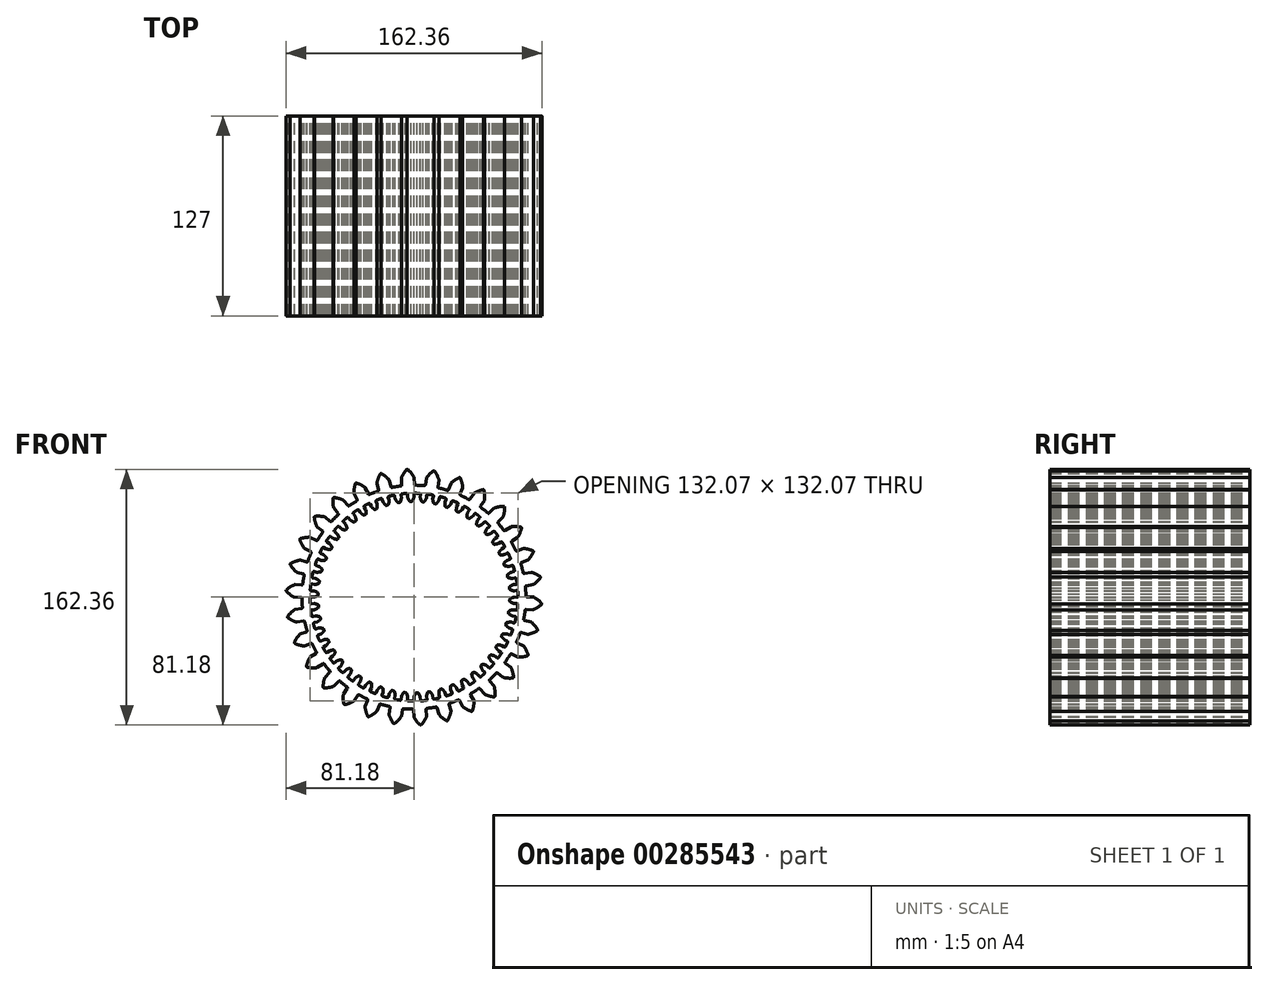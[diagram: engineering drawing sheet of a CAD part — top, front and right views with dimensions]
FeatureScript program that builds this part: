
annotation { "Feature Type Name" : "Feature", "Feature Type Description" : "" }
export const myFeature = defineFeature(function(context is Context, id is Id, definition is map)
    precondition{}
    {
        {
            var Q0;
            Q0=qCreatedBy(makeId("Front.planeOp"),FACE);
            var sketch = newSketch(context, id + "F0", { "sketchPlane" : qUnion([Q0])});
            skArc(sketch, "E0.MirrorCS", {"start": v(-3.95, 63.27) * mm, "mid": v(-3.48, 62.2) * mm, "end": v(-2.94, 61.17) * mm});
            skLineSegment(sketch, "E1.MirrorCS", {"start": v(-2.38, 60.85) * mm, "end": v(-1.91, 60.85) * mm});
            skLineSegment(sketch, "E2.MirrorCS", {"start": v(-1.44, 60.88) * mm, "end": v(-1.91, 60.85) * mm});
            skArc(sketch, "E3.MirrorCS", {"start": v(-0.03, 63.4) * mm, "mid": v(-0.43, 62.3) * mm, "end": v(-0.91, 61.23) * mm});
            skLineSegment(sketch, "E4.MirrorCS", {"start": v(-4, 63.48) * mm, "end": v(-4.05, 65.26) * mm});
            skLineSegment(sketch, "E5.MirrorCS", {"start": v(0, 63.6) * mm, "end": v(-0.06, 65.38) * mm});
            skArc(sketch, "E6", {"start": v(-4.73, 65.87) * mm, "mid": v(2.07, -66) * mm, "end": v(0.58, 66.04) * mm});
            skPoint(sketch, "E7.visualSharp", {"position": v(0, 63.5) * mm});
            skArc(sketch, "E7.filletArc", {"start": v(-0.03, 63.4) * mm, "mid": v(0, 63.5) * mm, "end": v(0, 63.6) * mm});
            skPoint(sketch, "E8.visualSharp", {"position": v(-3.99, 63.37) * mm});
            skArc(sketch, "E8.filletArc", {"start": v(-4, 63.48) * mm, "mid": v(-3.98, 63.38) * mm, "end": v(-3.95, 63.27) * mm});
            skPoint(sketch, "E9.visualSharp", {"position": v(-2.75, 60.85) * mm});
            skArc(sketch, "E9.filletArc", {"start": v(-2.94, 61.17) * mm, "mid": v(-2.7, 60.93) * mm, "end": v(-2.38, 60.85) * mm});
            skPoint(sketch, "E10.visualSharp", {"position": v(-1.08, 60.9) * mm});
            skArc(sketch, "E10.filletArc", {"start": v(-1.44, 60.88) * mm, "mid": v(-1.13, 60.98) * mm, "end": v(-0.91, 61.23) * mm});
            skPoint(sketch, "E11.visualSharp", {"position": v(-4.07, 65.91) * mm});
            skArc(sketch, "E11.filletArc", {"start": v(-4.05, 65.26) * mm, "mid": v(-4.26, 65.7) * mm, "end": v(-4.73, 65.87) * mm});
            skPoint(sketch, "E12.visualSharp", {"position": v(-0.08, 66.04) * mm});
            skArc(sketch, "E12.filletArc", {"start": v(0.58, 66.04) * mm, "mid": v(0.12, 65.85) * mm, "end": v(-0.06, 65.38) * mm});
            skPoint(sketch, "E13.1.1", {"position": v(-57.15, -33.09) * mm});
            skPoint(sketch, "E13.2.1", {"position": v(57.23, -32.95) * mm});
            skArc(sketch, "E14.1.0", {"start": v(-12.2, 64.24) * mm, "mid": v(-12.46, 64.66) * mm, "end": v(-12.95, 64.76) * mm});
            skArc(sketch, "E14.1.1", {"start": v(-7.7, 65.59) * mm, "mid": v(-8.13, 65.34) * mm, "end": v(-8.25, 64.86) * mm});
            skLineSegment(sketch, "E14.1.2", {"start": v(-7.98, 63.1) * mm, "end": v(-8.25, 64.86) * mm});
            skLineSegment(sketch, "E14.1.3", {"start": v(-11.92, 62.48) * mm, "end": v(-12.2, 64.24) * mm});
            skArc(sketch, "E14.1.4", {"start": v(-11.85, 62.28) * mm, "mid": v(-11.25, 61.27) * mm, "end": v(-10.58, 60.31) * mm});
            skPoint(sketch, "E14.1.5", {"position": v(-10.35, 60.02) * mm});
            skArc(sketch, "E14.1.6", {"start": v(-7.98, 62.9) * mm, "mid": v(-8.24, 61.75) * mm, "end": v(-8.58, 60.63) * mm});
            skPoint(sketch, "E14.1.7", {"position": v(-7.96, 63) * mm});
            skPoint(sketch, "E14.1.8", {"position": v(-11.9, 62.38) * mm});
            skPoint(sketch, "E14.1.9", {"position": v(-8.7, 60.28) * mm});
            skArc(sketch, "E14.1.10", {"start": v(-10.58, 60.31) * mm, "mid": v(-10.32, 60.11) * mm, "end": v(-10, 60.07) * mm});
            skArc(sketch, "E14.1.11", {"start": v(-9.06, 60.22) * mm, "mid": v(-8.76, 60.36) * mm, "end": v(-8.58, 60.63) * mm});
            skLineSegment(sketch, "E14.1.12", {"start": v(-9.06, 60.22) * mm, "end": v(-9.52, 60.13) * mm});
            skLineSegment(sketch, "E14.1.13", {"start": v(-10, 60.07) * mm, "end": v(-9.52, 60.13) * mm});
            skArc(sketch, "E14.1.14", {"start": v(-11.92, 62.48) * mm, "mid": v(-11.89, 62.38) * mm, "end": v(-11.85, 62.28) * mm});
            skArc(sketch, "E14.1.15", {"start": v(-7.98, 62.9) * mm, "mid": v(-7.97, 63) * mm, "end": v(-7.98, 63.1) * mm});
            skArc(sketch, "E14.2.0", {"start": v(-20.15, 62.2) * mm, "mid": v(-20.46, 62.59) * mm, "end": v(-20.96, 62.63) * mm});
            skArc(sketch, "E14.2.1", {"start": v(-15.86, 64.1) * mm, "mid": v(-16.26, 63.8) * mm, "end": v(-16.32, 63.31) * mm});
            skLineSegment(sketch, "E14.2.2", {"start": v(-15.82, 61.6) * mm, "end": v(-16.32, 63.31) * mm});
            skLineSegment(sketch, "E14.2.3", {"start": v(-19.65, 60.5) * mm, "end": v(-20.15, 62.2) * mm});
            skArc(sketch, "E14.2.4", {"start": v(-19.56, 60.3) * mm, "mid": v(-18.84, 59.38) * mm, "end": v(-18.05, 58.51) * mm});
            skPoint(sketch, "E14.2.5", {"position": v(-17.8, 58.25) * mm});
            skArc(sketch, "E14.2.6", {"start": v(-15.8, 61.4) * mm, "mid": v(-15.91, 60.23) * mm, "end": v(-16.1, 59.08) * mm});
            skPoint(sketch, "E14.2.7", {"position": v(-15.8, 61.5) * mm});
            skPoint(sketch, "E14.2.8", {"position": v(-19.62, 60.4) * mm});
            skPoint(sketch, "E14.2.9", {"position": v(-16.19, 58.72) * mm});
            skArc(sketch, "E14.2.10", {"start": v(-18.05, 58.51) * mm, "mid": v(-17.77, 58.35) * mm, "end": v(-17.44, 58.34) * mm});
            skArc(sketch, "E14.2.11", {"start": v(-16.53, 58.6) * mm, "mid": v(-16.26, 58.78) * mm, "end": v(-16.1, 59.08) * mm});
            skLineSegment(sketch, "E14.2.12", {"start": v(-16.53, 58.6) * mm, "end": v(-16.98, 58.46) * mm});
            skLineSegment(sketch, "E14.2.13", {"start": v(-17.44, 58.34) * mm, "end": v(-16.98, 58.46) * mm});
            skArc(sketch, "E14.2.14", {"start": v(-19.65, 60.5) * mm, "mid": v(-19.61, 60.4) * mm, "end": v(-19.56, 60.3) * mm});
            skArc(sketch, "E14.2.15", {"start": v(-15.8, 61.4) * mm, "mid": v(-15.8, 61.5) * mm, "end": v(-15.82, 61.6) * mm});
            skArc(sketch, "E14.3.0", {"start": v(-27.78, 59.19) * mm, "mid": v(-28.15, 59.53) * mm, "end": v(-28.64, 59.5) * mm});
            skArc(sketch, "E14.3.1", {"start": v(-23.77, 61.61) * mm, "mid": v(-24.13, 61.27) * mm, "end": v(-24.12, 60.77) * mm});
            skLineSegment(sketch, "E14.3.2", {"start": v(-23.42, 59.14) * mm, "end": v(-24.12, 60.77) * mm});
            skLineSegment(sketch, "E14.3.3", {"start": v(-27.08, 57.56) * mm, "end": v(-27.78, 59.19) * mm});
            skArc(sketch, "E14.3.4", {"start": v(-26.96, 57.38) * mm, "mid": v(-26.13, 56.55) * mm, "end": v(-25.25, 55.79) * mm});
            skPoint(sketch, "E14.3.5", {"position": v(-24.95, 55.56) * mm});
            skArc(sketch, "E14.3.6", {"start": v(-23.37, 58.93) * mm, "mid": v(-23.33, 57.76) * mm, "end": v(-23.39, 56.6) * mm});
            skPoint(sketch, "E14.3.7", {"position": v(-23.38, 59.04) * mm});
            skPoint(sketch, "E14.3.8", {"position": v(-27.04, 57.46) * mm});
            skPoint(sketch, "E14.3.9", {"position": v(-23.42, 56.23) * mm});
            skArc(sketch, "E14.3.10", {"start": v(-25.25, 55.79) * mm, "mid": v(-24.94, 55.66) * mm, "end": v(-24.62, 55.7) * mm});
            skArc(sketch, "E14.3.11", {"start": v(-23.75, 56.07) * mm, "mid": v(-23.5, 56.28) * mm, "end": v(-23.39, 56.6) * mm});
            skLineSegment(sketch, "E14.3.12", {"start": v(-23.75, 56.07) * mm, "end": v(-24.18, 55.87) * mm});
            skLineSegment(sketch, "E14.3.13", {"start": v(-24.62, 55.7) * mm, "end": v(-24.18, 55.87) * mm});
            skArc(sketch, "E14.3.14", {"start": v(-27.08, 57.56) * mm, "mid": v(-27.03, 57.46) * mm, "end": v(-26.96, 57.38) * mm});
            skArc(sketch, "E14.3.15", {"start": v(-23.37, 58.93) * mm, "mid": v(-23.38, 59.04) * mm, "end": v(-23.42, 59.14) * mm});
            skArc(sketch, "E14.4.0", {"start": v(-34.98, 55.24) * mm, "mid": v(-35.38, 55.53) * mm, "end": v(-35.88, 55.45) * mm});
            skArc(sketch, "E14.4.1", {"start": v(-31.3, 58.15) * mm, "mid": v(-31.62, 57.76) * mm, "end": v(-31.55, 57.27) * mm});
            skLineSegment(sketch, "E14.4.2", {"start": v(-30.65, 55.74) * mm, "end": v(-31.55, 57.27) * mm});
            skLineSegment(sketch, "E14.4.3", {"start": v(-34.08, 53.7) * mm, "end": v(-34.98, 55.24) * mm});
            skArc(sketch, "E14.4.4", {"start": v(-33.94, 53.54) * mm, "mid": v(-33.01, 52.83) * mm, "end": v(-32.04, 52.19) * mm});
            skPoint(sketch, "E14.4.5", {"position": v(-31.72, 52) * mm});
            skArc(sketch, "E14.4.6", {"start": v(-30.57, 55.54) * mm, "mid": v(-30.39, 54.38) * mm, "end": v(-30.3, 53.22) * mm});
            skPoint(sketch, "E14.4.7", {"position": v(-30.6, 55.65) * mm});
            skPoint(sketch, "E14.4.8", {"position": v(-34.03, 53.61) * mm});
            skPoint(sketch, "E14.4.9", {"position": v(-30.28, 52.85) * mm});
            skArc(sketch, "E14.4.10", {"start": v(-32.04, 52.19) * mm, "mid": v(-31.72, 52.1) * mm, "end": v(-31.4, 52.17) * mm});
            skArc(sketch, "E14.4.11", {"start": v(-30.59, 52.65) * mm, "mid": v(-30.37, 52.9) * mm, "end": v(-30.3, 53.22) * mm});
            skLineSegment(sketch, "E14.4.12", {"start": v(-30.59, 52.65) * mm, "end": v(-30.99, 52.4) * mm});
            skLineSegment(sketch, "E14.4.13", {"start": v(-31.4, 52.17) * mm, "end": v(-30.99, 52.4) * mm});
            skArc(sketch, "E14.4.14", {"start": v(-34.08, 53.7) * mm, "mid": v(-34.02, 53.62) * mm, "end": v(-33.94, 53.54) * mm});
            skArc(sketch, "E14.4.15", {"start": v(-30.57, 55.54) * mm, "mid": v(-30.6, 55.64) * mm, "end": v(-30.65, 55.74) * mm});
            skArc(sketch, "E14.5.0", {"start": v(-41.63, 50.42) * mm, "mid": v(-42.07, 50.66) * mm, "end": v(-42.54, 50.51) * mm});
            skArc(sketch, "E14.5.1", {"start": v(-38.35, 53.77) * mm, "mid": v(-38.6, 53.34) * mm, "end": v(-38.48, 52.86) * mm});
            skLineSegment(sketch, "E14.5.2", {"start": v(-37.4, 51.46) * mm, "end": v(-38.48, 52.86) * mm});
            skLineSegment(sketch, "E14.5.3", {"start": v(-40.54, 49.01) * mm, "end": v(-41.63, 50.42) * mm});
            skArc(sketch, "E14.5.4", {"start": v(-40.38, 48.87) * mm, "mid": v(-39.38, 48.27) * mm, "end": v(-38.33, 47.76) * mm});
            skPoint(sketch, "E14.5.5", {"position": v(-37.99, 47.61) * mm});
            skArc(sketch, "E14.5.6", {"start": v(-37.29, 51.27) * mm, "mid": v(-36.97, 50.14) * mm, "end": v(-36.73, 49) * mm});
            skPoint(sketch, "E14.5.7", {"position": v(-37.32, 51.37) * mm});
            skPoint(sketch, "E14.5.8", {"position": v(-40.48, 48.93) * mm});
            skPoint(sketch, "E14.5.9", {"position": v(-36.67, 48.63) * mm});
            skArc(sketch, "E14.5.10", {"start": v(-38.33, 47.76) * mm, "mid": v(-38, 47.7) * mm, "end": v(-37.7, 47.82) * mm});
            skArc(sketch, "E14.5.11", {"start": v(-36.95, 48.4) * mm, "mid": v(-36.76, 48.67) * mm, "end": v(-36.73, 49) * mm});
            skLineSegment(sketch, "E14.5.12", {"start": v(-36.95, 48.4) * mm, "end": v(-37.31, 48.1) * mm});
            skLineSegment(sketch, "E14.5.13", {"start": v(-37.7, 47.82) * mm, "end": v(-37.31, 48.1) * mm});
            skArc(sketch, "E14.5.14", {"start": v(-40.54, 49.01) * mm, "mid": v(-40.47, 48.93) * mm, "end": v(-40.38, 48.87) * mm});
            skArc(sketch, "E14.5.15", {"start": v(-37.29, 51.27) * mm, "mid": v(-37.33, 51.37) * mm, "end": v(-37.4, 51.46) * mm});
            skArc(sketch, "E14.6.0", {"start": v(-47.62, 44.8) * mm, "mid": v(-48.08, 44.99) * mm, "end": v(-48.54, 44.78) * mm});
            skArc(sketch, "E14.6.1", {"start": v(-44.78, 48.54) * mm, "mid": v(-44.99, 48.08) * mm, "end": v(-44.8, 47.62) * mm});
            skLineSegment(sketch, "E14.6.2", {"start": v(-43.55, 46.37) * mm, "end": v(-44.8, 47.62) * mm});
            skLineSegment(sketch, "E14.6.3", {"start": v(-46.37, 43.55) * mm, "end": v(-47.62, 44.8) * mm});
            skArc(sketch, "E14.6.4", {"start": v(-46.19, 43.42) * mm, "mid": v(-45.12, 42.96) * mm, "end": v(-44.01, 42.58) * mm});
            skPoint(sketch, "E14.6.5", {"position": v(-43.65, 42.47) * mm});
            skArc(sketch, "E14.6.6", {"start": v(-43.42, 46.19) * mm, "mid": v(-42.96, 45.12) * mm, "end": v(-42.58, 44.01) * mm});
            skPoint(sketch, "E14.6.7", {"position": v(-43.47, 46.29) * mm});
            skPoint(sketch, "E14.6.8", {"position": v(-46.29, 43.47) * mm});
            skPoint(sketch, "E14.6.9", {"position": v(-42.47, 43.65) * mm});
            skArc(sketch, "E14.6.10", {"start": v(-44.01, 42.58) * mm, "mid": v(-43.68, 42.57) * mm, "end": v(-43.4, 42.72) * mm});
            skArc(sketch, "E14.6.11", {"start": v(-42.72, 43.4) * mm, "mid": v(-42.57, 43.68) * mm, "end": v(-42.58, 44.01) * mm});
            skLineSegment(sketch, "E14.6.12", {"start": v(-42.72, 43.4) * mm, "end": v(-43.05, 43.05) * mm});
            skLineSegment(sketch, "E14.6.13", {"start": v(-43.4, 42.72) * mm, "end": v(-43.05, 43.05) * mm});
            skArc(sketch, "E14.6.14", {"start": v(-46.37, 43.55) * mm, "mid": v(-46.28, 43.48) * mm, "end": v(-46.19, 43.42) * mm});
            skArc(sketch, "E14.6.15", {"start": v(-43.42, 46.19) * mm, "mid": v(-43.48, 46.28) * mm, "end": v(-43.55, 46.37) * mm});
            skArc(sketch, "E14.7.0", {"start": v(-52.86, 38.48) * mm, "mid": v(-53.34, 38.6) * mm, "end": v(-53.77, 38.35) * mm});
            skArc(sketch, "E14.7.1", {"start": v(-50.51, 42.54) * mm, "mid": v(-50.66, 42.07) * mm, "end": v(-50.42, 41.63) * mm});
            skLineSegment(sketch, "E14.7.2", {"start": v(-49.01, 40.54) * mm, "end": v(-50.42, 41.63) * mm});
            skLineSegment(sketch, "E14.7.3", {"start": v(-51.46, 37.4) * mm, "end": v(-52.86, 38.48) * mm});
            skArc(sketch, "E14.7.4", {"start": v(-51.27, 37.29) * mm, "mid": v(-50.14, 36.97) * mm, "end": v(-49, 36.73) * mm});
            skPoint(sketch, "E14.7.5", {"position": v(-48.63, 36.67) * mm});
            skArc(sketch, "E14.7.6", {"start": v(-48.87, 40.38) * mm, "mid": v(-48.27, 39.38) * mm, "end": v(-47.76, 38.33) * mm});
            skPoint(sketch, "E14.7.7", {"position": v(-48.93, 40.48) * mm});
            skPoint(sketch, "E14.7.8", {"position": v(-51.37, 37.32) * mm});
            skPoint(sketch, "E14.7.9", {"position": v(-47.61, 37.99) * mm});
            skArc(sketch, "E14.7.10", {"start": v(-49, 36.73) * mm, "mid": v(-48.67, 36.76) * mm, "end": v(-48.4, 36.95) * mm});
            skArc(sketch, "E14.7.11", {"start": v(-47.82, 37.7) * mm, "mid": v(-47.7, 38) * mm, "end": v(-47.76, 38.33) * mm});
            skLineSegment(sketch, "E14.7.12", {"start": v(-47.82, 37.7) * mm, "end": v(-48.1, 37.31) * mm});
            skLineSegment(sketch, "E14.7.13", {"start": v(-48.4, 36.95) * mm, "end": v(-48.1, 37.31) * mm});
            skArc(sketch, "E14.7.14", {"start": v(-51.46, 37.4) * mm, "mid": v(-51.37, 37.33) * mm, "end": v(-51.27, 37.29) * mm});
            skArc(sketch, "E14.7.15", {"start": v(-48.87, 40.38) * mm, "mid": v(-48.93, 40.47) * mm, "end": v(-49.01, 40.54) * mm});
            skArc(sketch, "E14.8.0", {"start": v(-57.27, 31.55) * mm, "mid": v(-57.76, 31.62) * mm, "end": v(-58.15, 31.3) * mm});
            skArc(sketch, "E14.8.1", {"start": v(-55.45, 35.88) * mm, "mid": v(-55.53, 35.38) * mm, "end": v(-55.24, 34.98) * mm});
            skLineSegment(sketch, "E14.8.2", {"start": v(-53.7, 34.08) * mm, "end": v(-55.24, 34.98) * mm});
            skLineSegment(sketch, "E14.8.3", {"start": v(-55.74, 30.65) * mm, "end": v(-57.27, 31.55) * mm});
            skArc(sketch, "E14.8.4", {"start": v(-55.54, 30.57) * mm, "mid": v(-54.38, 30.39) * mm, "end": v(-53.22, 30.3) * mm});
            skPoint(sketch, "E14.8.5", {"position": v(-52.85, 30.28) * mm});
            skArc(sketch, "E14.8.6", {"start": v(-53.54, 33.94) * mm, "mid": v(-52.83, 33.01) * mm, "end": v(-52.19, 32.04) * mm});
            skPoint(sketch, "E14.8.7", {"position": v(-53.61, 34.03) * mm});
            skPoint(sketch, "E14.8.8", {"position": v(-55.65, 30.6) * mm});
            skPoint(sketch, "E14.8.9", {"position": v(-52, 31.72) * mm});
            skArc(sketch, "E14.8.10", {"start": v(-53.22, 30.3) * mm, "mid": v(-52.9, 30.37) * mm, "end": v(-52.65, 30.59) * mm});
            skArc(sketch, "E14.8.11", {"start": v(-52.17, 31.4) * mm, "mid": v(-52.1, 31.72) * mm, "end": v(-52.19, 32.04) * mm});
            skLineSegment(sketch, "E14.8.12", {"start": v(-52.17, 31.4) * mm, "end": v(-52.4, 30.99) * mm});
            skLineSegment(sketch, "E14.8.13", {"start": v(-52.65, 30.59) * mm, "end": v(-52.4, 30.99) * mm});
            skArc(sketch, "E14.8.14", {"start": v(-55.74, 30.65) * mm, "mid": v(-55.64, 30.6) * mm, "end": v(-55.54, 30.57) * mm});
            skArc(sketch, "E14.8.15", {"start": v(-53.54, 33.94) * mm, "mid": v(-53.62, 34.02) * mm, "end": v(-53.7, 34.08) * mm});
            skArc(sketch, "E14.9.0", {"start": v(-60.77, 24.12) * mm, "mid": v(-61.27, 24.13) * mm, "end": v(-61.61, 23.77) * mm});
            skArc(sketch, "E14.9.1", {"start": v(-59.5, 28.64) * mm, "mid": v(-59.53, 28.15) * mm, "end": v(-59.19, 27.78) * mm});
            skLineSegment(sketch, "E14.9.2", {"start": v(-57.56, 27.08) * mm, "end": v(-59.19, 27.78) * mm});
            skLineSegment(sketch, "E14.9.3", {"start": v(-59.14, 23.42) * mm, "end": v(-60.77, 24.12) * mm});
            skArc(sketch, "E14.9.4", {"start": v(-58.93, 23.37) * mm, "mid": v(-57.76, 23.33) * mm, "end": v(-56.6, 23.39) * mm});
            skPoint(sketch, "E14.9.5", {"position": v(-56.23, 23.42) * mm});
            skArc(sketch, "E14.9.6", {"start": v(-57.38, 26.96) * mm, "mid": v(-56.55, 26.13) * mm, "end": v(-55.79, 25.25) * mm});
            skPoint(sketch, "E14.9.7", {"position": v(-57.46, 27.04) * mm});
            skPoint(sketch, "E14.9.8", {"position": v(-59.04, 23.38) * mm});
            skPoint(sketch, "E14.9.9", {"position": v(-55.56, 24.95) * mm});
            skArc(sketch, "E14.9.10", {"start": v(-56.6, 23.39) * mm, "mid": v(-56.28, 23.5) * mm, "end": v(-56.07, 23.75) * mm});
            skArc(sketch, "E14.9.11", {"start": v(-55.7, 24.62) * mm, "mid": v(-55.66, 24.94) * mm, "end": v(-55.79, 25.25) * mm});
            skLineSegment(sketch, "E14.9.12", {"start": v(-55.7, 24.62) * mm, "end": v(-55.87, 24.18) * mm});
            skLineSegment(sketch, "E14.9.13", {"start": v(-56.07, 23.75) * mm, "end": v(-55.87, 24.18) * mm});
            skArc(sketch, "E14.9.14", {"start": v(-59.14, 23.42) * mm, "mid": v(-59.04, 23.38) * mm, "end": v(-58.93, 23.37) * mm});
            skArc(sketch, "E14.9.15", {"start": v(-57.38, 26.96) * mm, "mid": v(-57.46, 27.03) * mm, "end": v(-57.56, 27.08) * mm});
            skArc(sketch, "E14.10.0", {"start": v(-63.31, 16.32) * mm, "mid": v(-63.8, 16.26) * mm, "end": v(-64.1, 15.86) * mm});
            skArc(sketch, "E14.10.1", {"start": v(-62.63, 20.96) * mm, "mid": v(-62.59, 20.46) * mm, "end": v(-62.2, 20.15) * mm});
            skLineSegment(sketch, "E14.10.2", {"start": v(-60.5, 19.65) * mm, "end": v(-62.2, 20.15) * mm});
            skLineSegment(sketch, "E14.10.3", {"start": v(-61.6, 15.82) * mm, "end": v(-63.31, 16.32) * mm});
            skArc(sketch, "E14.10.4", {"start": v(-61.4, 15.8) * mm, "mid": v(-60.23, 15.91) * mm, "end": v(-59.08, 16.1) * mm});
            skPoint(sketch, "E14.10.5", {"position": v(-58.72, 16.19) * mm});
            skArc(sketch, "E14.10.6", {"start": v(-60.3, 19.56) * mm, "mid": v(-59.38, 18.84) * mm, "end": v(-58.51, 18.05) * mm});
            skPoint(sketch, "E14.10.7", {"position": v(-60.4, 19.62) * mm});
            skPoint(sketch, "E14.10.8", {"position": v(-61.5, 15.8) * mm});
            skPoint(sketch, "E14.10.9", {"position": v(-58.25, 17.8) * mm});
            skArc(sketch, "E14.10.10", {"start": v(-59.08, 16.1) * mm, "mid": v(-58.78, 16.26) * mm, "end": v(-58.6, 16.53) * mm});
            skArc(sketch, "E14.10.11", {"start": v(-58.34, 17.44) * mm, "mid": v(-58.35, 17.77) * mm, "end": v(-58.51, 18.05) * mm});
            skLineSegment(sketch, "E14.10.12", {"start": v(-58.34, 17.44) * mm, "end": v(-58.46, 16.98) * mm});
            skLineSegment(sketch, "E14.10.13", {"start": v(-58.6, 16.53) * mm, "end": v(-58.46, 16.98) * mm});
            skArc(sketch, "E14.10.14", {"start": v(-61.6, 15.82) * mm, "mid": v(-61.5, 15.8) * mm, "end": v(-61.4, 15.8) * mm});
            skArc(sketch, "E14.10.15", {"start": v(-60.3, 19.56) * mm, "mid": v(-60.4, 19.61) * mm, "end": v(-60.5, 19.65) * mm});
            skArc(sketch, "E14.11.0", {"start": v(-64.86, 8.25) * mm, "mid": v(-65.34, 8.13) * mm, "end": v(-65.59, 7.7) * mm});
            skArc(sketch, "E14.11.1", {"start": v(-64.76, 12.95) * mm, "mid": v(-64.66, 12.46) * mm, "end": v(-64.24, 12.2) * mm});
            skLineSegment(sketch, "E14.11.2", {"start": v(-62.48, 11.92) * mm, "end": v(-64.24, 12.2) * mm});
            skLineSegment(sketch, "E14.11.3", {"start": v(-63.1, 7.98) * mm, "end": v(-64.86, 8.25) * mm});
            skArc(sketch, "E14.11.4", {"start": v(-62.9, 7.98) * mm, "mid": v(-61.75, 8.24) * mm, "end": v(-60.63, 8.58) * mm});
            skPoint(sketch, "E14.11.5", {"position": v(-60.28, 8.7) * mm});
            skArc(sketch, "E14.11.6", {"start": v(-62.28, 11.85) * mm, "mid": v(-61.27, 11.25) * mm, "end": v(-60.31, 10.58) * mm});
            skPoint(sketch, "E14.11.7", {"position": v(-62.38, 11.9) * mm});
            skPoint(sketch, "E14.11.8", {"position": v(-63, 7.96) * mm});
            skPoint(sketch, "E14.11.9", {"position": v(-60.02, 10.35) * mm});
            skArc(sketch, "E14.11.10", {"start": v(-60.63, 8.58) * mm, "mid": v(-60.36, 8.76) * mm, "end": v(-60.22, 9.06) * mm});
            skArc(sketch, "E14.11.11", {"start": v(-60.07, 10) * mm, "mid": v(-60.11, 10.32) * mm, "end": v(-60.31, 10.58) * mm});
            skLineSegment(sketch, "E14.11.12", {"start": v(-60.07, 10) * mm, "end": v(-60.13, 9.52) * mm});
            skLineSegment(sketch, "E14.11.13", {"start": v(-60.22, 9.06) * mm, "end": v(-60.13, 9.52) * mm});
            skArc(sketch, "E14.11.14", {"start": v(-63.1, 7.98) * mm, "mid": v(-63, 7.97) * mm, "end": v(-62.9, 7.98) * mm});
            skArc(sketch, "E14.11.15", {"start": v(-62.28, 11.85) * mm, "mid": v(-62.38, 11.89) * mm, "end": v(-62.48, 11.92) * mm});
            skArc(sketch, "E14.12.0", {"start": v(-65.38, 0.06) * mm, "mid": v(-65.85, -0.12) * mm, "end": v(-66.04, -0.58) * mm});
            skArc(sketch, "E14.12.1", {"start": v(-65.87, 4.73) * mm, "mid": v(-65.7, 4.26) * mm, "end": v(-65.26, 4.05) * mm});
            skLineSegment(sketch, "E14.12.2", {"start": v(-63.48, 4) * mm, "end": v(-65.26, 4.05) * mm});
            skLineSegment(sketch, "E14.12.3", {"start": v(-63.6, 0) * mm, "end": v(-65.38, 0.06) * mm});
            skArc(sketch, "E14.12.4", {"start": v(-63.4, 0.03) * mm, "mid": v(-62.3, 0.43) * mm, "end": v(-61.23, 0.91) * mm});
            skPoint(sketch, "E14.12.5", {"position": v(-60.9, 1.08) * mm});
            skArc(sketch, "E14.12.6", {"start": v(-63.27, 3.95) * mm, "mid": v(-62.2, 3.48) * mm, "end": v(-61.17, 2.94) * mm});
            skPoint(sketch, "E14.12.7", {"position": v(-63.37, 3.99) * mm});
            skPoint(sketch, "E14.12.8", {"position": v(-63.5, 0) * mm});
            skPoint(sketch, "E14.12.9", {"position": v(-60.85, 2.75) * mm});
            skArc(sketch, "E14.12.10", {"start": v(-61.23, 0.91) * mm, "mid": v(-60.98, 1.13) * mm, "end": v(-60.88, 1.44) * mm});
            skArc(sketch, "E14.12.11", {"start": v(-60.85, 2.38) * mm, "mid": v(-60.93, 2.7) * mm, "end": v(-61.17, 2.94) * mm});
            skLineSegment(sketch, "E14.12.12", {"start": v(-60.85, 2.38) * mm, "end": v(-60.85, 1.91) * mm});
            skLineSegment(sketch, "E14.12.13", {"start": v(-60.88, 1.44) * mm, "end": v(-60.85, 1.91) * mm});
            skArc(sketch, "E14.12.14", {"start": v(-63.6, 0) * mm, "mid": v(-63.5, 0) * mm, "end": v(-63.4, 0.03) * mm});
            skArc(sketch, "E14.12.15", {"start": v(-63.27, 3.95) * mm, "mid": v(-63.38, 3.98) * mm, "end": v(-63.48, 4) * mm});
            skArc(sketch, "E14.13.0", {"start": v(-64.87, -8.14) * mm, "mid": v(-65.31, -8.37) * mm, "end": v(-65.44, -8.85) * mm});
            skArc(sketch, "E14.13.1", {"start": v(-65.94, -3.57) * mm, "mid": v(-65.72, -4.01) * mm, "end": v(-65.25, -4.16) * mm});
            skLineSegment(sketch, "E14.13.2", {"start": v(-63.48, -4) * mm, "end": v(-65.25, -4.16) * mm});
            skLineSegment(sketch, "E14.13.3", {"start": v(-63.1, -7.97) * mm, "end": v(-64.87, -8.14) * mm});
            skArc(sketch, "E14.13.4", {"start": v(-62.9, -7.91) * mm, "mid": v(-61.86, -7.38) * mm, "end": v(-60.86, -6.77) * mm});
            skPoint(sketch, "E14.13.5", {"position": v(-60.55, -6.56) * mm});
            skArc(sketch, "E14.13.6", {"start": v(-63.27, -4.01) * mm, "mid": v(-62.15, -4.34) * mm, "end": v(-61.05, -4.75) * mm});
            skPoint(sketch, "E14.13.7", {"position": v(-63.37, -3.99) * mm});
            skPoint(sketch, "E14.13.8", {"position": v(-63, -7.96) * mm});
            skPoint(sketch, "E14.13.9", {"position": v(-60.71, -4.9) * mm});
            skArc(sketch, "E14.13.10", {"start": v(-60.86, -6.77) * mm, "mid": v(-60.64, -6.52) * mm, "end": v(-60.58, -6.2) * mm});
            skArc(sketch, "E14.13.11", {"start": v(-60.67, -5.26) * mm, "mid": v(-60.8, -4.96) * mm, "end": v(-61.05, -4.75) * mm});
            skLineSegment(sketch, "E14.13.12", {"start": v(-60.67, -5.26) * mm, "end": v(-60.6, -5.73) * mm});
            skLineSegment(sketch, "E14.13.13", {"start": v(-60.58, -6.2) * mm, "end": v(-60.6, -5.73) * mm});
            skArc(sketch, "E14.13.14", {"start": v(-63.1, -7.97) * mm, "mid": v(-63, -7.95) * mm, "end": v(-62.9, -7.91) * mm});
            skArc(sketch, "E14.13.15", {"start": v(-63.27, -4.01) * mm, "mid": v(-63.37, -4) * mm, "end": v(-63.48, -4) * mm});
            skArc(sketch, "E14.14.0", {"start": v(-63.34, -16.2) * mm, "mid": v(-63.75, -16.5) * mm, "end": v(-63.82, -16.99) * mm});
            skArc(sketch, "E14.14.1", {"start": v(-64.98, -11.8) * mm, "mid": v(-64.7, -12.22) * mm, "end": v(-64.21, -12.3) * mm});
            skLineSegment(sketch, "E14.14.2", {"start": v(-62.48, -11.92) * mm, "end": v(-64.21, -12.3) * mm});
            skLineSegment(sketch, "E14.14.3", {"start": v(-61.61, -15.82) * mm, "end": v(-63.34, -16.2) * mm});
            skArc(sketch, "E14.14.4", {"start": v(-61.41, -15.73) * mm, "mid": v(-60.45, -15.07) * mm, "end": v(-59.53, -14.34) * mm});
            skPoint(sketch, "E14.14.5", {"position": v(-59.25, -14.1) * mm});
            skArc(sketch, "E14.14.6", {"start": v(-62.27, -11.91) * mm, "mid": v(-61.11, -12.1) * mm, "end": v(-59.97, -12.37) * mm});
            skPoint(sketch, "E14.14.7", {"position": v(-62.38, -11.9) * mm});
            skPoint(sketch, "E14.14.8", {"position": v(-61.5, -15.8) * mm});
            skPoint(sketch, "E14.14.9", {"position": v(-59.62, -12.47) * mm});
            skArc(sketch, "E14.14.10", {"start": v(-59.53, -14.34) * mm, "mid": v(-59.35, -14.07) * mm, "end": v(-59.32, -13.74) * mm});
            skArc(sketch, "E14.14.11", {"start": v(-59.53, -12.82) * mm, "mid": v(-59.69, -12.54) * mm, "end": v(-59.97, -12.37) * mm});
            skLineSegment(sketch, "E14.14.12", {"start": v(-59.53, -12.82) * mm, "end": v(-59.41, -13.28) * mm});
            skLineSegment(sketch, "E14.14.13", {"start": v(-59.32, -13.74) * mm, "end": v(-59.41, -13.28) * mm});
            skArc(sketch, "E14.14.14", {"start": v(-61.61, -15.82) * mm, "mid": v(-61.5, -15.78) * mm, "end": v(-61.41, -15.73) * mm});
            skArc(sketch, "E14.14.15", {"start": v(-62.27, -11.91) * mm, "mid": v(-62.37, -11.9) * mm, "end": v(-62.48, -11.92) * mm});
            skArc(sketch, "E14.15.0", {"start": v(-60.81, -24.01) * mm, "mid": v(-61.18, -24.35) * mm, "end": v(-61.19, -24.85) * mm});
            skArc(sketch, "E14.15.1", {"start": v(-62.98, -19.85) * mm, "mid": v(-62.66, -20.23) * mm, "end": v(-62.16, -20.26) * mm});
            skLineSegment(sketch, "E14.15.2", {"start": v(-60.5, -19.66) * mm, "end": v(-62.16, -20.26) * mm});
            skLineSegment(sketch, "E14.15.3", {"start": v(-59.14, -23.41) * mm, "end": v(-60.81, -24.01) * mm});
            skArc(sketch, "E14.15.4", {"start": v(-58.95, -23.3) * mm, "mid": v(-58.08, -22.53) * mm, "end": v(-57.26, -21.7) * mm});
            skPoint(sketch, "E14.15.5", {"position": v(-57.02, -21.42) * mm});
            skArc(sketch, "E14.15.6", {"start": v(-60.28, -19.62) * mm, "mid": v(-59.11, -19.66) * mm, "end": v(-57.95, -19.79) * mm});
            skPoint(sketch, "E14.15.7", {"position": v(-60.4, -19.62) * mm});
            skPoint(sketch, "E14.15.8", {"position": v(-59.04, -23.38) * mm});
            skPoint(sketch, "E14.15.9", {"position": v(-57.58, -19.84) * mm});
            skArc(sketch, "E14.15.10", {"start": v(-57.26, -21.7) * mm, "mid": v(-57.11, -21.4) * mm, "end": v(-57.13, -21.07) * mm});
            skArc(sketch, "E14.15.11", {"start": v(-57.45, -20.18) * mm, "mid": v(-57.65, -19.92) * mm, "end": v(-57.95, -19.79) * mm});
            skLineSegment(sketch, "E14.15.12", {"start": v(-57.45, -20.18) * mm, "end": v(-57.28, -20.62) * mm});
            skLineSegment(sketch, "E14.15.13", {"start": v(-57.13, -21.07) * mm, "end": v(-57.28, -20.62) * mm});
            skArc(sketch, "E14.15.14", {"start": v(-59.14, -23.41) * mm, "mid": v(-59.04, -23.37) * mm, "end": v(-58.95, -23.3) * mm});
            skArc(sketch, "E14.15.15", {"start": v(-60.28, -19.62) * mm, "mid": v(-60.39, -19.63) * mm, "end": v(-60.5, -19.66) * mm});
            skArc(sketch, "E14.16.0", {"start": v(-57.32, -31.45) * mm, "mid": v(-57.64, -31.83) * mm, "end": v(-57.59, -32.32) * mm});
            skArc(sketch, "E14.16.1", {"start": v(-60, -27.6) * mm, "mid": v(-59.63, -27.93) * mm, "end": v(-59.13, -27.9) * mm});
            skLineSegment(sketch, "E14.16.2", {"start": v(-57.55, -27.09) * mm, "end": v(-59.13, -27.9) * mm});
            skLineSegment(sketch, "E14.16.3", {"start": v(-55.74, -30.64) * mm, "end": v(-57.32, -31.45) * mm});
            skArc(sketch, "E14.16.4", {"start": v(-55.57, -30.51) * mm, "mid": v(-54.8, -29.63) * mm, "end": v(-54.1, -28.7) * mm});
            skPoint(sketch, "E14.16.5", {"position": v(-53.89, -28.4) * mm});
            skArc(sketch, "E14.16.6", {"start": v(-57.35, -27.02) * mm, "mid": v(-56.18, -26.92) * mm, "end": v(-55.01, -26.9) * mm});
            skPoint(sketch, "E14.16.7", {"position": v(-57.46, -27.04) * mm});
            skPoint(sketch, "E14.16.8", {"position": v(-55.65, -30.6) * mm});
            skPoint(sketch, "E14.16.9", {"position": v(-54.64, -26.9) * mm});
            skArc(sketch, "E14.16.10", {"start": v(-54.1, -28.7) * mm, "mid": v(-53.98, -28.39) * mm, "end": v(-54.04, -28.06) * mm});
            skArc(sketch, "E14.16.11", {"start": v(-54.47, -27.22) * mm, "mid": v(-54.7, -26.99) * mm, "end": v(-55.01, -26.9) * mm});
            skLineSegment(sketch, "E14.16.12", {"start": v(-54.47, -27.22) * mm, "end": v(-54.24, -27.64) * mm});
            skLineSegment(sketch, "E14.16.13", {"start": v(-54.04, -28.06) * mm, "end": v(-54.24, -27.64) * mm});
            skArc(sketch, "E14.16.14", {"start": v(-55.74, -30.64) * mm, "mid": v(-55.65, -30.58) * mm, "end": v(-55.57, -30.51) * mm});
            skArc(sketch, "E14.16.15", {"start": v(-57.35, -27.02) * mm, "mid": v(-57.45, -27.05) * mm, "end": v(-57.55, -27.09) * mm});
            skArc(sketch, "E14.17.0", {"start": v(-52.93, -38.38) * mm, "mid": v(-53.2, -38.8) * mm, "end": v(-53.08, -39.29) * mm});
            skArc(sketch, "E14.17.1", {"start": v(-56.07, -34.9) * mm, "mid": v(-55.66, -35.18) * mm, "end": v(-55.17, -35.08) * mm});
            skLineSegment(sketch, "E14.17.2", {"start": v(-53.7, -34.09) * mm, "end": v(-55.17, -35.08) * mm});
            skLineSegment(sketch, "E14.17.3", {"start": v(-51.46, -37.39) * mm, "end": v(-52.93, -38.38) * mm});
            skArc(sketch, "E14.17.4", {"start": v(-51.3, -37.23) * mm, "mid": v(-50.65, -36.27) * mm, "end": v(-50.07, -35.25) * mm});
            skPoint(sketch, "E14.17.5", {"position": v(-49.9, -34.92) * mm});
            skArc(sketch, "E14.17.6", {"start": v(-53.5, -34) * mm, "mid": v(-52.37, -33.74) * mm, "end": v(-51.2, -33.58) * mm});
            skPoint(sketch, "E14.17.7", {"position": v(-53.61, -34.03) * mm});
            skPoint(sketch, "E14.17.8", {"position": v(-51.37, -37.32) * mm});
            skPoint(sketch, "E14.17.9", {"position": v(-50.84, -33.54) * mm});
            skArc(sketch, "E14.17.10", {"start": v(-50.07, -35.25) * mm, "mid": v(-50, -34.93) * mm, "end": v(-50.1, -34.62) * mm});
            skArc(sketch, "E14.17.11", {"start": v(-50.63, -33.84) * mm, "mid": v(-50.88, -33.63) * mm, "end": v(-51.2, -33.58) * mm});
            skLineSegment(sketch, "E14.17.12", {"start": v(-50.63, -33.84) * mm, "end": v(-50.35, -34.22) * mm});
            skLineSegment(sketch, "E14.17.13", {"start": v(-50.1, -34.62) * mm, "end": v(-50.35, -34.22) * mm});
            skArc(sketch, "E14.17.14", {"start": v(-51.46, -37.39) * mm, "mid": v(-51.38, -37.32) * mm, "end": v(-51.3, -37.23) * mm});
            skArc(sketch, "E14.17.15", {"start": v(-53.5, -34) * mm, "mid": v(-53.6, -34.03) * mm, "end": v(-53.7, -34.09) * mm});
            skArc(sketch, "E14.18.0", {"start": v(-47.7, -44.71) * mm, "mid": v(-47.92, -45.16) * mm, "end": v(-47.74, -45.63) * mm});
            skArc(sketch, "E14.18.1", {"start": v(-51.25, -41.65) * mm, "mid": v(-50.81, -41.88) * mm, "end": v(-50.34, -41.72) * mm});
            skLineSegment(sketch, "E14.18.2", {"start": v(-49, -40.55) * mm, "end": v(-50.34, -41.72) * mm});
            skLineSegment(sketch, "E14.18.3", {"start": v(-46.37, -43.54) * mm, "end": v(-47.7, -44.71) * mm});
            skArc(sketch, "E14.18.4", {"start": v(-46.24, -43.37) * mm, "mid": v(-45.7, -42.33) * mm, "end": v(-45.26, -41.25) * mm});
            skPoint(sketch, "E14.18.5", {"position": v(-45.13, -40.9) * mm});
            skArc(sketch, "E14.18.6", {"start": v(-48.82, -40.43) * mm, "mid": v(-47.72, -40.04) * mm, "end": v(-46.6, -39.73) * mm});
            skPoint(sketch, "E14.18.7", {"position": v(-48.93, -40.48) * mm});
            skPoint(sketch, "E14.18.8", {"position": v(-46.29, -43.47) * mm});
            skPoint(sketch, "E14.18.9", {"position": v(-46.24, -39.65) * mm});
            skArc(sketch, "E14.18.10", {"start": v(-45.26, -41.25) * mm, "mid": v(-45.23, -40.92) * mm, "end": v(-45.36, -40.62) * mm});
            skArc(sketch, "E14.18.11", {"start": v(-45.99, -39.91) * mm, "mid": v(-46.27, -39.74) * mm, "end": v(-46.6, -39.73) * mm});
            skLineSegment(sketch, "E14.18.12", {"start": v(-45.99, -39.91) * mm, "end": v(-45.66, -40.26) * mm});
            skLineSegment(sketch, "E14.18.13", {"start": v(-45.36, -40.62) * mm, "end": v(-45.66, -40.26) * mm});
            skArc(sketch, "E14.18.14", {"start": v(-46.37, -43.54) * mm, "mid": v(-46.3, -43.46) * mm, "end": v(-46.24, -43.37) * mm});
            skArc(sketch, "E14.18.15", {"start": v(-48.82, -40.43) * mm, "mid": v(-48.92, -40.48) * mm, "end": v(-49, -40.55) * mm});
            skArc(sketch, "E14.19.0", {"start": v(-41.72, -50.34) * mm, "mid": v(-41.88, -50.81) * mm, "end": v(-41.65, -51.25) * mm});
            skArc(sketch, "E14.19.1", {"start": v(-45.63, -47.74) * mm, "mid": v(-45.16, -47.92) * mm, "end": v(-44.71, -47.7) * mm});
            skLineSegment(sketch, "E14.19.2", {"start": v(-43.54, -46.37) * mm, "end": v(-44.71, -47.7) * mm});
            skLineSegment(sketch, "E14.19.3", {"start": v(-40.55, -49) * mm, "end": v(-41.72, -50.34) * mm});
            skArc(sketch, "E14.19.4", {"start": v(-40.43, -48.82) * mm, "mid": v(-40.04, -47.72) * mm, "end": v(-39.73, -46.6) * mm});
            skPoint(sketch, "E14.19.5", {"position": v(-39.65, -46.24) * mm});
            skArc(sketch, "E14.19.6", {"start": v(-43.37, -46.24) * mm, "mid": v(-42.33, -45.7) * mm, "end": v(-41.25, -45.26) * mm});
            skPoint(sketch, "E14.19.7", {"position": v(-43.47, -46.29) * mm});
            skPoint(sketch, "E14.19.8", {"position": v(-40.48, -48.93) * mm});
            skPoint(sketch, "E14.19.9", {"position": v(-40.9, -45.13) * mm});
            skArc(sketch, "E14.19.10", {"start": v(-39.73, -46.6) * mm, "mid": v(-39.74, -46.27) * mm, "end": v(-39.91, -45.99) * mm});
            skArc(sketch, "E14.19.11", {"start": v(-40.62, -45.36) * mm, "mid": v(-40.92, -45.23) * mm, "end": v(-41.25, -45.26) * mm});
            skLineSegment(sketch, "E14.19.12", {"start": v(-40.62, -45.36) * mm, "end": v(-40.26, -45.66) * mm});
            skLineSegment(sketch, "E14.19.13", {"start": v(-39.91, -45.99) * mm, "end": v(-40.26, -45.66) * mm});
            skArc(sketch, "E14.19.14", {"start": v(-40.55, -49) * mm, "mid": v(-40.48, -48.92) * mm, "end": v(-40.43, -48.82) * mm});
            skArc(sketch, "E14.19.15", {"start": v(-43.37, -46.24) * mm, "mid": v(-43.46, -46.3) * mm, "end": v(-43.54, -46.37) * mm});
            skArc(sketch, "E14.20.0", {"start": v(-35.08, -55.17) * mm, "mid": v(-35.18, -55.66) * mm, "end": v(-34.9, -56.07) * mm});
            skArc(sketch, "E14.20.1", {"start": v(-39.29, -53.08) * mm, "mid": v(-38.8, -53.2) * mm, "end": v(-38.38, -52.93) * mm});
            skLineSegment(sketch, "E14.20.2", {"start": v(-37.39, -51.46) * mm, "end": v(-38.38, -52.93) * mm});
            skLineSegment(sketch, "E14.20.3", {"start": v(-34.09, -53.7) * mm, "end": v(-35.08, -55.17) * mm});
            skArc(sketch, "E14.20.4", {"start": v(-34, -53.5) * mm, "mid": v(-33.74, -52.37) * mm, "end": v(-33.58, -51.2) * mm});
            skPoint(sketch, "E14.20.5", {"position": v(-33.54, -50.84) * mm});
            skArc(sketch, "E14.20.6", {"start": v(-37.23, -51.3) * mm, "mid": v(-36.27, -50.65) * mm, "end": v(-35.25, -50.07) * mm});
            skPoint(sketch, "E14.20.7", {"position": v(-37.32, -51.37) * mm});
            skPoint(sketch, "E14.20.8", {"position": v(-34.03, -53.61) * mm});
            skPoint(sketch, "E14.20.9", {"position": v(-34.92, -49.9) * mm});
            skArc(sketch, "E14.20.10", {"start": v(-33.58, -51.2) * mm, "mid": v(-33.63, -50.88) * mm, "end": v(-33.84, -50.63) * mm});
            skArc(sketch, "E14.20.11", {"start": v(-34.62, -50.1) * mm, "mid": v(-34.93, -50) * mm, "end": v(-35.25, -50.07) * mm});
            skLineSegment(sketch, "E14.20.12", {"start": v(-34.62, -50.1) * mm, "end": v(-34.22, -50.35) * mm});
            skLineSegment(sketch, "E14.20.13", {"start": v(-33.84, -50.63) * mm, "end": v(-34.22, -50.35) * mm});
            skArc(sketch, "E14.20.14", {"start": v(-34.09, -53.7) * mm, "mid": v(-34.03, -53.6) * mm, "end": v(-34, -53.5) * mm});
            skArc(sketch, "E14.20.15", {"start": v(-37.23, -51.3) * mm, "mid": v(-37.32, -51.38) * mm, "end": v(-37.39, -51.46) * mm});
            skArc(sketch, "E14.21.0", {"start": v(-27.9, -59.13) * mm, "mid": v(-27.93, -59.63) * mm, "end": v(-27.6, -60) * mm});
            skArc(sketch, "E14.21.1", {"start": v(-32.32, -57.59) * mm, "mid": v(-31.83, -57.64) * mm, "end": v(-31.45, -57.32) * mm});
            skLineSegment(sketch, "E14.21.2", {"start": v(-30.64, -55.74) * mm, "end": v(-31.45, -57.32) * mm});
            skLineSegment(sketch, "E14.21.3", {"start": v(-27.09, -57.55) * mm, "end": v(-27.9, -59.13) * mm});
            skArc(sketch, "E14.21.4", {"start": v(-27.02, -57.35) * mm, "mid": v(-26.92, -56.18) * mm, "end": v(-26.9, -55.01) * mm});
            skPoint(sketch, "E14.21.5", {"position": v(-26.9, -54.64) * mm});
            skArc(sketch, "E14.21.6", {"start": v(-30.51, -55.57) * mm, "mid": v(-29.63, -54.8) * mm, "end": v(-28.7, -54.1) * mm});
            skPoint(sketch, "E14.21.7", {"position": v(-30.6, -55.65) * mm});
            skPoint(sketch, "E14.21.8", {"position": v(-27.04, -57.46) * mm});
            skPoint(sketch, "E14.21.9", {"position": v(-28.4, -53.89) * mm});
            skArc(sketch, "E14.21.10", {"start": v(-26.9, -55.01) * mm, "mid": v(-26.99, -54.7) * mm, "end": v(-27.22, -54.47) * mm});
            skArc(sketch, "E14.21.11", {"start": v(-28.06, -54.04) * mm, "mid": v(-28.39, -53.98) * mm, "end": v(-28.7, -54.1) * mm});
            skLineSegment(sketch, "E14.21.12", {"start": v(-28.06, -54.04) * mm, "end": v(-27.64, -54.24) * mm});
            skLineSegment(sketch, "E14.21.13", {"start": v(-27.22, -54.47) * mm, "end": v(-27.64, -54.24) * mm});
            skArc(sketch, "E14.21.14", {"start": v(-27.09, -57.55) * mm, "mid": v(-27.05, -57.45) * mm, "end": v(-27.02, -57.35) * mm});
            skArc(sketch, "E14.21.15", {"start": v(-30.51, -55.57) * mm, "mid": v(-30.58, -55.65) * mm, "end": v(-30.64, -55.74) * mm});
            skArc(sketch, "E14.22.0", {"start": v(-20.26, -62.16) * mm, "mid": v(-20.23, -62.66) * mm, "end": v(-19.85, -62.98) * mm});
            skArc(sketch, "E14.22.1", {"start": v(-24.85, -61.19) * mm, "mid": v(-24.35, -61.18) * mm, "end": v(-24.01, -60.81) * mm});
            skLineSegment(sketch, "E14.22.2", {"start": v(-23.41, -59.14) * mm, "end": v(-24.01, -60.81) * mm});
            skLineSegment(sketch, "E14.22.3", {"start": v(-19.66, -60.5) * mm, "end": v(-20.26, -62.16) * mm});
            skArc(sketch, "E14.22.4", {"start": v(-19.62, -60.28) * mm, "mid": v(-19.66, -59.11) * mm, "end": v(-19.79, -57.95) * mm});
            skPoint(sketch, "E14.22.5", {"position": v(-19.84, -57.58) * mm});
            skArc(sketch, "E14.22.6", {"start": v(-23.3, -58.95) * mm, "mid": v(-22.53, -58.08) * mm, "end": v(-21.7, -57.26) * mm});
            skPoint(sketch, "E14.22.7", {"position": v(-23.38, -59.04) * mm});
            skPoint(sketch, "E14.22.8", {"position": v(-19.62, -60.4) * mm});
            skPoint(sketch, "E14.22.9", {"position": v(-21.42, -57.02) * mm});
            skArc(sketch, "E14.22.10", {"start": v(-19.79, -57.95) * mm, "mid": v(-19.92, -57.65) * mm, "end": v(-20.18, -57.45) * mm});
            skArc(sketch, "E14.22.11", {"start": v(-21.07, -57.13) * mm, "mid": v(-21.4, -57.11) * mm, "end": v(-21.7, -57.26) * mm});
            skLineSegment(sketch, "E14.22.12", {"start": v(-21.07, -57.13) * mm, "end": v(-20.62, -57.28) * mm});
            skLineSegment(sketch, "E14.22.13", {"start": v(-20.18, -57.45) * mm, "end": v(-20.62, -57.28) * mm});
            skArc(sketch, "E14.22.14", {"start": v(-19.66, -60.5) * mm, "mid": v(-19.63, -60.39) * mm, "end": v(-19.62, -60.28) * mm});
            skArc(sketch, "E14.22.15", {"start": v(-23.3, -58.95) * mm, "mid": v(-23.37, -59.04) * mm, "end": v(-23.41, -59.14) * mm});
            skArc(sketch, "E14.23.0", {"start": v(-12.3, -64.21) * mm, "mid": v(-12.22, -64.7) * mm, "end": v(-11.8, -64.98) * mm});
            skArc(sketch, "E14.23.1", {"start": v(-16.99, -63.82) * mm, "mid": v(-16.5, -63.75) * mm, "end": v(-16.2, -63.34) * mm});
            skLineSegment(sketch, "E14.23.2", {"start": v(-15.82, -61.61) * mm, "end": v(-16.2, -63.34) * mm});
            skLineSegment(sketch, "E14.23.3", {"start": v(-11.92, -62.48) * mm, "end": v(-12.3, -64.21) * mm});
            skArc(sketch, "E14.23.4", {"start": v(-11.91, -62.27) * mm, "mid": v(-12.1, -61.11) * mm, "end": v(-12.37, -59.97) * mm});
            skPoint(sketch, "E14.23.5", {"position": v(-12.47, -59.62) * mm});
            skArc(sketch, "E14.23.6", {"start": v(-15.73, -61.41) * mm, "mid": v(-15.07, -60.45) * mm, "end": v(-14.34, -59.53) * mm});
            skPoint(sketch, "E14.23.7", {"position": v(-15.8, -61.5) * mm});
            skPoint(sketch, "E14.23.8", {"position": v(-11.9, -62.38) * mm});
            skPoint(sketch, "E14.23.9", {"position": v(-14.1, -59.25) * mm});
            skArc(sketch, "E14.23.10", {"start": v(-12.37, -59.97) * mm, "mid": v(-12.54, -59.69) * mm, "end": v(-12.82, -59.53) * mm});
            skArc(sketch, "E14.23.11", {"start": v(-13.74, -59.32) * mm, "mid": v(-14.07, -59.35) * mm, "end": v(-14.34, -59.53) * mm});
            skLineSegment(sketch, "E14.23.12", {"start": v(-13.74, -59.32) * mm, "end": v(-13.28, -59.41) * mm});
            skLineSegment(sketch, "E14.23.13", {"start": v(-12.82, -59.53) * mm, "end": v(-13.28, -59.41) * mm});
            skArc(sketch, "E14.23.14", {"start": v(-11.92, -62.48) * mm, "mid": v(-11.9, -62.37) * mm, "end": v(-11.91, -62.27) * mm});
            skArc(sketch, "E14.23.15", {"start": v(-15.73, -61.41) * mm, "mid": v(-15.78, -61.5) * mm, "end": v(-15.82, -61.61) * mm});
            skArc(sketch, "E14.24.0", {"start": v(-4.16, -65.25) * mm, "mid": v(-4.01, -65.72) * mm, "end": v(-3.57, -65.94) * mm});
            skArc(sketch, "E14.24.1", {"start": v(-8.85, -65.44) * mm, "mid": v(-8.37, -65.31) * mm, "end": v(-8.14, -64.87) * mm});
            skLineSegment(sketch, "E14.24.2", {"start": v(-7.97, -63.1) * mm, "end": v(-8.14, -64.87) * mm});
            skLineSegment(sketch, "E14.24.3", {"start": v(-4, -63.48) * mm, "end": v(-4.16, -65.25) * mm});
            skArc(sketch, "E14.24.4", {"start": v(-4.01, -63.27) * mm, "mid": v(-4.34, -62.15) * mm, "end": v(-4.75, -61.05) * mm});
            skPoint(sketch, "E14.24.5", {"position": v(-4.9, -60.71) * mm});
            skArc(sketch, "E14.24.6", {"start": v(-7.91, -62.9) * mm, "mid": v(-7.38, -61.86) * mm, "end": v(-6.77, -60.86) * mm});
            skPoint(sketch, "E14.24.7", {"position": v(-7.96, -63) * mm});
            skPoint(sketch, "E14.24.8", {"position": v(-3.99, -63.37) * mm});
            skPoint(sketch, "E14.24.9", {"position": v(-6.56, -60.55) * mm});
            skArc(sketch, "E14.24.10", {"start": v(-4.75, -61.05) * mm, "mid": v(-4.96, -60.8) * mm, "end": v(-5.26, -60.67) * mm});
            skArc(sketch, "E14.24.11", {"start": v(-6.2, -60.58) * mm, "mid": v(-6.52, -60.64) * mm, "end": v(-6.77, -60.86) * mm});
            skLineSegment(sketch, "E14.24.12", {"start": v(-6.2, -60.58) * mm, "end": v(-5.73, -60.6) * mm});
            skLineSegment(sketch, "E14.24.13", {"start": v(-5.26, -60.67) * mm, "end": v(-5.73, -60.6) * mm});
            skArc(sketch, "E14.24.14", {"start": v(-4, -63.48) * mm, "mid": v(-4, -63.37) * mm, "end": v(-4.01, -63.27) * mm});
            skArc(sketch, "E14.24.15", {"start": v(-7.91, -62.9) * mm, "mid": v(-7.95, -63) * mm, "end": v(-7.97, -63.1) * mm});
            skArc(sketch, "E14.25.0", {"start": v(4.05, -65.26) * mm, "mid": v(4.26, -65.7) * mm, "end": v(4.73, -65.87) * mm});
            skArc(sketch, "E14.25.1", {"start": v(-0.58, -66.04) * mm, "mid": v(-0.12, -65.85) * mm, "end": v(0.06, -65.38) * mm});
            skLineSegment(sketch, "E14.25.2", {"start": v(0, -63.6) * mm, "end": v(0.06, -65.38) * mm});
            skLineSegment(sketch, "E14.25.3", {"start": v(4, -63.48) * mm, "end": v(4.05, -65.26) * mm});
            skArc(sketch, "E14.25.4", {"start": v(3.95, -63.27) * mm, "mid": v(3.48, -62.2) * mm, "end": v(2.94, -61.17) * mm});
            skPoint(sketch, "E14.25.5", {"position": v(2.75, -60.85) * mm});
            skArc(sketch, "E14.25.6", {"start": v(0.03, -63.4) * mm, "mid": v(0.43, -62.3) * mm, "end": v(0.91, -61.23) * mm});
            skPoint(sketch, "E14.25.7", {"position": v(0, -63.5) * mm});
            skPoint(sketch, "E14.25.8", {"position": v(3.99, -63.37) * mm});
            skPoint(sketch, "E14.25.9", {"position": v(1.08, -60.9) * mm});
            skArc(sketch, "E14.25.10", {"start": v(2.94, -61.17) * mm, "mid": v(2.7, -60.93) * mm, "end": v(2.38, -60.85) * mm});
            skArc(sketch, "E14.25.11", {"start": v(1.44, -60.88) * mm, "mid": v(1.13, -60.98) * mm, "end": v(0.91, -61.23) * mm});
            skLineSegment(sketch, "E14.25.12", {"start": v(1.44, -60.88) * mm, "end": v(1.91, -60.85) * mm});
            skLineSegment(sketch, "E14.25.13", {"start": v(2.38, -60.85) * mm, "end": v(1.91, -60.85) * mm});
            skArc(sketch, "E14.25.14", {"start": v(4, -63.48) * mm, "mid": v(3.98, -63.38) * mm, "end": v(3.95, -63.27) * mm});
            skArc(sketch, "E14.25.15", {"start": v(0.03, -63.4) * mm, "mid": v(0, -63.5) * mm, "end": v(0, -63.6) * mm});
            skArc(sketch, "E14.26.0", {"start": v(12.2, -64.24) * mm, "mid": v(12.46, -64.66) * mm, "end": v(12.95, -64.76) * mm});
            skArc(sketch, "E14.26.1", {"start": v(7.7, -65.59) * mm, "mid": v(8.13, -65.34) * mm, "end": v(8.25, -64.86) * mm});
            skLineSegment(sketch, "E14.26.2", {"start": v(7.98, -63.1) * mm, "end": v(8.25, -64.86) * mm});
            skLineSegment(sketch, "E14.26.3", {"start": v(11.92, -62.48) * mm, "end": v(12.2, -64.24) * mm});
            skArc(sketch, "E14.26.4", {"start": v(11.85, -62.28) * mm, "mid": v(11.25, -61.27) * mm, "end": v(10.58, -60.31) * mm});
            skPoint(sketch, "E14.26.5", {"position": v(10.35, -60.02) * mm});
            skArc(sketch, "E14.26.6", {"start": v(7.98, -62.9) * mm, "mid": v(8.24, -61.75) * mm, "end": v(8.58, -60.63) * mm});
            skPoint(sketch, "E14.26.7", {"position": v(7.96, -63) * mm});
            skPoint(sketch, "E14.26.8", {"position": v(11.9, -62.38) * mm});
            skPoint(sketch, "E14.26.9", {"position": v(8.7, -60.28) * mm});
            skArc(sketch, "E14.26.10", {"start": v(10.58, -60.31) * mm, "mid": v(10.32, -60.11) * mm, "end": v(10, -60.07) * mm});
            skArc(sketch, "E14.26.11", {"start": v(9.06, -60.22) * mm, "mid": v(8.76, -60.36) * mm, "end": v(8.58, -60.63) * mm});
            skLineSegment(sketch, "E14.26.12", {"start": v(9.06, -60.22) * mm, "end": v(9.52, -60.13) * mm});
            skLineSegment(sketch, "E14.26.13", {"start": v(10, -60.07) * mm, "end": v(9.52, -60.13) * mm});
            skArc(sketch, "E14.26.14", {"start": v(11.92, -62.48) * mm, "mid": v(11.89, -62.38) * mm, "end": v(11.85, -62.28) * mm});
            skArc(sketch, "E14.26.15", {"start": v(7.98, -62.9) * mm, "mid": v(7.97, -63) * mm, "end": v(7.98, -63.1) * mm});
            skArc(sketch, "E14.27.0", {"start": v(20.15, -62.2) * mm, "mid": v(20.46, -62.59) * mm, "end": v(20.96, -62.63) * mm});
            skArc(sketch, "E14.27.1", {"start": v(15.86, -64.1) * mm, "mid": v(16.26, -63.8) * mm, "end": v(16.32, -63.31) * mm});
            skLineSegment(sketch, "E14.27.2", {"start": v(15.82, -61.6) * mm, "end": v(16.32, -63.31) * mm});
            skLineSegment(sketch, "E14.27.3", {"start": v(19.65, -60.5) * mm, "end": v(20.15, -62.2) * mm});
            skArc(sketch, "E14.27.4", {"start": v(19.56, -60.3) * mm, "mid": v(18.84, -59.38) * mm, "end": v(18.05, -58.51) * mm});
            skPoint(sketch, "E14.27.5", {"position": v(17.8, -58.25) * mm});
            skArc(sketch, "E14.27.6", {"start": v(15.8, -61.4) * mm, "mid": v(15.91, -60.23) * mm, "end": v(16.1, -59.08) * mm});
            skPoint(sketch, "E14.27.7", {"position": v(15.8, -61.5) * mm});
            skPoint(sketch, "E14.27.8", {"position": v(19.62, -60.4) * mm});
            skPoint(sketch, "E14.27.9", {"position": v(16.19, -58.72) * mm});
            skArc(sketch, "E14.27.10", {"start": v(18.05, -58.51) * mm, "mid": v(17.77, -58.35) * mm, "end": v(17.44, -58.34) * mm});
            skArc(sketch, "E14.27.11", {"start": v(16.53, -58.6) * mm, "mid": v(16.26, -58.78) * mm, "end": v(16.1, -59.08) * mm});
            skLineSegment(sketch, "E14.27.12", {"start": v(16.53, -58.6) * mm, "end": v(16.98, -58.46) * mm});
            skLineSegment(sketch, "E14.27.13", {"start": v(17.44, -58.34) * mm, "end": v(16.98, -58.46) * mm});
            skArc(sketch, "E14.27.14", {"start": v(19.65, -60.5) * mm, "mid": v(19.61, -60.4) * mm, "end": v(19.56, -60.3) * mm});
            skArc(sketch, "E14.27.15", {"start": v(15.8, -61.4) * mm, "mid": v(15.8, -61.5) * mm, "end": v(15.82, -61.6) * mm});
            skArc(sketch, "E14.28.0", {"start": v(27.78, -59.19) * mm, "mid": v(28.15, -59.53) * mm, "end": v(28.64, -59.5) * mm});
            skArc(sketch, "E14.28.1", {"start": v(23.77, -61.61) * mm, "mid": v(24.13, -61.27) * mm, "end": v(24.12, -60.77) * mm});
            skLineSegment(sketch, "E14.28.2", {"start": v(23.42, -59.14) * mm, "end": v(24.12, -60.77) * mm});
            skLineSegment(sketch, "E14.28.3", {"start": v(27.08, -57.56) * mm, "end": v(27.78, -59.19) * mm});
            skArc(sketch, "E14.28.4", {"start": v(26.96, -57.38) * mm, "mid": v(26.13, -56.55) * mm, "end": v(25.25, -55.79) * mm});
            skPoint(sketch, "E14.28.5", {"position": v(24.95, -55.56) * mm});
            skArc(sketch, "E14.28.6", {"start": v(23.37, -58.93) * mm, "mid": v(23.33, -57.76) * mm, "end": v(23.39, -56.6) * mm});
            skPoint(sketch, "E14.28.7", {"position": v(23.38, -59.04) * mm});
            skPoint(sketch, "E14.28.8", {"position": v(27.04, -57.46) * mm});
            skPoint(sketch, "E14.28.9", {"position": v(23.42, -56.23) * mm});
            skArc(sketch, "E14.28.10", {"start": v(25.25, -55.79) * mm, "mid": v(24.94, -55.66) * mm, "end": v(24.62, -55.7) * mm});
            skArc(sketch, "E14.28.11", {"start": v(23.75, -56.07) * mm, "mid": v(23.5, -56.28) * mm, "end": v(23.39, -56.6) * mm});
            skLineSegment(sketch, "E14.28.12", {"start": v(23.75, -56.07) * mm, "end": v(24.18, -55.87) * mm});
            skLineSegment(sketch, "E14.28.13", {"start": v(24.62, -55.7) * mm, "end": v(24.18, -55.87) * mm});
            skArc(sketch, "E14.28.14", {"start": v(27.08, -57.56) * mm, "mid": v(27.03, -57.46) * mm, "end": v(26.96, -57.38) * mm});
            skArc(sketch, "E14.28.15", {"start": v(23.37, -58.93) * mm, "mid": v(23.38, -59.04) * mm, "end": v(23.42, -59.14) * mm});
            skArc(sketch, "E14.29.0", {"start": v(34.98, -55.24) * mm, "mid": v(35.38, -55.53) * mm, "end": v(35.88, -55.45) * mm});
            skArc(sketch, "E14.29.1", {"start": v(31.3, -58.15) * mm, "mid": v(31.62, -57.76) * mm, "end": v(31.55, -57.27) * mm});
            skLineSegment(sketch, "E14.29.2", {"start": v(30.65, -55.74) * mm, "end": v(31.55, -57.27) * mm});
            skLineSegment(sketch, "E14.29.3", {"start": v(34.08, -53.7) * mm, "end": v(34.98, -55.24) * mm});
            skArc(sketch, "E14.29.4", {"start": v(33.94, -53.54) * mm, "mid": v(33.01, -52.83) * mm, "end": v(32.04, -52.19) * mm});
            skPoint(sketch, "E14.29.5", {"position": v(31.72, -52) * mm});
            skArc(sketch, "E14.29.6", {"start": v(30.57, -55.54) * mm, "mid": v(30.39, -54.38) * mm, "end": v(30.3, -53.22) * mm});
            skPoint(sketch, "E14.29.7", {"position": v(30.6, -55.65) * mm});
            skPoint(sketch, "E14.29.8", {"position": v(34.03, -53.61) * mm});
            skPoint(sketch, "E14.29.9", {"position": v(30.28, -52.85) * mm});
            skArc(sketch, "E14.29.10", {"start": v(32.04, -52.19) * mm, "mid": v(31.72, -52.1) * mm, "end": v(31.4, -52.17) * mm});
            skArc(sketch, "E14.29.11", {"start": v(30.59, -52.65) * mm, "mid": v(30.37, -52.9) * mm, "end": v(30.3, -53.22) * mm});
            skLineSegment(sketch, "E14.29.12", {"start": v(30.59, -52.65) * mm, "end": v(30.99, -52.4) * mm});
            skLineSegment(sketch, "E14.29.13", {"start": v(31.4, -52.17) * mm, "end": v(30.99, -52.4) * mm});
            skArc(sketch, "E14.29.14", {"start": v(34.08, -53.7) * mm, "mid": v(34.02, -53.62) * mm, "end": v(33.94, -53.54) * mm});
            skArc(sketch, "E14.29.15", {"start": v(30.57, -55.54) * mm, "mid": v(30.6, -55.64) * mm, "end": v(30.65, -55.74) * mm});
            skCircle(sketch, "E15", {"center": v(0, 0) * mm, "radius": 66.04 * mm});
            skArc(sketch, "E16", {"start": v(-8.3, 70.64) * mm, "mid": v(3.72, -71.02) * mm, "end": v(0.86, 71.11) * mm});
            skArc(sketch, "E17", {"start": v(-0.07, 76.33) * mm, "mid": v(-1.76, 78.82) * mm, "end": v(-3.82, 81.02) * mm});
            skLineSegment(sketch, "E18", {"start": v(-4.24, 81.18) * mm, "end": v(-4.25, 81.18) * mm});
            skLineSegment(sketch, "E19", {"start": v(0, 76.05) * mm, "end": v(0.23, 71.72) * mm});
            skLineSegment(sketch, "E20.MirrorCS", {"start": v(-4.26, 81.18) * mm, "end": v(-4.25, 81.18) * mm});
            skArc(sketch, "E21.MirrorCS", {"start": v(-7.9, 75.92) * mm, "mid": v(-6.49, 78.57) * mm, "end": v(-4.67, 80.97) * mm});
            skLineSegment(sketch, "E22.MirrorCS", {"start": v(-7.96, 75.63) * mm, "end": v(-7.73, 71.3) * mm});
            skPoint(sketch, "E23.visualSharp", {"position": v(0, 76.2) * mm});
            skArc(sketch, "E23.filletArc", {"start": v(0, 76.05) * mm, "mid": v(-0.02, 76.2) * mm, "end": v(-0.07, 76.33) * mm});
            skPoint(sketch, "E24.visualSharp", {"position": v(-7.97, 75.78) * mm});
            skArc(sketch, "E24.filletArc", {"start": v(-7.9, 75.92) * mm, "mid": v(-7.95, 75.78) * mm, "end": v(-7.96, 75.63) * mm});
            skPoint(sketch, "E25.visualSharp", {"position": v(-4, 81.18) * mm});
            skArc(sketch, "E25.filletArc", {"start": v(-3.82, 81.02) * mm, "mid": v(-4.02, 81.14) * mm, "end": v(-4.24, 81.18) * mm});
            skPoint(sketch, "E26.visualSharp", {"position": v(-4.5, 81.15) * mm});
            skArc(sketch, "E26.filletArc", {"start": v(-4.26, 81.18) * mm, "mid": v(-4.49, 81.11) * mm, "end": v(-4.67, 80.97) * mm});
            skPoint(sketch, "E27.visualSharp", {"position": v(-7.7, 70.7) * mm});
            skArc(sketch, "E27.filletArc", {"start": v(-8.3, 70.64) * mm, "mid": v(-7.88, 70.86) * mm, "end": v(-7.73, 71.3) * mm});
            skPoint(sketch, "E28.visualSharp", {"position": v(0.27, 71.12) * mm});
            skArc(sketch, "E28.filletArc", {"start": v(0.23, 71.72) * mm, "mid": v(0.43, 71.3) * mm, "end": v(0.86, 71.11) * mm});
            skArc(sketch, "E29.1.0", {"start": v(-22.8, 67.37) * mm, "mid": v(-22.44, 67.67) * mm, "end": v(-22.39, 68.13) * mm});
            skLineSegment(sketch, "E29.1.1", {"start": v(-23.5, 72.33) * mm, "end": v(-22.39, 68.13) * mm});
            skLineSegment(sketch, "E29.1.2", {"start": v(-15.8, 74.4) * mm, "end": v(-14.68, 70.2) * mm});
            skPoint(sketch, "E29.1.3", {"position": v(-20.8, 78.58) * mm});
            skPoint(sketch, "E29.1.4", {"position": v(-23.55, 72.47) * mm});
            skPoint(sketch, "E29.1.5", {"position": v(-21.28, 78.44) * mm});
            skArc(sketch, "E29.1.6", {"start": v(-23.52, 72.62) * mm, "mid": v(-22.68, 75.5) * mm, "end": v(-21.4, 78.23) * mm});
            skPoint(sketch, "E29.1.7", {"position": v(-15.84, 74.53) * mm});
            skArc(sketch, "E29.1.8", {"start": v(-15.94, 74.65) * mm, "mid": v(-18.1, 76.73) * mm, "end": v(-20.58, 78.45) * mm});
            skArc(sketch, "E29.1.9", {"start": v(-20.58, 78.45) * mm, "mid": v(-20.8, 78.53) * mm, "end": v(-21.03, 78.52) * mm});
            skArc(sketch, "E29.1.10", {"start": v(-21.05, 78.52) * mm, "mid": v(-21.25, 78.4) * mm, "end": v(-21.4, 78.23) * mm});
            skArc(sketch, "E29.1.11", {"start": v(-15.8, 74.4) * mm, "mid": v(-15.86, 74.53) * mm, "end": v(-15.94, 74.65) * mm});
            skArc(sketch, "E29.1.12", {"start": v(-23.52, 72.62) * mm, "mid": v(-23.53, 72.47) * mm, "end": v(-23.5, 72.33) * mm});
            skLineSegment(sketch, "E29.1.13", {"start": v(-21.03, 78.52) * mm, "end": v(-21.04, 78.52) * mm});
            skLineSegment(sketch, "E29.1.14", {"start": v(-21.05, 78.52) * mm, "end": v(-21.04, 78.52) * mm});
            skArc(sketch, "E29.2.0", {"start": v(-36.3, 61.16) * mm, "mid": v(-36.02, 61.53) * mm, "end": v(-36.06, 62) * mm});
            skLineSegment(sketch, "E29.2.1", {"start": v(-38.03, 65.86) * mm, "end": v(-36.06, 62) * mm});
            skLineSegment(sketch, "E29.2.2", {"start": v(-30.93, 69.48) * mm, "end": v(-28.96, 65.61) * mm});
            skPoint(sketch, "E29.2.3", {"position": v(-36.67, 72.54) * mm});
            skPoint(sketch, "E29.2.4", {"position": v(-38.1, 66) * mm});
            skPoint(sketch, "E29.2.5", {"position": v(-37.13, 72.3) * mm});
            skArc(sketch, "E29.2.6", {"start": v(-38.1, 66.14) * mm, "mid": v(-37.89, 69.14) * mm, "end": v(-37.2, 72.07) * mm});
            skPoint(sketch, "E29.2.7", {"position": v(-31, 69.61) * mm});
            skArc(sketch, "E29.2.8", {"start": v(-31.11, 69.7) * mm, "mid": v(-33.67, 71.3) * mm, "end": v(-36.44, 72.46) * mm});
            skArc(sketch, "E29.2.9", {"start": v(-36.44, 72.46) * mm, "mid": v(-36.67, 72.5) * mm, "end": v(-36.9, 72.44) * mm});
            skArc(sketch, "E29.2.10", {"start": v(-36.91, 72.43) * mm, "mid": v(-37.1, 72.28) * mm, "end": v(-37.2, 72.07) * mm});
            skArc(sketch, "E29.2.11", {"start": v(-30.93, 69.48) * mm, "mid": v(-31, 69.6) * mm, "end": v(-31.11, 69.7) * mm});
            skArc(sketch, "E29.2.12", {"start": v(-38.1, 66.14) * mm, "mid": v(-38.08, 66) * mm, "end": v(-38.03, 65.86) * mm});
            skLineSegment(sketch, "E29.2.13", {"start": v(-36.9, 72.44) * mm, "end": v(-36.9, 72.43) * mm});
            skLineSegment(sketch, "E29.2.14", {"start": v(-36.91, 72.43) * mm, "end": v(-36.9, 72.43) * mm});
            skArc(sketch, "E30.1.30.0", {"start": v(41.63, -50.42) * mm, "mid": v(42.07, -50.66) * mm, "end": v(42.54, -50.51) * mm});
            skArc(sketch, "E30.4.30.0", {"start": v(38.35, -53.77) * mm, "mid": v(38.6, -53.34) * mm, "end": v(38.48, -52.86) * mm});
            skLineSegment(sketch, "E30.8.30.0", {"start": v(37.4, -51.46) * mm, "end": v(38.48, -52.86) * mm});
            skLineSegment(sketch, "E30.11.30.0", {"start": v(40.54, -49.01) * mm, "end": v(41.63, -50.42) * mm});
            skArc(sketch, "E30.14.30.0", {"start": v(40.38, -48.87) * mm, "mid": v(39.38, -48.27) * mm, "end": v(38.33, -47.76) * mm});
            skPoint(sketch, "E30.18.30.0", {"position": v(37.99, -47.61) * mm});
            skArc(sketch, "E30.19.30.0", {"start": v(37.29, -51.27) * mm, "mid": v(36.97, -50.14) * mm, "end": v(36.73, -49) * mm});
            skPoint(sketch, "E30.23.30.0", {"position": v(37.32, -51.37) * mm});
            skPoint(sketch, "E30.24.30.0", {"position": v(40.48, -48.93) * mm});
            skPoint(sketch, "E30.25.30.0", {"position": v(36.67, -48.63) * mm});
            skArc(sketch, "E30.26.30.0", {"start": v(38.33, -47.76) * mm, "mid": v(38, -47.7) * mm, "end": v(37.7, -47.82) * mm});
            skArc(sketch, "E30.30.30.0", {"start": v(36.95, -48.4) * mm, "mid": v(36.76, -48.67) * mm, "end": v(36.73, -49) * mm});
            skLineSegment(sketch, "E30.34.30.0", {"start": v(36.95, -48.4) * mm, "end": v(37.31, -48.1) * mm});
            skLineSegment(sketch, "E30.37.30.0", {"start": v(37.7, -47.82) * mm, "end": v(37.31, -48.1) * mm});
            skArc(sketch, "E30.40.30.0", {"start": v(40.54, -49.01) * mm, "mid": v(40.47, -48.93) * mm, "end": v(40.38, -48.87) * mm});
            skArc(sketch, "E30.44.30.0", {"start": v(37.29, -51.27) * mm, "mid": v(37.33, -51.37) * mm, "end": v(37.4, -51.46) * mm});
            skArc(sketch, "E30.1.31.0", {"start": v(47.62, -44.8) * mm, "mid": v(48.08, -44.99) * mm, "end": v(48.54, -44.78) * mm});
            skArc(sketch, "E30.4.31.0", {"start": v(44.78, -48.54) * mm, "mid": v(44.99, -48.08) * mm, "end": v(44.8, -47.62) * mm});
            skLineSegment(sketch, "E30.8.31.0", {"start": v(43.55, -46.37) * mm, "end": v(44.8, -47.62) * mm});
            skLineSegment(sketch, "E30.11.31.0", {"start": v(46.37, -43.55) * mm, "end": v(47.62, -44.8) * mm});
            skArc(sketch, "E30.14.31.0", {"start": v(46.19, -43.42) * mm, "mid": v(45.12, -42.96) * mm, "end": v(44.01, -42.58) * mm});
            skPoint(sketch, "E30.18.31.0", {"position": v(43.65, -42.47) * mm});
            skArc(sketch, "E30.19.31.0", {"start": v(43.42, -46.19) * mm, "mid": v(42.96, -45.12) * mm, "end": v(42.58, -44.01) * mm});
            skPoint(sketch, "E30.23.31.0", {"position": v(43.47, -46.29) * mm});
            skPoint(sketch, "E30.24.31.0", {"position": v(46.29, -43.47) * mm});
            skPoint(sketch, "E30.25.31.0", {"position": v(42.47, -43.65) * mm});
            skArc(sketch, "E30.26.31.0", {"start": v(44.01, -42.58) * mm, "mid": v(43.68, -42.57) * mm, "end": v(43.4, -42.72) * mm});
            skArc(sketch, "E30.30.31.0", {"start": v(42.72, -43.4) * mm, "mid": v(42.57, -43.68) * mm, "end": v(42.58, -44.01) * mm});
            skLineSegment(sketch, "E30.34.31.0", {"start": v(42.72, -43.4) * mm, "end": v(43.05, -43.05) * mm});
            skLineSegment(sketch, "E30.37.31.0", {"start": v(43.4, -42.72) * mm, "end": v(43.05, -43.05) * mm});
            skArc(sketch, "E30.40.31.0", {"start": v(46.37, -43.55) * mm, "mid": v(46.28, -43.48) * mm, "end": v(46.19, -43.42) * mm});
            skArc(sketch, "E30.44.31.0", {"start": v(43.42, -46.19) * mm, "mid": v(43.48, -46.28) * mm, "end": v(43.55, -46.37) * mm});
            skArc(sketch, "E30.1.32.0", {"start": v(52.86, -38.48) * mm, "mid": v(53.34, -38.6) * mm, "end": v(53.77, -38.35) * mm});
            skArc(sketch, "E30.4.32.0", {"start": v(50.51, -42.54) * mm, "mid": v(50.66, -42.07) * mm, "end": v(50.42, -41.63) * mm});
            skLineSegment(sketch, "E30.8.32.0", {"start": v(49.01, -40.54) * mm, "end": v(50.42, -41.63) * mm});
            skLineSegment(sketch, "E30.11.32.0", {"start": v(51.46, -37.4) * mm, "end": v(52.86, -38.48) * mm});
            skArc(sketch, "E30.14.32.0", {"start": v(51.27, -37.29) * mm, "mid": v(50.14, -36.97) * mm, "end": v(49, -36.73) * mm});
            skPoint(sketch, "E30.18.32.0", {"position": v(48.63, -36.67) * mm});
            skArc(sketch, "E30.19.32.0", {"start": v(48.87, -40.38) * mm, "mid": v(48.27, -39.38) * mm, "end": v(47.76, -38.33) * mm});
            skPoint(sketch, "E30.23.32.0", {"position": v(48.93, -40.48) * mm});
            skPoint(sketch, "E30.24.32.0", {"position": v(51.37, -37.32) * mm});
            skPoint(sketch, "E30.25.32.0", {"position": v(47.61, -37.99) * mm});
            skArc(sketch, "E30.26.32.0", {"start": v(49, -36.73) * mm, "mid": v(48.67, -36.76) * mm, "end": v(48.4, -36.95) * mm});
            skArc(sketch, "E30.30.32.0", {"start": v(47.82, -37.7) * mm, "mid": v(47.7, -38) * mm, "end": v(47.76, -38.33) * mm});
            skLineSegment(sketch, "E30.34.32.0", {"start": v(47.82, -37.7) * mm, "end": v(48.1, -37.31) * mm});
            skLineSegment(sketch, "E30.37.32.0", {"start": v(48.4, -36.95) * mm, "end": v(48.1, -37.31) * mm});
            skArc(sketch, "E30.40.32.0", {"start": v(51.46, -37.4) * mm, "mid": v(51.37, -37.33) * mm, "end": v(51.27, -37.29) * mm});
            skArc(sketch, "E30.44.32.0", {"start": v(48.87, -40.38) * mm, "mid": v(48.93, -40.47) * mm, "end": v(49.01, -40.54) * mm});
            skArc(sketch, "E30.1.33.0", {"start": v(57.27, -31.55) * mm, "mid": v(57.76, -31.62) * mm, "end": v(58.15, -31.3) * mm});
            skArc(sketch, "E30.4.33.0", {"start": v(55.45, -35.88) * mm, "mid": v(55.53, -35.38) * mm, "end": v(55.24, -34.98) * mm});
            skLineSegment(sketch, "E30.8.33.0", {"start": v(53.7, -34.08) * mm, "end": v(55.24, -34.98) * mm});
            skLineSegment(sketch, "E30.11.33.0", {"start": v(55.74, -30.65) * mm, "end": v(57.27, -31.55) * mm});
            skArc(sketch, "E30.14.33.0", {"start": v(55.54, -30.57) * mm, "mid": v(54.38, -30.39) * mm, "end": v(53.22, -30.3) * mm});
            skPoint(sketch, "E30.18.33.0", {"position": v(52.85, -30.28) * mm});
            skArc(sketch, "E30.19.33.0", {"start": v(53.54, -33.94) * mm, "mid": v(52.83, -33.01) * mm, "end": v(52.19, -32.04) * mm});
            skPoint(sketch, "E30.23.33.0", {"position": v(53.61, -34.03) * mm});
            skPoint(sketch, "E30.24.33.0", {"position": v(55.65, -30.6) * mm});
            skPoint(sketch, "E30.25.33.0", {"position": v(52, -31.72) * mm});
            skArc(sketch, "E30.26.33.0", {"start": v(53.22, -30.3) * mm, "mid": v(52.9, -30.37) * mm, "end": v(52.65, -30.59) * mm});
            skArc(sketch, "E30.30.33.0", {"start": v(52.17, -31.4) * mm, "mid": v(52.1, -31.72) * mm, "end": v(52.19, -32.04) * mm});
            skLineSegment(sketch, "E30.34.33.0", {"start": v(52.17, -31.4) * mm, "end": v(52.4, -30.99) * mm});
            skLineSegment(sketch, "E30.37.33.0", {"start": v(52.65, -30.59) * mm, "end": v(52.4, -30.99) * mm});
            skArc(sketch, "E30.40.33.0", {"start": v(55.74, -30.65) * mm, "mid": v(55.64, -30.6) * mm, "end": v(55.54, -30.57) * mm});
            skArc(sketch, "E30.44.33.0", {"start": v(53.54, -33.94) * mm, "mid": v(53.62, -34.02) * mm, "end": v(53.7, -34.08) * mm});
            skArc(sketch, "E30.1.34.0", {"start": v(60.77, -24.12) * mm, "mid": v(61.27, -24.13) * mm, "end": v(61.61, -23.77) * mm});
            skArc(sketch, "E30.4.34.0", {"start": v(59.5, -28.64) * mm, "mid": v(59.53, -28.15) * mm, "end": v(59.19, -27.78) * mm});
            skLineSegment(sketch, "E30.8.34.0", {"start": v(57.56, -27.08) * mm, "end": v(59.19, -27.78) * mm});
            skLineSegment(sketch, "E30.11.34.0", {"start": v(59.14, -23.42) * mm, "end": v(60.77, -24.12) * mm});
            skArc(sketch, "E30.14.34.0", {"start": v(58.93, -23.37) * mm, "mid": v(57.76, -23.33) * mm, "end": v(56.6, -23.39) * mm});
            skPoint(sketch, "E30.18.34.0", {"position": v(56.23, -23.42) * mm});
            skArc(sketch, "E30.19.34.0", {"start": v(57.38, -26.96) * mm, "mid": v(56.55, -26.13) * mm, "end": v(55.79, -25.25) * mm});
            skPoint(sketch, "E30.23.34.0", {"position": v(57.46, -27.04) * mm});
            skPoint(sketch, "E30.24.34.0", {"position": v(59.04, -23.38) * mm});
            skPoint(sketch, "E30.25.34.0", {"position": v(55.56, -24.95) * mm});
            skArc(sketch, "E30.26.34.0", {"start": v(56.6, -23.39) * mm, "mid": v(56.28, -23.5) * mm, "end": v(56.07, -23.75) * mm});
            skArc(sketch, "E30.30.34.0", {"start": v(55.7, -24.62) * mm, "mid": v(55.66, -24.94) * mm, "end": v(55.79, -25.25) * mm});
            skLineSegment(sketch, "E30.34.34.0", {"start": v(55.7, -24.62) * mm, "end": v(55.87, -24.18) * mm});
            skLineSegment(sketch, "E30.37.34.0", {"start": v(56.07, -23.75) * mm, "end": v(55.87, -24.18) * mm});
            skArc(sketch, "E30.40.34.0", {"start": v(59.14, -23.42) * mm, "mid": v(59.04, -23.38) * mm, "end": v(58.93, -23.37) * mm});
            skArc(sketch, "E30.44.34.0", {"start": v(57.38, -26.96) * mm, "mid": v(57.46, -27.03) * mm, "end": v(57.56, -27.08) * mm});
            skArc(sketch, "E30.1.35.0", {"start": v(63.31, -16.32) * mm, "mid": v(63.8, -16.26) * mm, "end": v(64.1, -15.86) * mm});
            skArc(sketch, "E30.4.35.0", {"start": v(62.63, -20.96) * mm, "mid": v(62.59, -20.46) * mm, "end": v(62.2, -20.15) * mm});
            skLineSegment(sketch, "E30.8.35.0", {"start": v(60.5, -19.65) * mm, "end": v(62.2, -20.15) * mm});
            skLineSegment(sketch, "E30.11.35.0", {"start": v(61.6, -15.82) * mm, "end": v(63.31, -16.32) * mm});
            skArc(sketch, "E30.14.35.0", {"start": v(61.4, -15.8) * mm, "mid": v(60.23, -15.91) * mm, "end": v(59.08, -16.1) * mm});
            skPoint(sketch, "E30.18.35.0", {"position": v(58.72, -16.19) * mm});
            skArc(sketch, "E30.19.35.0", {"start": v(60.3, -19.56) * mm, "mid": v(59.38, -18.84) * mm, "end": v(58.51, -18.05) * mm});
            skPoint(sketch, "E30.23.35.0", {"position": v(60.4, -19.62) * mm});
            skPoint(sketch, "E30.24.35.0", {"position": v(61.5, -15.8) * mm});
            skPoint(sketch, "E30.25.35.0", {"position": v(58.25, -17.8) * mm});
            skArc(sketch, "E30.26.35.0", {"start": v(59.08, -16.1) * mm, "mid": v(58.78, -16.26) * mm, "end": v(58.6, -16.53) * mm});
            skArc(sketch, "E30.30.35.0", {"start": v(58.34, -17.44) * mm, "mid": v(58.35, -17.77) * mm, "end": v(58.51, -18.05) * mm});
            skLineSegment(sketch, "E30.34.35.0", {"start": v(58.34, -17.44) * mm, "end": v(58.46, -16.98) * mm});
            skLineSegment(sketch, "E30.37.35.0", {"start": v(58.6, -16.53) * mm, "end": v(58.46, -16.98) * mm});
            skArc(sketch, "E30.40.35.0", {"start": v(61.6, -15.82) * mm, "mid": v(61.5, -15.8) * mm, "end": v(61.4, -15.8) * mm});
            skArc(sketch, "E30.44.35.0", {"start": v(60.3, -19.56) * mm, "mid": v(60.4, -19.61) * mm, "end": v(60.5, -19.65) * mm});
            skArc(sketch, "E30.1.36.0", {"start": v(64.86, -8.25) * mm, "mid": v(65.34, -8.13) * mm, "end": v(65.59, -7.7) * mm});
            skArc(sketch, "E30.4.36.0", {"start": v(64.76, -12.95) * mm, "mid": v(64.66, -12.46) * mm, "end": v(64.24, -12.2) * mm});
            skLineSegment(sketch, "E30.8.36.0", {"start": v(62.48, -11.92) * mm, "end": v(64.24, -12.2) * mm});
            skLineSegment(sketch, "E30.11.36.0", {"start": v(63.1, -7.98) * mm, "end": v(64.86, -8.25) * mm});
            skArc(sketch, "E30.14.36.0", {"start": v(62.9, -7.98) * mm, "mid": v(61.75, -8.24) * mm, "end": v(60.63, -8.58) * mm});
            skPoint(sketch, "E30.18.36.0", {"position": v(60.28, -8.7) * mm});
            skArc(sketch, "E30.19.36.0", {"start": v(62.28, -11.85) * mm, "mid": v(61.27, -11.25) * mm, "end": v(60.31, -10.58) * mm});
            skPoint(sketch, "E30.23.36.0", {"position": v(62.38, -11.9) * mm});
            skPoint(sketch, "E30.24.36.0", {"position": v(63, -7.96) * mm});
            skPoint(sketch, "E30.25.36.0", {"position": v(60.02, -10.35) * mm});
            skArc(sketch, "E30.26.36.0", {"start": v(60.63, -8.58) * mm, "mid": v(60.36, -8.76) * mm, "end": v(60.22, -9.06) * mm});
            skArc(sketch, "E30.30.36.0", {"start": v(60.07, -10) * mm, "mid": v(60.11, -10.32) * mm, "end": v(60.31, -10.58) * mm});
            skLineSegment(sketch, "E30.34.36.0", {"start": v(60.07, -10) * mm, "end": v(60.13, -9.52) * mm});
            skLineSegment(sketch, "E30.37.36.0", {"start": v(60.22, -9.06) * mm, "end": v(60.13, -9.52) * mm});
            skArc(sketch, "E30.40.36.0", {"start": v(63.1, -7.98) * mm, "mid": v(63, -7.97) * mm, "end": v(62.9, -7.98) * mm});
            skArc(sketch, "E30.44.36.0", {"start": v(62.28, -11.85) * mm, "mid": v(62.38, -11.89) * mm, "end": v(62.48, -11.92) * mm});
            skArc(sketch, "E30.1.37.0", {"start": v(65.38, -0.06) * mm, "mid": v(65.85, 0.12) * mm, "end": v(66.04, 0.58) * mm});
            skArc(sketch, "E30.4.37.0", {"start": v(65.87, -4.73) * mm, "mid": v(65.7, -4.26) * mm, "end": v(65.26, -4.05) * mm});
            skLineSegment(sketch, "E30.8.37.0", {"start": v(63.48, -4) * mm, "end": v(65.26, -4.05) * mm});
            skLineSegment(sketch, "E30.11.37.0", {"start": v(63.6, 0) * mm, "end": v(65.38, -0.06) * mm});
            skArc(sketch, "E30.14.37.0", {"start": v(63.4, -0.03) * mm, "mid": v(62.3, -0.43) * mm, "end": v(61.23, -0.91) * mm});
            skPoint(sketch, "E30.18.37.0", {"position": v(60.9, -1.08) * mm});
            skArc(sketch, "E30.19.37.0", {"start": v(63.27, -3.95) * mm, "mid": v(62.2, -3.48) * mm, "end": v(61.17, -2.94) * mm});
            skPoint(sketch, "E30.23.37.0", {"position": v(63.37, -3.99) * mm});
            skPoint(sketch, "E30.24.37.0", {"position": v(63.5, 0) * mm});
            skPoint(sketch, "E30.25.37.0", {"position": v(60.85, -2.75) * mm});
            skArc(sketch, "E30.26.37.0", {"start": v(61.23, -0.91) * mm, "mid": v(60.98, -1.13) * mm, "end": v(60.88, -1.44) * mm});
            skArc(sketch, "E30.30.37.0", {"start": v(60.85, -2.38) * mm, "mid": v(60.93, -2.7) * mm, "end": v(61.17, -2.94) * mm});
            skLineSegment(sketch, "E30.34.37.0", {"start": v(60.85, -2.38) * mm, "end": v(60.85, -1.91) * mm});
            skLineSegment(sketch, "E30.37.37.0", {"start": v(60.88, -1.44) * mm, "end": v(60.85, -1.91) * mm});
            skArc(sketch, "E30.40.37.0", {"start": v(63.6, 0) * mm, "mid": v(63.5, 0) * mm, "end": v(63.4, -0.03) * mm});
            skArc(sketch, "E30.44.37.0", {"start": v(63.27, -3.95) * mm, "mid": v(63.38, -3.98) * mm, "end": v(63.48, -4) * mm});
            skArc(sketch, "E30.1.38.0", {"start": v(64.87, 8.14) * mm, "mid": v(65.31, 8.37) * mm, "end": v(65.44, 8.85) * mm});
            skArc(sketch, "E30.4.38.0", {"start": v(65.94, 3.57) * mm, "mid": v(65.72, 4.01) * mm, "end": v(65.25, 4.16) * mm});
            skLineSegment(sketch, "E30.8.38.0", {"start": v(63.48, 4) * mm, "end": v(65.25, 4.16) * mm});
            skLineSegment(sketch, "E30.11.38.0", {"start": v(63.1, 7.97) * mm, "end": v(64.87, 8.14) * mm});
            skArc(sketch, "E30.14.38.0", {"start": v(62.9, 7.91) * mm, "mid": v(61.86, 7.38) * mm, "end": v(60.86, 6.77) * mm});
            skPoint(sketch, "E30.18.38.0", {"position": v(60.55, 6.56) * mm});
            skArc(sketch, "E30.19.38.0", {"start": v(63.27, 4.01) * mm, "mid": v(62.15, 4.34) * mm, "end": v(61.05, 4.75) * mm});
            skPoint(sketch, "E30.23.38.0", {"position": v(63.37, 3.99) * mm});
            skPoint(sketch, "E30.24.38.0", {"position": v(63, 7.96) * mm});
            skPoint(sketch, "E30.25.38.0", {"position": v(60.71, 4.9) * mm});
            skArc(sketch, "E30.26.38.0", {"start": v(60.86, 6.77) * mm, "mid": v(60.64, 6.52) * mm, "end": v(60.58, 6.2) * mm});
            skArc(sketch, "E30.30.38.0", {"start": v(60.67, 5.26) * mm, "mid": v(60.8, 4.96) * mm, "end": v(61.05, 4.75) * mm});
            skLineSegment(sketch, "E30.34.38.0", {"start": v(60.67, 5.26) * mm, "end": v(60.6, 5.73) * mm});
            skLineSegment(sketch, "E30.37.38.0", {"start": v(60.58, 6.2) * mm, "end": v(60.6, 5.73) * mm});
            skArc(sketch, "E30.40.38.0", {"start": v(63.1, 7.97) * mm, "mid": v(63, 7.95) * mm, "end": v(62.9, 7.91) * mm});
            skArc(sketch, "E30.44.38.0", {"start": v(63.27, 4.01) * mm, "mid": v(63.37, 4) * mm, "end": v(63.48, 4) * mm});
            skArc(sketch, "E30.1.39.0", {"start": v(63.34, 16.2) * mm, "mid": v(63.75, 16.5) * mm, "end": v(63.82, 16.99) * mm});
            skArc(sketch, "E30.4.39.0", {"start": v(64.98, 11.8) * mm, "mid": v(64.7, 12.22) * mm, "end": v(64.21, 12.3) * mm});
            skLineSegment(sketch, "E30.8.39.0", {"start": v(62.48, 11.92) * mm, "end": v(64.21, 12.3) * mm});
            skLineSegment(sketch, "E30.11.39.0", {"start": v(61.61, 15.82) * mm, "end": v(63.34, 16.2) * mm});
            skArc(sketch, "E30.14.39.0", {"start": v(61.41, 15.73) * mm, "mid": v(60.45, 15.07) * mm, "end": v(59.53, 14.34) * mm});
            skPoint(sketch, "E30.18.39.0", {"position": v(59.25, 14.1) * mm});
            skArc(sketch, "E30.19.39.0", {"start": v(62.27, 11.91) * mm, "mid": v(61.11, 12.1) * mm, "end": v(59.97, 12.37) * mm});
            skPoint(sketch, "E30.23.39.0", {"position": v(62.38, 11.9) * mm});
            skPoint(sketch, "E30.24.39.0", {"position": v(61.5, 15.8) * mm});
            skPoint(sketch, "E30.25.39.0", {"position": v(59.62, 12.47) * mm});
            skArc(sketch, "E30.26.39.0", {"start": v(59.53, 14.34) * mm, "mid": v(59.35, 14.07) * mm, "end": v(59.32, 13.74) * mm});
            skArc(sketch, "E30.30.39.0", {"start": v(59.53, 12.82) * mm, "mid": v(59.69, 12.54) * mm, "end": v(59.97, 12.37) * mm});
            skLineSegment(sketch, "E30.34.39.0", {"start": v(59.53, 12.82) * mm, "end": v(59.41, 13.28) * mm});
            skLineSegment(sketch, "E30.37.39.0", {"start": v(59.32, 13.74) * mm, "end": v(59.41, 13.28) * mm});
            skArc(sketch, "E30.40.39.0", {"start": v(61.61, 15.82) * mm, "mid": v(61.5, 15.78) * mm, "end": v(61.41, 15.73) * mm});
            skArc(sketch, "E30.44.39.0", {"start": v(62.27, 11.91) * mm, "mid": v(62.37, 11.9) * mm, "end": v(62.48, 11.92) * mm});
            skArc(sketch, "E30.1.40.0", {"start": v(60.81, 24.01) * mm, "mid": v(61.18, 24.35) * mm, "end": v(61.19, 24.85) * mm});
            skArc(sketch, "E30.4.40.0", {"start": v(62.98, 19.85) * mm, "mid": v(62.66, 20.23) * mm, "end": v(62.16, 20.26) * mm});
            skLineSegment(sketch, "E30.8.40.0", {"start": v(60.5, 19.66) * mm, "end": v(62.16, 20.26) * mm});
            skLineSegment(sketch, "E30.11.40.0", {"start": v(59.14, 23.41) * mm, "end": v(60.81, 24.01) * mm});
            skArc(sketch, "E30.14.40.0", {"start": v(58.95, 23.3) * mm, "mid": v(58.08, 22.53) * mm, "end": v(57.26, 21.7) * mm});
            skPoint(sketch, "E30.18.40.0", {"position": v(57.02, 21.42) * mm});
            skArc(sketch, "E30.19.40.0", {"start": v(60.28, 19.62) * mm, "mid": v(59.11, 19.66) * mm, "end": v(57.95, 19.79) * mm});
            skPoint(sketch, "E30.23.40.0", {"position": v(60.4, 19.62) * mm});
            skPoint(sketch, "E30.24.40.0", {"position": v(59.04, 23.38) * mm});
            skPoint(sketch, "E30.25.40.0", {"position": v(57.58, 19.84) * mm});
            skArc(sketch, "E30.26.40.0", {"start": v(57.26, 21.7) * mm, "mid": v(57.11, 21.4) * mm, "end": v(57.13, 21.07) * mm});
            skArc(sketch, "E30.30.40.0", {"start": v(57.45, 20.18) * mm, "mid": v(57.65, 19.92) * mm, "end": v(57.95, 19.79) * mm});
            skLineSegment(sketch, "E30.34.40.0", {"start": v(57.45, 20.18) * mm, "end": v(57.28, 20.62) * mm});
            skLineSegment(sketch, "E30.37.40.0", {"start": v(57.13, 21.07) * mm, "end": v(57.28, 20.62) * mm});
            skArc(sketch, "E30.40.40.0", {"start": v(59.14, 23.41) * mm, "mid": v(59.04, 23.37) * mm, "end": v(58.95, 23.3) * mm});
            skArc(sketch, "E30.44.40.0", {"start": v(60.28, 19.62) * mm, "mid": v(60.39, 19.63) * mm, "end": v(60.5, 19.66) * mm});
            skArc(sketch, "E30.1.41.0", {"start": v(57.32, 31.45) * mm, "mid": v(57.64, 31.83) * mm, "end": v(57.59, 32.32) * mm});
            skArc(sketch, "E30.4.41.0", {"start": v(60, 27.6) * mm, "mid": v(59.63, 27.93) * mm, "end": v(59.13, 27.9) * mm});
            skLineSegment(sketch, "E30.8.41.0", {"start": v(57.55, 27.09) * mm, "end": v(59.13, 27.9) * mm});
            skLineSegment(sketch, "E30.11.41.0", {"start": v(55.74, 30.64) * mm, "end": v(57.32, 31.45) * mm});
            skArc(sketch, "E30.14.41.0", {"start": v(55.57, 30.51) * mm, "mid": v(54.8, 29.63) * mm, "end": v(54.1, 28.7) * mm});
            skPoint(sketch, "E30.18.41.0", {"position": v(53.89, 28.4) * mm});
            skArc(sketch, "E30.19.41.0", {"start": v(57.35, 27.02) * mm, "mid": v(56.18, 26.92) * mm, "end": v(55.01, 26.9) * mm});
            skPoint(sketch, "E30.23.41.0", {"position": v(57.46, 27.04) * mm});
            skPoint(sketch, "E30.24.41.0", {"position": v(55.65, 30.6) * mm});
            skPoint(sketch, "E30.25.41.0", {"position": v(54.64, 26.9) * mm});
            skArc(sketch, "E30.26.41.0", {"start": v(54.1, 28.7) * mm, "mid": v(53.98, 28.39) * mm, "end": v(54.04, 28.06) * mm});
            skArc(sketch, "E30.30.41.0", {"start": v(54.47, 27.22) * mm, "mid": v(54.7, 26.99) * mm, "end": v(55.01, 26.9) * mm});
            skLineSegment(sketch, "E30.34.41.0", {"start": v(54.47, 27.22) * mm, "end": v(54.24, 27.64) * mm});
            skLineSegment(sketch, "E30.37.41.0", {"start": v(54.04, 28.06) * mm, "end": v(54.24, 27.64) * mm});
            skArc(sketch, "E30.40.41.0", {"start": v(55.74, 30.64) * mm, "mid": v(55.65, 30.58) * mm, "end": v(55.57, 30.51) * mm});
            skArc(sketch, "E30.44.41.0", {"start": v(57.35, 27.02) * mm, "mid": v(57.45, 27.05) * mm, "end": v(57.55, 27.09) * mm});
            skArc(sketch, "E30.1.42.0", {"start": v(52.93, 38.38) * mm, "mid": v(53.2, 38.8) * mm, "end": v(53.08, 39.29) * mm});
            skArc(sketch, "E30.4.42.0", {"start": v(56.07, 34.9) * mm, "mid": v(55.66, 35.18) * mm, "end": v(55.17, 35.08) * mm});
            skLineSegment(sketch, "E30.8.42.0", {"start": v(53.7, 34.09) * mm, "end": v(55.17, 35.08) * mm});
            skLineSegment(sketch, "E30.11.42.0", {"start": v(51.46, 37.39) * mm, "end": v(52.93, 38.38) * mm});
            skArc(sketch, "E30.14.42.0", {"start": v(51.3, 37.23) * mm, "mid": v(50.65, 36.27) * mm, "end": v(50.07, 35.25) * mm});
            skPoint(sketch, "E30.18.42.0", {"position": v(49.9, 34.92) * mm});
            skArc(sketch, "E30.19.42.0", {"start": v(53.5, 34) * mm, "mid": v(52.37, 33.74) * mm, "end": v(51.2, 33.58) * mm});
            skPoint(sketch, "E30.23.42.0", {"position": v(53.61, 34.03) * mm});
            skPoint(sketch, "E30.24.42.0", {"position": v(51.37, 37.32) * mm});
            skPoint(sketch, "E30.25.42.0", {"position": v(50.84, 33.54) * mm});
            skArc(sketch, "E30.26.42.0", {"start": v(50.07, 35.25) * mm, "mid": v(50, 34.93) * mm, "end": v(50.1, 34.62) * mm});
            skArc(sketch, "E30.30.42.0", {"start": v(50.63, 33.84) * mm, "mid": v(50.88, 33.63) * mm, "end": v(51.2, 33.58) * mm});
            skLineSegment(sketch, "E30.34.42.0", {"start": v(50.63, 33.84) * mm, "end": v(50.35, 34.22) * mm});
            skLineSegment(sketch, "E30.37.42.0", {"start": v(50.1, 34.62) * mm, "end": v(50.35, 34.22) * mm});
            skArc(sketch, "E30.40.42.0", {"start": v(51.46, 37.39) * mm, "mid": v(51.38, 37.32) * mm, "end": v(51.3, 37.23) * mm});
            skArc(sketch, "E30.44.42.0", {"start": v(53.5, 34) * mm, "mid": v(53.6, 34.03) * mm, "end": v(53.7, 34.09) * mm});
            skArc(sketch, "E30.1.43.0", {"start": v(47.7, 44.71) * mm, "mid": v(47.92, 45.16) * mm, "end": v(47.74, 45.63) * mm});
            skArc(sketch, "E30.4.43.0", {"start": v(51.25, 41.65) * mm, "mid": v(50.81, 41.88) * mm, "end": v(50.34, 41.72) * mm});
            skLineSegment(sketch, "E30.8.43.0", {"start": v(49, 40.55) * mm, "end": v(50.34, 41.72) * mm});
            skLineSegment(sketch, "E30.11.43.0", {"start": v(46.37, 43.54) * mm, "end": v(47.7, 44.71) * mm});
            skArc(sketch, "E30.14.43.0", {"start": v(46.24, 43.37) * mm, "mid": v(45.7, 42.33) * mm, "end": v(45.26, 41.25) * mm});
            skPoint(sketch, "E30.18.43.0", {"position": v(45.13, 40.9) * mm});
            skArc(sketch, "E30.19.43.0", {"start": v(48.82, 40.43) * mm, "mid": v(47.72, 40.04) * mm, "end": v(46.6, 39.73) * mm});
            skPoint(sketch, "E30.23.43.0", {"position": v(48.93, 40.48) * mm});
            skPoint(sketch, "E30.24.43.0", {"position": v(46.29, 43.47) * mm});
            skPoint(sketch, "E30.25.43.0", {"position": v(46.24, 39.65) * mm});
            skArc(sketch, "E30.26.43.0", {"start": v(45.26, 41.25) * mm, "mid": v(45.23, 40.92) * mm, "end": v(45.36, 40.62) * mm});
            skArc(sketch, "E30.30.43.0", {"start": v(45.99, 39.91) * mm, "mid": v(46.27, 39.74) * mm, "end": v(46.6, 39.73) * mm});
            skLineSegment(sketch, "E30.34.43.0", {"start": v(45.99, 39.91) * mm, "end": v(45.66, 40.26) * mm});
            skLineSegment(sketch, "E30.37.43.0", {"start": v(45.36, 40.62) * mm, "end": v(45.66, 40.26) * mm});
            skArc(sketch, "E30.40.43.0", {"start": v(46.37, 43.54) * mm, "mid": v(46.3, 43.46) * mm, "end": v(46.24, 43.37) * mm});
            skArc(sketch, "E30.44.43.0", {"start": v(48.82, 40.43) * mm, "mid": v(48.92, 40.48) * mm, "end": v(49, 40.55) * mm});
            skArc(sketch, "E30.1.44.0", {"start": v(41.72, 50.34) * mm, "mid": v(41.88, 50.81) * mm, "end": v(41.65, 51.25) * mm});
            skArc(sketch, "E30.4.44.0", {"start": v(45.63, 47.74) * mm, "mid": v(45.16, 47.92) * mm, "end": v(44.71, 47.7) * mm});
            skLineSegment(sketch, "E30.8.44.0", {"start": v(43.54, 46.37) * mm, "end": v(44.71, 47.7) * mm});
            skLineSegment(sketch, "E30.11.44.0", {"start": v(40.55, 49) * mm, "end": v(41.72, 50.34) * mm});
            skArc(sketch, "E30.14.44.0", {"start": v(40.43, 48.82) * mm, "mid": v(40.04, 47.72) * mm, "end": v(39.73, 46.6) * mm});
            skPoint(sketch, "E30.18.44.0", {"position": v(39.65, 46.24) * mm});
            skArc(sketch, "E30.19.44.0", {"start": v(43.37, 46.24) * mm, "mid": v(42.33, 45.7) * mm, "end": v(41.25, 45.26) * mm});
            skPoint(sketch, "E30.23.44.0", {"position": v(43.47, 46.29) * mm});
            skPoint(sketch, "E30.24.44.0", {"position": v(40.48, 48.93) * mm});
            skPoint(sketch, "E30.25.44.0", {"position": v(40.9, 45.13) * mm});
            skArc(sketch, "E30.26.44.0", {"start": v(39.73, 46.6) * mm, "mid": v(39.74, 46.27) * mm, "end": v(39.91, 45.99) * mm});
            skArc(sketch, "E30.30.44.0", {"start": v(40.62, 45.36) * mm, "mid": v(40.92, 45.23) * mm, "end": v(41.25, 45.26) * mm});
            skLineSegment(sketch, "E30.34.44.0", {"start": v(40.62, 45.36) * mm, "end": v(40.26, 45.66) * mm});
            skLineSegment(sketch, "E30.37.44.0", {"start": v(39.91, 45.99) * mm, "end": v(40.26, 45.66) * mm});
            skArc(sketch, "E30.40.44.0", {"start": v(40.55, 49) * mm, "mid": v(40.48, 48.92) * mm, "end": v(40.43, 48.82) * mm});
            skArc(sketch, "E30.44.44.0", {"start": v(43.37, 46.24) * mm, "mid": v(43.46, 46.3) * mm, "end": v(43.54, 46.37) * mm});
            skArc(sketch, "E30.1.45.0", {"start": v(35.08, 55.17) * mm, "mid": v(35.18, 55.66) * mm, "end": v(34.9, 56.07) * mm});
            skArc(sketch, "E30.4.45.0", {"start": v(39.29, 53.08) * mm, "mid": v(38.8, 53.2) * mm, "end": v(38.38, 52.93) * mm});
            skLineSegment(sketch, "E30.8.45.0", {"start": v(37.39, 51.46) * mm, "end": v(38.38, 52.93) * mm});
            skLineSegment(sketch, "E30.11.45.0", {"start": v(34.09, 53.7) * mm, "end": v(35.08, 55.17) * mm});
            skArc(sketch, "E30.14.45.0", {"start": v(34, 53.5) * mm, "mid": v(33.74, 52.37) * mm, "end": v(33.58, 51.2) * mm});
            skPoint(sketch, "E30.18.45.0", {"position": v(33.54, 50.84) * mm});
            skArc(sketch, "E30.19.45.0", {"start": v(37.23, 51.3) * mm, "mid": v(36.27, 50.65) * mm, "end": v(35.25, 50.07) * mm});
            skPoint(sketch, "E30.23.45.0", {"position": v(37.32, 51.37) * mm});
            skPoint(sketch, "E30.24.45.0", {"position": v(34.03, 53.61) * mm});
            skPoint(sketch, "E30.25.45.0", {"position": v(34.92, 49.9) * mm});
            skArc(sketch, "E30.26.45.0", {"start": v(33.58, 51.2) * mm, "mid": v(33.63, 50.88) * mm, "end": v(33.84, 50.63) * mm});
            skArc(sketch, "E30.30.45.0", {"start": v(34.62, 50.1) * mm, "mid": v(34.93, 50) * mm, "end": v(35.25, 50.07) * mm});
            skLineSegment(sketch, "E30.34.45.0", {"start": v(34.62, 50.1) * mm, "end": v(34.22, 50.35) * mm});
            skLineSegment(sketch, "E30.37.45.0", {"start": v(33.84, 50.63) * mm, "end": v(34.22, 50.35) * mm});
            skArc(sketch, "E30.40.45.0", {"start": v(34.09, 53.7) * mm, "mid": v(34.03, 53.6) * mm, "end": v(34, 53.5) * mm});
            skArc(sketch, "E30.44.45.0", {"start": v(37.23, 51.3) * mm, "mid": v(37.32, 51.38) * mm, "end": v(37.39, 51.46) * mm});
            skArc(sketch, "E30.1.46.0", {"start": v(27.9, 59.13) * mm, "mid": v(27.93, 59.63) * mm, "end": v(27.6, 60) * mm});
            skArc(sketch, "E30.4.46.0", {"start": v(32.32, 57.59) * mm, "mid": v(31.83, 57.64) * mm, "end": v(31.45, 57.32) * mm});
            skLineSegment(sketch, "E30.8.46.0", {"start": v(30.64, 55.74) * mm, "end": v(31.45, 57.32) * mm});
            skLineSegment(sketch, "E30.11.46.0", {"start": v(27.09, 57.55) * mm, "end": v(27.9, 59.13) * mm});
            skArc(sketch, "E30.14.46.0", {"start": v(27.02, 57.35) * mm, "mid": v(26.92, 56.18) * mm, "end": v(26.9, 55.01) * mm});
            skPoint(sketch, "E30.18.46.0", {"position": v(26.9, 54.64) * mm});
            skArc(sketch, "E30.19.46.0", {"start": v(30.51, 55.57) * mm, "mid": v(29.63, 54.8) * mm, "end": v(28.7, 54.1) * mm});
            skPoint(sketch, "E30.23.46.0", {"position": v(30.6, 55.65) * mm});
            skPoint(sketch, "E30.24.46.0", {"position": v(27.04, 57.46) * mm});
            skPoint(sketch, "E30.25.46.0", {"position": v(28.4, 53.89) * mm});
            skArc(sketch, "E30.26.46.0", {"start": v(26.9, 55.01) * mm, "mid": v(26.99, 54.7) * mm, "end": v(27.22, 54.47) * mm});
            skArc(sketch, "E30.30.46.0", {"start": v(28.06, 54.04) * mm, "mid": v(28.39, 53.98) * mm, "end": v(28.7, 54.1) * mm});
            skLineSegment(sketch, "E30.34.46.0", {"start": v(28.06, 54.04) * mm, "end": v(27.64, 54.24) * mm});
            skLineSegment(sketch, "E30.37.46.0", {"start": v(27.22, 54.47) * mm, "end": v(27.64, 54.24) * mm});
            skArc(sketch, "E30.40.46.0", {"start": v(27.09, 57.55) * mm, "mid": v(27.05, 57.45) * mm, "end": v(27.02, 57.35) * mm});
            skArc(sketch, "E30.44.46.0", {"start": v(30.51, 55.57) * mm, "mid": v(30.58, 55.65) * mm, "end": v(30.64, 55.74) * mm});
            skArc(sketch, "E30.1.47.0", {"start": v(20.26, 62.16) * mm, "mid": v(20.23, 62.66) * mm, "end": v(19.85, 62.98) * mm});
            skArc(sketch, "E30.4.47.0", {"start": v(24.85, 61.19) * mm, "mid": v(24.35, 61.18) * mm, "end": v(24.01, 60.81) * mm});
            skLineSegment(sketch, "E30.8.47.0", {"start": v(23.41, 59.14) * mm, "end": v(24.01, 60.81) * mm});
            skLineSegment(sketch, "E30.11.47.0", {"start": v(19.66, 60.5) * mm, "end": v(20.26, 62.16) * mm});
            skArc(sketch, "E30.14.47.0", {"start": v(19.62, 60.28) * mm, "mid": v(19.66, 59.11) * mm, "end": v(19.79, 57.95) * mm});
            skPoint(sketch, "E30.18.47.0", {"position": v(19.84, 57.58) * mm});
            skArc(sketch, "E30.19.47.0", {"start": v(23.3, 58.95) * mm, "mid": v(22.53, 58.08) * mm, "end": v(21.7, 57.26) * mm});
            skPoint(sketch, "E30.23.47.0", {"position": v(23.38, 59.04) * mm});
            skPoint(sketch, "E30.24.47.0", {"position": v(19.62, 60.4) * mm});
            skPoint(sketch, "E30.25.47.0", {"position": v(21.42, 57.02) * mm});
            skArc(sketch, "E30.26.47.0", {"start": v(19.79, 57.95) * mm, "mid": v(19.92, 57.65) * mm, "end": v(20.18, 57.45) * mm});
            skArc(sketch, "E30.30.47.0", {"start": v(21.07, 57.13) * mm, "mid": v(21.4, 57.11) * mm, "end": v(21.7, 57.26) * mm});
            skLineSegment(sketch, "E30.34.47.0", {"start": v(21.07, 57.13) * mm, "end": v(20.62, 57.28) * mm});
            skLineSegment(sketch, "E30.37.47.0", {"start": v(20.18, 57.45) * mm, "end": v(20.62, 57.28) * mm});
            skArc(sketch, "E30.40.47.0", {"start": v(19.66, 60.5) * mm, "mid": v(19.63, 60.39) * mm, "end": v(19.62, 60.28) * mm});
            skArc(sketch, "E30.44.47.0", {"start": v(23.3, 58.95) * mm, "mid": v(23.37, 59.04) * mm, "end": v(23.41, 59.14) * mm});
            skArc(sketch, "E30.1.48.0", {"start": v(12.3, 64.21) * mm, "mid": v(12.22, 64.7) * mm, "end": v(11.8, 64.98) * mm});
            skArc(sketch, "E30.4.48.0", {"start": v(16.99, 63.82) * mm, "mid": v(16.5, 63.75) * mm, "end": v(16.2, 63.34) * mm});
            skLineSegment(sketch, "E30.8.48.0", {"start": v(15.82, 61.61) * mm, "end": v(16.2, 63.34) * mm});
            skLineSegment(sketch, "E30.11.48.0", {"start": v(11.92, 62.48) * mm, "end": v(12.3, 64.21) * mm});
            skArc(sketch, "E30.14.48.0", {"start": v(11.91, 62.27) * mm, "mid": v(12.1, 61.11) * mm, "end": v(12.37, 59.97) * mm});
            skPoint(sketch, "E30.18.48.0", {"position": v(12.47, 59.62) * mm});
            skArc(sketch, "E30.19.48.0", {"start": v(15.73, 61.41) * mm, "mid": v(15.07, 60.45) * mm, "end": v(14.34, 59.53) * mm});
            skPoint(sketch, "E30.23.48.0", {"position": v(15.8, 61.5) * mm});
            skPoint(sketch, "E30.24.48.0", {"position": v(11.9, 62.38) * mm});
            skPoint(sketch, "E30.25.48.0", {"position": v(14.1, 59.25) * mm});
            skArc(sketch, "E30.26.48.0", {"start": v(12.37, 59.97) * mm, "mid": v(12.54, 59.69) * mm, "end": v(12.82, 59.53) * mm});
            skArc(sketch, "E30.30.48.0", {"start": v(13.74, 59.32) * mm, "mid": v(14.07, 59.35) * mm, "end": v(14.34, 59.53) * mm});
            skLineSegment(sketch, "E30.34.48.0", {"start": v(13.74, 59.32) * mm, "end": v(13.28, 59.41) * mm});
            skLineSegment(sketch, "E30.37.48.0", {"start": v(12.82, 59.53) * mm, "end": v(13.28, 59.41) * mm});
            skArc(sketch, "E30.40.48.0", {"start": v(11.92, 62.48) * mm, "mid": v(11.9, 62.37) * mm, "end": v(11.91, 62.27) * mm});
            skArc(sketch, "E30.44.48.0", {"start": v(15.73, 61.41) * mm, "mid": v(15.78, 61.5) * mm, "end": v(15.82, 61.61) * mm});
            skArc(sketch, "E30.1.49.0", {"start": v(4.16, 65.25) * mm, "mid": v(4.01, 65.72) * mm, "end": v(3.57, 65.94) * mm});
            skArc(sketch, "E30.4.49.0", {"start": v(8.85, 65.44) * mm, "mid": v(8.37, 65.31) * mm, "end": v(8.14, 64.87) * mm});
            skLineSegment(sketch, "E30.8.49.0", {"start": v(7.97, 63.1) * mm, "end": v(8.14, 64.87) * mm});
            skLineSegment(sketch, "E30.11.49.0", {"start": v(4, 63.48) * mm, "end": v(4.16, 65.25) * mm});
            skArc(sketch, "E30.14.49.0", {"start": v(4.01, 63.27) * mm, "mid": v(4.34, 62.15) * mm, "end": v(4.75, 61.05) * mm});
            skPoint(sketch, "E30.18.49.0", {"position": v(4.9, 60.71) * mm});
            skArc(sketch, "E30.19.49.0", {"start": v(7.91, 62.9) * mm, "mid": v(7.38, 61.86) * mm, "end": v(6.77, 60.86) * mm});
            skPoint(sketch, "E30.23.49.0", {"position": v(7.96, 63) * mm});
            skPoint(sketch, "E30.24.49.0", {"position": v(3.99, 63.37) * mm});
            skPoint(sketch, "E30.25.49.0", {"position": v(6.56, 60.55) * mm});
            skArc(sketch, "E30.26.49.0", {"start": v(4.75, 61.05) * mm, "mid": v(4.96, 60.8) * mm, "end": v(5.26, 60.67) * mm});
            skArc(sketch, "E30.30.49.0", {"start": v(6.2, 60.58) * mm, "mid": v(6.52, 60.64) * mm, "end": v(6.77, 60.86) * mm});
            skLineSegment(sketch, "E30.34.49.0", {"start": v(6.2, 60.58) * mm, "end": v(5.73, 60.6) * mm});
            skLineSegment(sketch, "E30.37.49.0", {"start": v(5.26, 60.67) * mm, "end": v(5.73, 60.6) * mm});
            skArc(sketch, "E30.40.49.0", {"start": v(4, 63.48) * mm, "mid": v(4, 63.37) * mm, "end": v(4.01, 63.27) * mm});
            skArc(sketch, "E30.44.49.0", {"start": v(7.91, 62.9) * mm, "mid": v(7.95, 63) * mm, "end": v(7.97, 63.1) * mm});
            skArc(sketch, "E31.2.3.0", {"start": v(-48.23, 52.27) * mm, "mid": v(-48.02, 52.7) * mm, "end": v(-48.16, 53.14) * mm});
            skLineSegment(sketch, "E31.4.3.0", {"start": v(-50.9, 56.51) * mm, "end": v(-48.16, 53.14) * mm});
            skLineSegment(sketch, "E31.7.3.0", {"start": v(-44.7, 61.53) * mm, "end": v(-41.96, 58.16) * mm});
            skPoint(sketch, "E31.10.3.0", {"position": v(-50.95, 63.33) * mm});
            skPoint(sketch, "E31.11.3.0", {"position": v(-50.99, 56.63) * mm});
            skPoint(sketch, "E31.12.3.0", {"position": v(-51.35, 63) * mm});
            skArc(sketch, "E31.13.3.0", {"start": v(-51.02, 56.78) * mm, "mid": v(-51.43, 59.75) * mm, "end": v(-51.37, 62.76) * mm});
            skPoint(sketch, "E31.17.3.0", {"position": v(-44.79, 61.65) * mm});
            skArc(sketch, "E31.18.3.0", {"start": v(-44.93, 61.71) * mm, "mid": v(-47.75, 62.73) * mm, "end": v(-50.7, 63.3) * mm});
            skArc(sketch, "E31.22.3.0", {"start": v(-50.7, 63.3) * mm, "mid": v(-50.94, 63.28) * mm, "end": v(-51.15, 63.18) * mm});
            skArc(sketch, "E31.26.3.0", {"start": v(-51.17, 63.17) * mm, "mid": v(-51.3, 62.98) * mm, "end": v(-51.37, 62.76) * mm});
            skArc(sketch, "E31.30.3.0", {"start": v(-44.7, 61.53) * mm, "mid": v(-44.8, 61.63) * mm, "end": v(-44.93, 61.71) * mm});
            skArc(sketch, "E31.34.3.0", {"start": v(-51.02, 56.78) * mm, "mid": v(-50.97, 56.64) * mm, "end": v(-50.9, 56.51) * mm});
            skLineSegment(sketch, "E31.38.3.0", {"start": v(-51.15, 63.18) * mm, "end": v(-51.16, 63.18) * mm});
            skLineSegment(sketch, "E31.41.3.0", {"start": v(-51.17, 63.17) * mm, "end": v(-51.16, 63.18) * mm});
            skArc(sketch, "E31.2.4.0", {"start": v(-58.04, 41.1) * mm, "mid": v(-57.93, 41.56) * mm, "end": v(-58.16, 41.96) * mm});
            skLineSegment(sketch, "E31.4.4.0", {"start": v(-61.53, 44.7) * mm, "end": v(-58.16, 41.96) * mm});
            skLineSegment(sketch, "E31.7.4.0", {"start": v(-56.51, 50.9) * mm, "end": v(-53.14, 48.16) * mm});
            skPoint(sketch, "E31.10.4.0", {"position": v(-63, 51.35) * mm});
            skPoint(sketch, "E31.11.4.0", {"position": v(-61.65, 44.79) * mm});
            skPoint(sketch, "E31.12.4.0", {"position": v(-63.33, 50.95) * mm});
            skArc(sketch, "E31.13.4.0", {"start": v(-61.71, 44.93) * mm, "mid": v(-62.73, 47.75) * mm, "end": v(-63.3, 50.7) * mm});
            skPoint(sketch, "E31.17.4.0", {"position": v(-56.63, 50.99) * mm});
            skArc(sketch, "E31.18.4.0", {"start": v(-56.78, 51.02) * mm, "mid": v(-59.75, 51.43) * mm, "end": v(-62.76, 51.37) * mm});
            skArc(sketch, "E31.22.4.0", {"start": v(-62.76, 51.37) * mm, "mid": v(-62.98, 51.3) * mm, "end": v(-63.17, 51.17) * mm});
            skArc(sketch, "E31.26.4.0", {"start": v(-63.18, 51.15) * mm, "mid": v(-63.28, 50.94) * mm, "end": v(-63.3, 50.7) * mm});
            skArc(sketch, "E31.30.4.0", {"start": v(-56.51, 50.9) * mm, "mid": v(-56.64, 50.97) * mm, "end": v(-56.78, 51.02) * mm});
            skArc(sketch, "E31.34.4.0", {"start": v(-61.71, 44.93) * mm, "mid": v(-61.63, 44.8) * mm, "end": v(-61.53, 44.7) * mm});
            skLineSegment(sketch, "E31.38.4.0", {"start": v(-63.17, 51.17) * mm, "end": v(-63.18, 51.16) * mm});
            skLineSegment(sketch, "E31.41.4.0", {"start": v(-63.18, 51.15) * mm, "end": v(-63.18, 51.16) * mm});
            skArc(sketch, "E31.2.5.0", {"start": v(-65.32, 28.14) * mm, "mid": v(-65.3, 28.6) * mm, "end": v(-65.61, 28.96) * mm});
            skLineSegment(sketch, "E31.4.5.0", {"start": v(-69.48, 30.93) * mm, "end": v(-65.61, 28.96) * mm});
            skLineSegment(sketch, "E31.7.5.0", {"start": v(-65.86, 38.03) * mm, "end": v(-62, 36.06) * mm});
            skPoint(sketch, "E31.10.5.0", {"position": v(-72.3, 37.13) * mm});
            skPoint(sketch, "E31.11.5.0", {"position": v(-69.61, 31) * mm});
            skPoint(sketch, "E31.12.5.0", {"position": v(-72.54, 36.67) * mm});
            skArc(sketch, "E31.13.5.0", {"start": v(-69.7, 31.11) * mm, "mid": v(-71.3, 33.67) * mm, "end": v(-72.46, 36.44) * mm});
            skPoint(sketch, "E31.17.5.0", {"position": v(-66, 38.1) * mm});
            skArc(sketch, "E31.18.5.0", {"start": v(-66.14, 38.1) * mm, "mid": v(-69.14, 37.89) * mm, "end": v(-72.07, 37.2) * mm});
            skArc(sketch, "E31.22.5.0", {"start": v(-72.07, 37.2) * mm, "mid": v(-72.28, 37.1) * mm, "end": v(-72.43, 36.91) * mm});
            skArc(sketch, "E31.26.5.0", {"start": v(-72.44, 36.9) * mm, "mid": v(-72.5, 36.67) * mm, "end": v(-72.46, 36.44) * mm});
            skArc(sketch, "E31.30.5.0", {"start": v(-65.86, 38.03) * mm, "mid": v(-66, 38.08) * mm, "end": v(-66.14, 38.1) * mm});
            skArc(sketch, "E31.34.5.0", {"start": v(-69.7, 31.11) * mm, "mid": v(-69.6, 31) * mm, "end": v(-69.48, 30.93) * mm});
            skLineSegment(sketch, "E31.38.5.0", {"start": v(-72.43, 36.91) * mm, "end": v(-72.43, 36.9) * mm});
            skLineSegment(sketch, "E31.41.5.0", {"start": v(-72.44, 36.9) * mm, "end": v(-72.43, 36.9) * mm});
            skArc(sketch, "E31.2.6.0", {"start": v(-69.74, 13.94) * mm, "mid": v(-69.82, 14.4) * mm, "end": v(-70.2, 14.68) * mm});
            skLineSegment(sketch, "E31.4.6.0", {"start": v(-74.4, 15.8) * mm, "end": v(-70.2, 14.68) * mm});
            skLineSegment(sketch, "E31.7.6.0", {"start": v(-72.33, 23.5) * mm, "end": v(-68.13, 22.39) * mm});
            skPoint(sketch, "E31.10.6.0", {"position": v(-78.44, 21.28) * mm});
            skPoint(sketch, "E31.11.6.0", {"position": v(-74.53, 15.84) * mm});
            skPoint(sketch, "E31.12.6.0", {"position": v(-78.58, 20.8) * mm});
            skArc(sketch, "E31.13.6.0", {"start": v(-74.65, 15.94) * mm, "mid": v(-76.73, 18.1) * mm, "end": v(-78.45, 20.58) * mm});
            skPoint(sketch, "E31.17.6.0", {"position": v(-72.47, 23.55) * mm});
            skArc(sketch, "E31.18.6.0", {"start": v(-72.62, 23.52) * mm, "mid": v(-75.5, 22.68) * mm, "end": v(-78.23, 21.4) * mm});
            skArc(sketch, "E31.22.6.0", {"start": v(-78.23, 21.4) * mm, "mid": v(-78.4, 21.25) * mm, "end": v(-78.52, 21.05) * mm});
            skArc(sketch, "E31.26.6.0", {"start": v(-78.52, 21.03) * mm, "mid": v(-78.53, 20.8) * mm, "end": v(-78.45, 20.58) * mm});
            skArc(sketch, "E31.30.6.0", {"start": v(-72.33, 23.5) * mm, "mid": v(-72.47, 23.53) * mm, "end": v(-72.62, 23.52) * mm});
            skArc(sketch, "E31.34.6.0", {"start": v(-74.65, 15.94) * mm, "mid": v(-74.53, 15.86) * mm, "end": v(-74.4, 15.8) * mm});
            skLineSegment(sketch, "E31.38.6.0", {"start": v(-78.52, 21.05) * mm, "end": v(-78.52, 21.04) * mm});
            skLineSegment(sketch, "E31.41.6.0", {"start": v(-78.52, 21.03) * mm, "end": v(-78.52, 21.04) * mm});
            skArc(sketch, "E31.2.7.0", {"start": v(-71.11, -0.86) * mm, "mid": v(-71.3, -0.43) * mm, "end": v(-71.72, -0.23) * mm});
            skLineSegment(sketch, "E31.4.7.0", {"start": v(-76.05, 0) * mm, "end": v(-71.72, -0.23) * mm});
            skLineSegment(sketch, "E31.7.7.0", {"start": v(-75.63, 7.96) * mm, "end": v(-71.3, 7.73) * mm});
            skPoint(sketch, "E31.10.7.0", {"position": v(-81.15, 4.5) * mm});
            skPoint(sketch, "E31.11.7.0", {"position": v(-76.2, 0) * mm});
            skPoint(sketch, "E31.12.7.0", {"position": v(-81.18, 4) * mm});
            skArc(sketch, "E31.13.7.0", {"start": v(-76.33, 0.07) * mm, "mid": v(-78.82, 1.76) * mm, "end": v(-81.02, 3.82) * mm});
            skPoint(sketch, "E31.17.7.0", {"position": v(-75.78, 7.97) * mm});
            skArc(sketch, "E31.18.7.0", {"start": v(-75.92, 7.9) * mm, "mid": v(-78.57, 6.49) * mm, "end": v(-80.97, 4.67) * mm});
            skArc(sketch, "E31.22.7.0", {"start": v(-80.97, 4.67) * mm, "mid": v(-81.11, 4.49) * mm, "end": v(-81.18, 4.26) * mm});
            skArc(sketch, "E31.26.7.0", {"start": v(-81.18, 4.24) * mm, "mid": v(-81.14, 4.02) * mm, "end": v(-81.02, 3.82) * mm});
            skArc(sketch, "E31.30.7.0", {"start": v(-75.63, 7.96) * mm, "mid": v(-75.78, 7.95) * mm, "end": v(-75.92, 7.9) * mm});
            skArc(sketch, "E31.34.7.0", {"start": v(-76.33, 0.07) * mm, "mid": v(-76.2, 0.02) * mm, "end": v(-76.05, 0) * mm});
            skLineSegment(sketch, "E31.38.7.0", {"start": v(-81.18, 4.26) * mm, "end": v(-81.18, 4.25) * mm});
            skLineSegment(sketch, "E31.41.7.0", {"start": v(-81.18, 4.24) * mm, "end": v(-81.18, 4.25) * mm});
            skArc(sketch, "E31.2.8.0", {"start": v(-69.38, -15.63) * mm, "mid": v(-69.64, -15.24) * mm, "end": v(-70.1, -15.14) * mm});
            skLineSegment(sketch, "E31.4.8.0", {"start": v(-74.39, -15.82) * mm, "end": v(-70.1, -15.14) * mm});
            skLineSegment(sketch, "E31.7.8.0", {"start": v(-75.64, -7.94) * mm, "end": v(-71.35, -7.26) * mm});
            skPoint(sketch, "E31.10.8.0", {"position": v(-80.32, -12.46) * mm});
            skPoint(sketch, "E31.11.8.0", {"position": v(-74.53, -15.84) * mm});
            skPoint(sketch, "E31.12.8.0", {"position": v(-80.24, -12.96) * mm});
            skArc(sketch, "E31.13.8.0", {"start": v(-74.68, -15.8) * mm, "mid": v(-77.47, -14.67) * mm, "end": v(-80.04, -13.11) * mm});
            skPoint(sketch, "E31.17.8.0", {"position": v(-75.78, -7.97) * mm});
            skArc(sketch, "E31.18.8.0", {"start": v(-75.9, -8.05) * mm, "mid": v(-78.2, -9.99) * mm, "end": v(-80.17, -12.26) * mm});
            skArc(sketch, "E31.22.8.0", {"start": v(-80.17, -12.26) * mm, "mid": v(-80.27, -12.47) * mm, "end": v(-80.3, -12.7) * mm});
            skArc(sketch, "E31.26.8.0", {"start": v(-80.29, -12.73) * mm, "mid": v(-80.2, -12.94) * mm, "end": v(-80.04, -13.11) * mm});
            skArc(sketch, "E31.30.8.0", {"start": v(-75.64, -7.94) * mm, "mid": v(-75.78, -7.98) * mm, "end": v(-75.9, -8.05) * mm});
            skArc(sketch, "E31.34.8.0", {"start": v(-74.68, -15.8) * mm, "mid": v(-74.53, -15.83) * mm, "end": v(-74.39, -15.82) * mm});
            skLineSegment(sketch, "E31.38.8.0", {"start": v(-80.3, -12.7) * mm, "end": v(-80.3, -12.72) * mm});
            skLineSegment(sketch, "E31.41.8.0", {"start": v(-80.29, -12.73) * mm, "end": v(-80.3, -12.72) * mm});
            skArc(sketch, "E31.2.9.0", {"start": v(-64.62, -29.71) * mm, "mid": v(-64.95, -29.39) * mm, "end": v(-65.42, -29.38) * mm});
            skLineSegment(sketch, "E31.4.9.0", {"start": v(-69.47, -30.94) * mm, "end": v(-65.42, -29.38) * mm});
            skLineSegment(sketch, "E31.7.9.0", {"start": v(-72.33, -23.5) * mm, "end": v(-68.28, -21.94) * mm});
            skPoint(sketch, "E31.10.9.0", {"position": v(-75.97, -28.9) * mm});
            skPoint(sketch, "E31.11.9.0", {"position": v(-69.61, -31) * mm});
            skPoint(sketch, "E31.12.9.0", {"position": v(-75.8, -29.36) * mm});
            skArc(sketch, "E31.13.9.0", {"start": v(-69.76, -30.98) * mm, "mid": v(-72.72, -30.45) * mm, "end": v(-75.56, -29.47) * mm});
            skPoint(sketch, "E31.17.9.0", {"position": v(-72.47, -23.55) * mm});
            skArc(sketch, "E31.18.9.0", {"start": v(-72.57, -23.66) * mm, "mid": v(-74.42, -26.03) * mm, "end": v(-75.87, -28.67) * mm});
            skArc(sketch, "E31.22.9.0", {"start": v(-75.87, -28.67) * mm, "mid": v(-75.93, -28.9) * mm, "end": v(-75.9, -29.12) * mm});
            skArc(sketch, "E31.26.9.0", {"start": v(-75.89, -29.14) * mm, "mid": v(-75.76, -29.33) * mm, "end": v(-75.56, -29.47) * mm});
            skArc(sketch, "E31.30.9.0", {"start": v(-72.33, -23.5) * mm, "mid": v(-72.46, -23.56) * mm, "end": v(-72.57, -23.66) * mm});
            skArc(sketch, "E31.34.9.0", {"start": v(-69.76, -30.98) * mm, "mid": v(-69.62, -30.98) * mm, "end": v(-69.47, -30.94) * mm});
            skLineSegment(sketch, "E31.38.9.0", {"start": v(-75.9, -29.12) * mm, "end": v(-75.9, -29.13) * mm});
            skLineSegment(sketch, "E31.41.9.0", {"start": v(-75.89, -29.14) * mm, "end": v(-75.9, -29.13) * mm});
            skArc(sketch, "E31.2.10.0", {"start": v(-57.03, -42.5) * mm, "mid": v(-57.42, -42.25) * mm, "end": v(-57.88, -42.34) * mm});
            skLineSegment(sketch, "E31.4.10.0", {"start": v(-61.52, -44.7) * mm, "end": v(-57.88, -42.34) * mm});
            skLineSegment(sketch, "E31.7.10.0", {"start": v(-65.87, -38.02) * mm, "end": v(-62.23, -35.65) * mm});
            skPoint(sketch, "E31.10.10.0", {"position": v(-68.3, -44.06) * mm});
            skPoint(sketch, "E31.11.10.0", {"position": v(-61.65, -44.79) * mm});
            skPoint(sketch, "E31.12.10.0", {"position": v(-68.03, -44.48) * mm});
            skArc(sketch, "E31.13.10.0", {"start": v(-61.8, -44.8) * mm, "mid": v(-64.8, -44.9) * mm, "end": v(-67.79, -44.53) * mm});
            skPoint(sketch, "E31.17.10.0", {"position": v(-66, -38.1) * mm});
            skArc(sketch, "E31.18.10.0", {"start": v(-66.07, -38.23) * mm, "mid": v(-67.38, -40.94) * mm, "end": v(-68.25, -43.81) * mm});
            skArc(sketch, "E31.22.10.0", {"start": v(-68.25, -43.81) * mm, "mid": v(-68.26, -44.05) * mm, "end": v(-68.18, -44.27) * mm});
            skArc(sketch, "E31.26.10.0", {"start": v(-68.17, -44.28) * mm, "mid": v(-68, -44.44) * mm, "end": v(-67.79, -44.53) * mm});
            skArc(sketch, "E31.30.10.0", {"start": v(-65.87, -38.02) * mm, "mid": v(-65.98, -38.11) * mm, "end": v(-66.07, -38.23) * mm});
            skArc(sketch, "E31.34.10.0", {"start": v(-61.8, -44.8) * mm, "mid": v(-61.65, -44.77) * mm, "end": v(-61.52, -44.7) * mm});
            skLineSegment(sketch, "E31.38.10.0", {"start": v(-68.18, -44.27) * mm, "end": v(-68.18, -44.28) * mm});
            skLineSegment(sketch, "E31.41.10.0", {"start": v(-68.17, -44.28) * mm, "end": v(-68.18, -44.28) * mm});
            skArc(sketch, "E31.2.11.0", {"start": v(-46.94, -53.42) * mm, "mid": v(-47.38, -53.27) * mm, "end": v(-47.81, -53.45) * mm});
            skLineSegment(sketch, "E31.4.11.0", {"start": v(-50.88, -56.52) * mm, "end": v(-47.81, -53.45) * mm});
            skLineSegment(sketch, "E31.7.11.0", {"start": v(-56.52, -50.88) * mm, "end": v(-53.45, -47.81) * mm});
            skPoint(sketch, "E31.10.11.0", {"position": v(-57.65, -57.3) * mm});
            skPoint(sketch, "E31.11.11.0", {"position": v(-50.99, -56.63) * mm});
            skPoint(sketch, "E31.12.11.0", {"position": v(-57.3, -57.65) * mm});
            skArc(sketch, "E31.13.11.0", {"start": v(-51.13, -56.68) * mm, "mid": v(-54.05, -57.4) * mm, "end": v(-57.05, -57.65) * mm});
            skPoint(sketch, "E31.17.11.0", {"position": v(-56.63, -50.99) * mm});
            skArc(sketch, "E31.18.11.0", {"start": v(-56.68, -51.13) * mm, "mid": v(-57.4, -54.05) * mm, "end": v(-57.65, -57.05) * mm});
            skArc(sketch, "E31.22.11.0", {"start": v(-57.65, -57.05) * mm, "mid": v(-57.61, -57.28) * mm, "end": v(-57.49, -57.48) * mm});
            skArc(sketch, "E31.26.11.0", {"start": v(-57.48, -57.49) * mm, "mid": v(-57.28, -57.61) * mm, "end": v(-57.05, -57.65) * mm});
            skArc(sketch, "E31.30.11.0", {"start": v(-56.52, -50.88) * mm, "mid": v(-56.61, -51) * mm, "end": v(-56.68, -51.13) * mm});
            skArc(sketch, "E31.34.11.0", {"start": v(-51.13, -56.68) * mm, "mid": v(-51, -56.61) * mm, "end": v(-50.88, -56.52) * mm});
            skLineSegment(sketch, "E31.38.11.0", {"start": v(-57.49, -57.48) * mm, "end": v(-57.48, -57.48) * mm});
            skLineSegment(sketch, "E31.41.11.0", {"start": v(-57.48, -57.49) * mm, "end": v(-57.48, -57.48) * mm});
            skArc(sketch, "E31.2.12.0", {"start": v(-34.81, -62.02) * mm, "mid": v(-35.27, -61.96) * mm, "end": v(-35.65, -62.23) * mm});
            skLineSegment(sketch, "E31.4.12.0", {"start": v(-38.02, -65.87) * mm, "end": v(-35.65, -62.23) * mm});
            skLineSegment(sketch, "E31.7.12.0", {"start": v(-44.7, -61.52) * mm, "end": v(-42.34, -57.88) * mm});
            skPoint(sketch, "E31.10.12.0", {"position": v(-44.48, -68.03) * mm});
            skPoint(sketch, "E31.11.12.0", {"position": v(-38.1, -66) * mm});
            skPoint(sketch, "E31.12.12.0", {"position": v(-44.06, -68.3) * mm});
            skArc(sketch, "E31.13.12.0", {"start": v(-38.23, -66.07) * mm, "mid": v(-40.94, -67.38) * mm, "end": v(-43.81, -68.25) * mm});
            skPoint(sketch, "E31.17.12.0", {"position": v(-44.79, -61.65) * mm});
            skArc(sketch, "E31.18.12.0", {"start": v(-44.8, -61.8) * mm, "mid": v(-44.9, -64.8) * mm, "end": v(-44.53, -67.79) * mm});
            skArc(sketch, "E31.22.12.0", {"start": v(-44.53, -67.79) * mm, "mid": v(-44.44, -68) * mm, "end": v(-44.28, -68.17) * mm});
            skArc(sketch, "E31.26.12.0", {"start": v(-44.27, -68.18) * mm, "mid": v(-44.05, -68.26) * mm, "end": v(-43.81, -68.25) * mm});
            skArc(sketch, "E31.30.12.0", {"start": v(-44.7, -61.52) * mm, "mid": v(-44.77, -61.65) * mm, "end": v(-44.8, -61.8) * mm});
            skArc(sketch, "E31.34.12.0", {"start": v(-38.23, -66.07) * mm, "mid": v(-38.11, -65.98) * mm, "end": v(-38.02, -65.87) * mm});
            skLineSegment(sketch, "E31.38.12.0", {"start": v(-44.28, -68.17) * mm, "end": v(-44.28, -68.18) * mm});
            skLineSegment(sketch, "E31.41.12.0", {"start": v(-44.27, -68.18) * mm, "end": v(-44.28, -68.18) * mm});
            skArc(sketch, "E31.2.13.0", {"start": v(-21.16, -67.9) * mm, "mid": v(-21.62, -67.94) * mm, "end": v(-21.94, -68.28) * mm});
            skLineSegment(sketch, "E31.4.13.0", {"start": v(-23.5, -72.33) * mm, "end": v(-21.94, -68.28) * mm});
            skLineSegment(sketch, "E31.7.13.0", {"start": v(-30.94, -69.47) * mm, "end": v(-29.38, -65.42) * mm});
            skPoint(sketch, "E31.10.13.0", {"position": v(-29.36, -75.8) * mm});
            skPoint(sketch, "E31.11.13.0", {"position": v(-23.55, -72.47) * mm});
            skPoint(sketch, "E31.12.13.0", {"position": v(-28.9, -75.97) * mm});
            skArc(sketch, "E31.13.13.0", {"start": v(-23.66, -72.57) * mm, "mid": v(-26.03, -74.42) * mm, "end": v(-28.67, -75.87) * mm});
            skPoint(sketch, "E31.17.13.0", {"position": v(-31, -69.61) * mm});
            skArc(sketch, "E31.18.13.0", {"start": v(-30.98, -69.76) * mm, "mid": v(-30.45, -72.72) * mm, "end": v(-29.47, -75.56) * mm});
            skArc(sketch, "E31.22.13.0", {"start": v(-29.47, -75.56) * mm, "mid": v(-29.33, -75.76) * mm, "end": v(-29.14, -75.89) * mm});
            skArc(sketch, "E31.26.13.0", {"start": v(-29.12, -75.9) * mm, "mid": v(-28.9, -75.93) * mm, "end": v(-28.67, -75.87) * mm});
            skArc(sketch, "E31.30.13.0", {"start": v(-30.94, -69.47) * mm, "mid": v(-30.98, -69.62) * mm, "end": v(-30.98, -69.76) * mm});
            skArc(sketch, "E31.34.13.0", {"start": v(-23.66, -72.57) * mm, "mid": v(-23.56, -72.46) * mm, "end": v(-23.5, -72.33) * mm});
            skLineSegment(sketch, "E31.38.13.0", {"start": v(-29.14, -75.89) * mm, "end": v(-29.13, -75.9) * mm});
            skLineSegment(sketch, "E31.41.13.0", {"start": v(-29.12, -75.9) * mm, "end": v(-29.13, -75.9) * mm});
            skArc(sketch, "E31.2.14.0", {"start": v(-6.58, -70.82) * mm, "mid": v(-7.03, -70.95) * mm, "end": v(-7.26, -71.35) * mm});
            skLineSegment(sketch, "E31.4.14.0", {"start": v(-7.94, -75.64) * mm, "end": v(-7.26, -71.35) * mm});
            skLineSegment(sketch, "E31.7.14.0", {"start": v(-15.82, -74.39) * mm, "end": v(-15.14, -70.1) * mm});
            skPoint(sketch, "E31.10.14.0", {"position": v(-12.96, -80.24) * mm});
            skPoint(sketch, "E31.11.14.0", {"position": v(-7.97, -75.78) * mm});
            skPoint(sketch, "E31.12.14.0", {"position": v(-12.46, -80.32) * mm});
            skArc(sketch, "E31.13.14.0", {"start": v(-8.05, -75.9) * mm, "mid": v(-9.99, -78.2) * mm, "end": v(-12.26, -80.17) * mm});
            skPoint(sketch, "E31.17.14.0", {"position": v(-15.84, -74.53) * mm});
            skArc(sketch, "E31.18.14.0", {"start": v(-15.8, -74.68) * mm, "mid": v(-14.67, -77.47) * mm, "end": v(-13.11, -80.04) * mm});
            skArc(sketch, "E31.22.14.0", {"start": v(-13.11, -80.04) * mm, "mid": v(-12.94, -80.2) * mm, "end": v(-12.73, -80.29) * mm});
            skArc(sketch, "E31.26.14.0", {"start": v(-12.7, -80.3) * mm, "mid": v(-12.47, -80.27) * mm, "end": v(-12.26, -80.17) * mm});
            skArc(sketch, "E31.30.14.0", {"start": v(-15.82, -74.39) * mm, "mid": v(-15.83, -74.53) * mm, "end": v(-15.8, -74.68) * mm});
            skArc(sketch, "E31.34.14.0", {"start": v(-8.05, -75.9) * mm, "mid": v(-7.98, -75.78) * mm, "end": v(-7.94, -75.64) * mm});
            skLineSegment(sketch, "E31.38.14.0", {"start": v(-12.73, -80.29) * mm, "end": v(-12.72, -80.3) * mm});
            skLineSegment(sketch, "E31.41.14.0", {"start": v(-12.7, -80.3) * mm, "end": v(-12.72, -80.3) * mm});
            skArc(sketch, "E31.2.15.0", {"start": v(8.3, -70.64) * mm, "mid": v(7.88, -70.86) * mm, "end": v(7.73, -71.3) * mm});
            skLineSegment(sketch, "E31.4.15.0", {"start": v(7.96, -75.63) * mm, "end": v(7.73, -71.3) * mm});
            skLineSegment(sketch, "E31.7.15.0", {"start": v(0, -76.05) * mm, "end": v(-0.23, -71.72) * mm});
            skPoint(sketch, "E31.10.15.0", {"position": v(4, -81.18) * mm});
            skPoint(sketch, "E31.11.15.0", {"position": v(7.97, -75.78) * mm});
            skPoint(sketch, "E31.12.15.0", {"position": v(4.5, -81.15) * mm});
            skArc(sketch, "E31.13.15.0", {"start": v(7.9, -75.92) * mm, "mid": v(6.49, -78.57) * mm, "end": v(4.67, -80.97) * mm});
            skPoint(sketch, "E31.17.15.0", {"position": v(0, -76.2) * mm});
            skArc(sketch, "E31.18.15.0", {"start": v(0.07, -76.33) * mm, "mid": v(1.76, -78.82) * mm, "end": v(3.82, -81.02) * mm});
            skArc(sketch, "E31.22.15.0", {"start": v(3.82, -81.02) * mm, "mid": v(4.02, -81.14) * mm, "end": v(4.24, -81.18) * mm});
            skArc(sketch, "E31.26.15.0", {"start": v(4.26, -81.18) * mm, "mid": v(4.49, -81.11) * mm, "end": v(4.67, -80.97) * mm});
            skArc(sketch, "E31.30.15.0", {"start": v(0, -76.05) * mm, "mid": v(0.02, -76.2) * mm, "end": v(0.07, -76.33) * mm});
            skArc(sketch, "E31.34.15.0", {"start": v(7.9, -75.92) * mm, "mid": v(7.95, -75.78) * mm, "end": v(7.96, -75.63) * mm});
            skLineSegment(sketch, "E31.38.15.0", {"start": v(4.24, -81.18) * mm, "end": v(4.25, -81.18) * mm});
            skLineSegment(sketch, "E31.41.15.0", {"start": v(4.26, -81.18) * mm, "end": v(4.25, -81.18) * mm});
            skArc(sketch, "E31.2.16.0", {"start": v(22.8, -67.37) * mm, "mid": v(22.44, -67.67) * mm, "end": v(22.39, -68.13) * mm});
            skLineSegment(sketch, "E31.4.16.0", {"start": v(23.5, -72.33) * mm, "end": v(22.39, -68.13) * mm});
            skLineSegment(sketch, "E31.7.16.0", {"start": v(15.8, -74.4) * mm, "end": v(14.68, -70.2) * mm});
            skPoint(sketch, "E31.10.16.0", {"position": v(20.8, -78.58) * mm});
            skPoint(sketch, "E31.11.16.0", {"position": v(23.55, -72.47) * mm});
            skPoint(sketch, "E31.12.16.0", {"position": v(21.28, -78.44) * mm});
            skArc(sketch, "E31.13.16.0", {"start": v(23.52, -72.62) * mm, "mid": v(22.68, -75.5) * mm, "end": v(21.4, -78.23) * mm});
            skPoint(sketch, "E31.17.16.0", {"position": v(15.84, -74.53) * mm});
            skArc(sketch, "E31.18.16.0", {"start": v(15.94, -74.65) * mm, "mid": v(18.1, -76.73) * mm, "end": v(20.58, -78.45) * mm});
            skArc(sketch, "E31.22.16.0", {"start": v(20.58, -78.45) * mm, "mid": v(20.8, -78.53) * mm, "end": v(21.03, -78.52) * mm});
            skArc(sketch, "E31.26.16.0", {"start": v(21.05, -78.52) * mm, "mid": v(21.25, -78.4) * mm, "end": v(21.4, -78.23) * mm});
            skArc(sketch, "E31.30.16.0", {"start": v(15.8, -74.4) * mm, "mid": v(15.86, -74.53) * mm, "end": v(15.94, -74.65) * mm});
            skArc(sketch, "E31.34.16.0", {"start": v(23.52, -72.62) * mm, "mid": v(23.53, -72.47) * mm, "end": v(23.5, -72.33) * mm});
            skLineSegment(sketch, "E31.38.16.0", {"start": v(21.03, -78.52) * mm, "end": v(21.04, -78.52) * mm});
            skLineSegment(sketch, "E31.41.16.0", {"start": v(21.05, -78.52) * mm, "end": v(21.04, -78.52) * mm});
            skArc(sketch, "E31.2.17.0", {"start": v(36.3, -61.16) * mm, "mid": v(36.02, -61.53) * mm, "end": v(36.06, -62) * mm});
            skLineSegment(sketch, "E31.4.17.0", {"start": v(38.03, -65.86) * mm, "end": v(36.06, -62) * mm});
            skLineSegment(sketch, "E31.7.17.0", {"start": v(30.93, -69.48) * mm, "end": v(28.96, -65.61) * mm});
            skPoint(sketch, "E31.10.17.0", {"position": v(36.67, -72.54) * mm});
            skPoint(sketch, "E31.11.17.0", {"position": v(38.1, -66) * mm});
            skPoint(sketch, "E31.12.17.0", {"position": v(37.13, -72.3) * mm});
            skArc(sketch, "E31.13.17.0", {"start": v(38.1, -66.14) * mm, "mid": v(37.89, -69.14) * mm, "end": v(37.2, -72.07) * mm});
            skPoint(sketch, "E31.17.17.0", {"position": v(31, -69.61) * mm});
            skArc(sketch, "E31.18.17.0", {"start": v(31.11, -69.7) * mm, "mid": v(33.67, -71.3) * mm, "end": v(36.44, -72.46) * mm});
            skArc(sketch, "E31.22.17.0", {"start": v(36.44, -72.46) * mm, "mid": v(36.67, -72.5) * mm, "end": v(36.9, -72.44) * mm});
            skArc(sketch, "E31.26.17.0", {"start": v(36.91, -72.43) * mm, "mid": v(37.1, -72.28) * mm, "end": v(37.2, -72.07) * mm});
            skArc(sketch, "E31.30.17.0", {"start": v(30.93, -69.48) * mm, "mid": v(31, -69.6) * mm, "end": v(31.11, -69.7) * mm});
            skArc(sketch, "E31.34.17.0", {"start": v(38.1, -66.14) * mm, "mid": v(38.08, -66) * mm, "end": v(38.03, -65.86) * mm});
            skLineSegment(sketch, "E31.38.17.0", {"start": v(36.9, -72.44) * mm, "end": v(36.9, -72.43) * mm});
            skLineSegment(sketch, "E31.41.17.0", {"start": v(36.91, -72.43) * mm, "end": v(36.9, -72.43) * mm});
            skArc(sketch, "E31.2.18.0", {"start": v(48.23, -52.27) * mm, "mid": v(48.02, -52.7) * mm, "end": v(48.16, -53.14) * mm});
            skLineSegment(sketch, "E31.4.18.0", {"start": v(50.9, -56.51) * mm, "end": v(48.16, -53.14) * mm});
            skLineSegment(sketch, "E31.7.18.0", {"start": v(44.7, -61.53) * mm, "end": v(41.96, -58.16) * mm});
            skPoint(sketch, "E31.10.18.0", {"position": v(50.95, -63.33) * mm});
            skPoint(sketch, "E31.11.18.0", {"position": v(50.99, -56.63) * mm});
            skPoint(sketch, "E31.12.18.0", {"position": v(51.35, -63) * mm});
            skArc(sketch, "E31.13.18.0", {"start": v(51.02, -56.78) * mm, "mid": v(51.43, -59.75) * mm, "end": v(51.37, -62.76) * mm});
            skPoint(sketch, "E31.17.18.0", {"position": v(44.79, -61.65) * mm});
            skArc(sketch, "E31.18.18.0", {"start": v(44.93, -61.71) * mm, "mid": v(47.75, -62.73) * mm, "end": v(50.7, -63.3) * mm});
            skArc(sketch, "E31.22.18.0", {"start": v(50.7, -63.3) * mm, "mid": v(50.94, -63.28) * mm, "end": v(51.15, -63.18) * mm});
            skArc(sketch, "E31.26.18.0", {"start": v(51.17, -63.17) * mm, "mid": v(51.3, -62.98) * mm, "end": v(51.37, -62.76) * mm});
            skArc(sketch, "E31.30.18.0", {"start": v(44.7, -61.53) * mm, "mid": v(44.8, -61.63) * mm, "end": v(44.93, -61.71) * mm});
            skArc(sketch, "E31.34.18.0", {"start": v(51.02, -56.78) * mm, "mid": v(50.97, -56.64) * mm, "end": v(50.9, -56.51) * mm});
            skLineSegment(sketch, "E31.38.18.0", {"start": v(51.15, -63.18) * mm, "end": v(51.16, -63.18) * mm});
            skLineSegment(sketch, "E31.41.18.0", {"start": v(51.17, -63.17) * mm, "end": v(51.16, -63.18) * mm});
            skArc(sketch, "E31.2.19.0", {"start": v(58.04, -41.1) * mm, "mid": v(57.93, -41.56) * mm, "end": v(58.16, -41.96) * mm});
            skLineSegment(sketch, "E31.4.19.0", {"start": v(61.53, -44.7) * mm, "end": v(58.16, -41.96) * mm});
            skLineSegment(sketch, "E31.7.19.0", {"start": v(56.51, -50.9) * mm, "end": v(53.14, -48.16) * mm});
            skPoint(sketch, "E31.10.19.0", {"position": v(63, -51.35) * mm});
            skPoint(sketch, "E31.11.19.0", {"position": v(61.65, -44.79) * mm});
            skPoint(sketch, "E31.12.19.0", {"position": v(63.33, -50.95) * mm});
            skArc(sketch, "E31.13.19.0", {"start": v(61.71, -44.93) * mm, "mid": v(62.73, -47.75) * mm, "end": v(63.3, -50.7) * mm});
            skPoint(sketch, "E31.17.19.0", {"position": v(56.63, -50.99) * mm});
            skArc(sketch, "E31.18.19.0", {"start": v(56.78, -51.02) * mm, "mid": v(59.75, -51.43) * mm, "end": v(62.76, -51.37) * mm});
            skArc(sketch, "E31.22.19.0", {"start": v(62.76, -51.37) * mm, "mid": v(62.98, -51.3) * mm, "end": v(63.17, -51.17) * mm});
            skArc(sketch, "E31.26.19.0", {"start": v(63.18, -51.15) * mm, "mid": v(63.28, -50.94) * mm, "end": v(63.3, -50.7) * mm});
            skArc(sketch, "E31.30.19.0", {"start": v(56.51, -50.9) * mm, "mid": v(56.64, -50.97) * mm, "end": v(56.78, -51.02) * mm});
            skArc(sketch, "E31.34.19.0", {"start": v(61.71, -44.93) * mm, "mid": v(61.63, -44.8) * mm, "end": v(61.53, -44.7) * mm});
            skLineSegment(sketch, "E31.38.19.0", {"start": v(63.17, -51.17) * mm, "end": v(63.18, -51.16) * mm});
            skLineSegment(sketch, "E31.41.19.0", {"start": v(63.18, -51.15) * mm, "end": v(63.18, -51.16) * mm});
            skArc(sketch, "E31.2.20.0", {"start": v(65.32, -28.14) * mm, "mid": v(65.3, -28.6) * mm, "end": v(65.61, -28.96) * mm});
            skLineSegment(sketch, "E31.4.20.0", {"start": v(69.48, -30.93) * mm, "end": v(65.61, -28.96) * mm});
            skLineSegment(sketch, "E31.7.20.0", {"start": v(65.86, -38.03) * mm, "end": v(62, -36.06) * mm});
            skPoint(sketch, "E31.10.20.0", {"position": v(72.3, -37.13) * mm});
            skPoint(sketch, "E31.11.20.0", {"position": v(69.61, -31) * mm});
            skPoint(sketch, "E31.12.20.0", {"position": v(72.54, -36.67) * mm});
            skArc(sketch, "E31.13.20.0", {"start": v(69.7, -31.11) * mm, "mid": v(71.3, -33.67) * mm, "end": v(72.46, -36.44) * mm});
            skPoint(sketch, "E31.17.20.0", {"position": v(66, -38.1) * mm});
            skArc(sketch, "E31.18.20.0", {"start": v(66.14, -38.1) * mm, "mid": v(69.14, -37.89) * mm, "end": v(72.07, -37.2) * mm});
            skArc(sketch, "E31.22.20.0", {"start": v(72.07, -37.2) * mm, "mid": v(72.28, -37.1) * mm, "end": v(72.43, -36.91) * mm});
            skArc(sketch, "E31.26.20.0", {"start": v(72.44, -36.9) * mm, "mid": v(72.5, -36.67) * mm, "end": v(72.46, -36.44) * mm});
            skArc(sketch, "E31.30.20.0", {"start": v(65.86, -38.03) * mm, "mid": v(66, -38.08) * mm, "end": v(66.14, -38.1) * mm});
            skArc(sketch, "E31.34.20.0", {"start": v(69.7, -31.11) * mm, "mid": v(69.6, -31) * mm, "end": v(69.48, -30.93) * mm});
            skLineSegment(sketch, "E31.38.20.0", {"start": v(72.43, -36.91) * mm, "end": v(72.43, -36.9) * mm});
            skLineSegment(sketch, "E31.41.20.0", {"start": v(72.44, -36.9) * mm, "end": v(72.43, -36.9) * mm});
            skArc(sketch, "E31.2.21.0", {"start": v(69.74, -13.94) * mm, "mid": v(69.82, -14.4) * mm, "end": v(70.2, -14.68) * mm});
            skLineSegment(sketch, "E31.4.21.0", {"start": v(74.4, -15.8) * mm, "end": v(70.2, -14.68) * mm});
            skLineSegment(sketch, "E31.7.21.0", {"start": v(72.33, -23.5) * mm, "end": v(68.13, -22.39) * mm});
            skPoint(sketch, "E31.10.21.0", {"position": v(78.44, -21.28) * mm});
            skPoint(sketch, "E31.11.21.0", {"position": v(74.53, -15.84) * mm});
            skPoint(sketch, "E31.12.21.0", {"position": v(78.58, -20.8) * mm});
            skArc(sketch, "E31.13.21.0", {"start": v(74.65, -15.94) * mm, "mid": v(76.73, -18.1) * mm, "end": v(78.45, -20.58) * mm});
            skPoint(sketch, "E31.17.21.0", {"position": v(72.47, -23.55) * mm});
            skArc(sketch, "E31.18.21.0", {"start": v(72.62, -23.52) * mm, "mid": v(75.5, -22.68) * mm, "end": v(78.23, -21.4) * mm});
            skArc(sketch, "E31.22.21.0", {"start": v(78.23, -21.4) * mm, "mid": v(78.4, -21.25) * mm, "end": v(78.52, -21.05) * mm});
            skArc(sketch, "E31.26.21.0", {"start": v(78.52, -21.03) * mm, "mid": v(78.53, -20.8) * mm, "end": v(78.45, -20.58) * mm});
            skArc(sketch, "E31.30.21.0", {"start": v(72.33, -23.5) * mm, "mid": v(72.47, -23.53) * mm, "end": v(72.62, -23.52) * mm});
            skArc(sketch, "E31.34.21.0", {"start": v(74.65, -15.94) * mm, "mid": v(74.53, -15.86) * mm, "end": v(74.4, -15.8) * mm});
            skLineSegment(sketch, "E31.38.21.0", {"start": v(78.52, -21.05) * mm, "end": v(78.52, -21.04) * mm});
            skLineSegment(sketch, "E31.41.21.0", {"start": v(78.52, -21.03) * mm, "end": v(78.52, -21.04) * mm});
            skArc(sketch, "E31.2.22.0", {"start": v(71.11, 0.86) * mm, "mid": v(71.3, 0.43) * mm, "end": v(71.72, 0.23) * mm});
            skLineSegment(sketch, "E31.4.22.0", {"start": v(76.05, 0) * mm, "end": v(71.72, 0.23) * mm});
            skLineSegment(sketch, "E31.7.22.0", {"start": v(75.63, -7.96) * mm, "end": v(71.3, -7.73) * mm});
            skPoint(sketch, "E31.10.22.0", {"position": v(81.15, -4.5) * mm});
            skPoint(sketch, "E31.11.22.0", {"position": v(76.2, 0) * mm});
            skPoint(sketch, "E31.12.22.0", {"position": v(81.18, -4) * mm});
            skArc(sketch, "E31.13.22.0", {"start": v(76.33, -0.07) * mm, "mid": v(78.82, -1.76) * mm, "end": v(81.02, -3.82) * mm});
            skPoint(sketch, "E31.17.22.0", {"position": v(75.78, -7.97) * mm});
            skArc(sketch, "E31.18.22.0", {"start": v(75.92, -7.9) * mm, "mid": v(78.57, -6.49) * mm, "end": v(80.97, -4.67) * mm});
            skArc(sketch, "E31.22.22.0", {"start": v(80.97, -4.67) * mm, "mid": v(81.11, -4.49) * mm, "end": v(81.18, -4.26) * mm});
            skArc(sketch, "E31.26.22.0", {"start": v(81.18, -4.24) * mm, "mid": v(81.14, -4.02) * mm, "end": v(81.02, -3.82) * mm});
            skArc(sketch, "E31.30.22.0", {"start": v(75.63, -7.96) * mm, "mid": v(75.78, -7.95) * mm, "end": v(75.92, -7.9) * mm});
            skArc(sketch, "E31.34.22.0", {"start": v(76.33, -0.07) * mm, "mid": v(76.2, -0.02) * mm, "end": v(76.05, 0) * mm});
            skLineSegment(sketch, "E31.38.22.0", {"start": v(81.18, -4.26) * mm, "end": v(81.18, -4.25) * mm});
            skLineSegment(sketch, "E31.41.22.0", {"start": v(81.18, -4.24) * mm, "end": v(81.18, -4.25) * mm});
            skArc(sketch, "E31.2.23.0", {"start": v(69.38, 15.63) * mm, "mid": v(69.64, 15.24) * mm, "end": v(70.1, 15.14) * mm});
            skLineSegment(sketch, "E31.4.23.0", {"start": v(74.39, 15.82) * mm, "end": v(70.1, 15.14) * mm});
            skLineSegment(sketch, "E31.7.23.0", {"start": v(75.64, 7.94) * mm, "end": v(71.35, 7.26) * mm});
            skPoint(sketch, "E31.10.23.0", {"position": v(80.32, 12.46) * mm});
            skPoint(sketch, "E31.11.23.0", {"position": v(74.53, 15.84) * mm});
            skPoint(sketch, "E31.12.23.0", {"position": v(80.24, 12.96) * mm});
            skArc(sketch, "E31.13.23.0", {"start": v(74.68, 15.8) * mm, "mid": v(77.47, 14.67) * mm, "end": v(80.04, 13.11) * mm});
            skPoint(sketch, "E31.17.23.0", {"position": v(75.78, 7.97) * mm});
            skArc(sketch, "E31.18.23.0", {"start": v(75.9, 8.05) * mm, "mid": v(78.2, 9.99) * mm, "end": v(80.17, 12.26) * mm});
            skArc(sketch, "E31.22.23.0", {"start": v(80.17, 12.26) * mm, "mid": v(80.27, 12.47) * mm, "end": v(80.3, 12.7) * mm});
            skArc(sketch, "E31.26.23.0", {"start": v(80.29, 12.73) * mm, "mid": v(80.2, 12.94) * mm, "end": v(80.04, 13.11) * mm});
            skArc(sketch, "E31.30.23.0", {"start": v(75.64, 7.94) * mm, "mid": v(75.78, 7.98) * mm, "end": v(75.9, 8.05) * mm});
            skArc(sketch, "E31.34.23.0", {"start": v(74.68, 15.8) * mm, "mid": v(74.53, 15.83) * mm, "end": v(74.39, 15.82) * mm});
            skLineSegment(sketch, "E31.38.23.0", {"start": v(80.3, 12.7) * mm, "end": v(80.3, 12.72) * mm});
            skLineSegment(sketch, "E31.41.23.0", {"start": v(80.29, 12.73) * mm, "end": v(80.3, 12.72) * mm});
            skArc(sketch, "E31.2.24.0", {"start": v(64.62, 29.71) * mm, "mid": v(64.95, 29.39) * mm, "end": v(65.42, 29.38) * mm});
            skLineSegment(sketch, "E31.4.24.0", {"start": v(69.47, 30.94) * mm, "end": v(65.42, 29.38) * mm});
            skLineSegment(sketch, "E31.7.24.0", {"start": v(72.33, 23.5) * mm, "end": v(68.28, 21.94) * mm});
            skPoint(sketch, "E31.10.24.0", {"position": v(75.97, 28.9) * mm});
            skPoint(sketch, "E31.11.24.0", {"position": v(69.61, 31) * mm});
            skPoint(sketch, "E31.12.24.0", {"position": v(75.8, 29.36) * mm});
            skArc(sketch, "E31.13.24.0", {"start": v(69.76, 30.98) * mm, "mid": v(72.72, 30.45) * mm, "end": v(75.56, 29.47) * mm});
            skPoint(sketch, "E31.17.24.0", {"position": v(72.47, 23.55) * mm});
            skArc(sketch, "E31.18.24.0", {"start": v(72.57, 23.66) * mm, "mid": v(74.42, 26.03) * mm, "end": v(75.87, 28.67) * mm});
            skArc(sketch, "E31.22.24.0", {"start": v(75.87, 28.67) * mm, "mid": v(75.93, 28.9) * mm, "end": v(75.9, 29.12) * mm});
            skArc(sketch, "E31.26.24.0", {"start": v(75.89, 29.14) * mm, "mid": v(75.76, 29.33) * mm, "end": v(75.56, 29.47) * mm});
            skArc(sketch, "E31.30.24.0", {"start": v(72.33, 23.5) * mm, "mid": v(72.46, 23.56) * mm, "end": v(72.57, 23.66) * mm});
            skArc(sketch, "E31.34.24.0", {"start": v(69.76, 30.98) * mm, "mid": v(69.62, 30.98) * mm, "end": v(69.47, 30.94) * mm});
            skLineSegment(sketch, "E31.38.24.0", {"start": v(75.9, 29.12) * mm, "end": v(75.9, 29.13) * mm});
            skLineSegment(sketch, "E31.41.24.0", {"start": v(75.89, 29.14) * mm, "end": v(75.9, 29.13) * mm});
            skArc(sketch, "E31.2.25.0", {"start": v(57.03, 42.5) * mm, "mid": v(57.42, 42.25) * mm, "end": v(57.88, 42.34) * mm});
            skLineSegment(sketch, "E31.4.25.0", {"start": v(61.52, 44.7) * mm, "end": v(57.88, 42.34) * mm});
            skLineSegment(sketch, "E31.7.25.0", {"start": v(65.87, 38.02) * mm, "end": v(62.23, 35.65) * mm});
            skPoint(sketch, "E31.10.25.0", {"position": v(68.3, 44.06) * mm});
            skPoint(sketch, "E31.11.25.0", {"position": v(61.65, 44.79) * mm});
            skPoint(sketch, "E31.12.25.0", {"position": v(68.03, 44.48) * mm});
            skArc(sketch, "E31.13.25.0", {"start": v(61.8, 44.8) * mm, "mid": v(64.8, 44.9) * mm, "end": v(67.79, 44.53) * mm});
            skPoint(sketch, "E31.17.25.0", {"position": v(66, 38.1) * mm});
            skArc(sketch, "E31.18.25.0", {"start": v(66.07, 38.23) * mm, "mid": v(67.38, 40.94) * mm, "end": v(68.25, 43.81) * mm});
            skArc(sketch, "E31.22.25.0", {"start": v(68.25, 43.81) * mm, "mid": v(68.26, 44.05) * mm, "end": v(68.18, 44.27) * mm});
            skArc(sketch, "E31.26.25.0", {"start": v(68.17, 44.28) * mm, "mid": v(68, 44.44) * mm, "end": v(67.79, 44.53) * mm});
            skArc(sketch, "E31.30.25.0", {"start": v(65.87, 38.02) * mm, "mid": v(65.98, 38.11) * mm, "end": v(66.07, 38.23) * mm});
            skArc(sketch, "E31.34.25.0", {"start": v(61.8, 44.8) * mm, "mid": v(61.65, 44.77) * mm, "end": v(61.52, 44.7) * mm});
            skLineSegment(sketch, "E31.38.25.0", {"start": v(68.18, 44.27) * mm, "end": v(68.18, 44.28) * mm});
            skLineSegment(sketch, "E31.41.25.0", {"start": v(68.17, 44.28) * mm, "end": v(68.18, 44.28) * mm});
            skArc(sketch, "E31.2.26.0", {"start": v(46.94, 53.42) * mm, "mid": v(47.38, 53.27) * mm, "end": v(47.81, 53.45) * mm});
            skLineSegment(sketch, "E31.4.26.0", {"start": v(50.88, 56.52) * mm, "end": v(47.81, 53.45) * mm});
            skLineSegment(sketch, "E31.7.26.0", {"start": v(56.52, 50.88) * mm, "end": v(53.45, 47.81) * mm});
            skPoint(sketch, "E31.10.26.0", {"position": v(57.65, 57.3) * mm});
            skPoint(sketch, "E31.11.26.0", {"position": v(50.99, 56.63) * mm});
            skPoint(sketch, "E31.12.26.0", {"position": v(57.3, 57.65) * mm});
            skArc(sketch, "E31.13.26.0", {"start": v(51.13, 56.68) * mm, "mid": v(54.05, 57.4) * mm, "end": v(57.05, 57.65) * mm});
            skPoint(sketch, "E31.17.26.0", {"position": v(56.63, 50.99) * mm});
            skArc(sketch, "E31.18.26.0", {"start": v(56.68, 51.13) * mm, "mid": v(57.4, 54.05) * mm, "end": v(57.65, 57.05) * mm});
            skArc(sketch, "E31.22.26.0", {"start": v(57.65, 57.05) * mm, "mid": v(57.61, 57.28) * mm, "end": v(57.49, 57.48) * mm});
            skArc(sketch, "E31.26.26.0", {"start": v(57.48, 57.49) * mm, "mid": v(57.28, 57.61) * mm, "end": v(57.05, 57.65) * mm});
            skArc(sketch, "E31.30.26.0", {"start": v(56.52, 50.88) * mm, "mid": v(56.61, 51) * mm, "end": v(56.68, 51.13) * mm});
            skArc(sketch, "E31.34.26.0", {"start": v(51.13, 56.68) * mm, "mid": v(51, 56.61) * mm, "end": v(50.88, 56.52) * mm});
            skLineSegment(sketch, "E31.38.26.0", {"start": v(57.49, 57.48) * mm, "end": v(57.48, 57.48) * mm});
            skLineSegment(sketch, "E31.41.26.0", {"start": v(57.48, 57.49) * mm, "end": v(57.48, 57.48) * mm});
            skArc(sketch, "E31.2.27.0", {"start": v(34.81, 62.02) * mm, "mid": v(35.27, 61.96) * mm, "end": v(35.65, 62.23) * mm});
            skLineSegment(sketch, "E31.4.27.0", {"start": v(38.02, 65.87) * mm, "end": v(35.65, 62.23) * mm});
            skLineSegment(sketch, "E31.7.27.0", {"start": v(44.7, 61.52) * mm, "end": v(42.34, 57.88) * mm});
            skPoint(sketch, "E31.10.27.0", {"position": v(44.48, 68.03) * mm});
            skPoint(sketch, "E31.11.27.0", {"position": v(38.1, 66) * mm});
            skPoint(sketch, "E31.12.27.0", {"position": v(44.06, 68.3) * mm});
            skArc(sketch, "E31.13.27.0", {"start": v(38.23, 66.07) * mm, "mid": v(40.94, 67.38) * mm, "end": v(43.81, 68.25) * mm});
            skPoint(sketch, "E31.17.27.0", {"position": v(44.79, 61.65) * mm});
            skArc(sketch, "E31.18.27.0", {"start": v(44.8, 61.8) * mm, "mid": v(44.9, 64.8) * mm, "end": v(44.53, 67.79) * mm});
            skArc(sketch, "E31.22.27.0", {"start": v(44.53, 67.79) * mm, "mid": v(44.44, 68) * mm, "end": v(44.28, 68.17) * mm});
            skArc(sketch, "E31.26.27.0", {"start": v(44.27, 68.18) * mm, "mid": v(44.05, 68.26) * mm, "end": v(43.81, 68.25) * mm});
            skArc(sketch, "E31.30.27.0", {"start": v(44.7, 61.52) * mm, "mid": v(44.77, 61.65) * mm, "end": v(44.8, 61.8) * mm});
            skArc(sketch, "E31.34.27.0", {"start": v(38.23, 66.07) * mm, "mid": v(38.11, 65.98) * mm, "end": v(38.02, 65.87) * mm});
            skLineSegment(sketch, "E31.38.27.0", {"start": v(44.28, 68.17) * mm, "end": v(44.28, 68.18) * mm});
            skLineSegment(sketch, "E31.41.27.0", {"start": v(44.27, 68.18) * mm, "end": v(44.28, 68.18) * mm});
            skArc(sketch, "E31.2.28.0", {"start": v(21.16, 67.9) * mm, "mid": v(21.62, 67.94) * mm, "end": v(21.94, 68.28) * mm});
            skLineSegment(sketch, "E31.4.28.0", {"start": v(23.5, 72.33) * mm, "end": v(21.94, 68.28) * mm});
            skLineSegment(sketch, "E31.7.28.0", {"start": v(30.94, 69.47) * mm, "end": v(29.38, 65.42) * mm});
            skPoint(sketch, "E31.10.28.0", {"position": v(29.36, 75.8) * mm});
            skPoint(sketch, "E31.11.28.0", {"position": v(23.55, 72.47) * mm});
            skPoint(sketch, "E31.12.28.0", {"position": v(28.9, 75.97) * mm});
            skArc(sketch, "E31.13.28.0", {"start": v(23.66, 72.57) * mm, "mid": v(26.03, 74.42) * mm, "end": v(28.67, 75.87) * mm});
            skPoint(sketch, "E31.17.28.0", {"position": v(31, 69.61) * mm});
            skArc(sketch, "E31.18.28.0", {"start": v(30.98, 69.76) * mm, "mid": v(30.45, 72.72) * mm, "end": v(29.47, 75.56) * mm});
            skArc(sketch, "E31.22.28.0", {"start": v(29.47, 75.56) * mm, "mid": v(29.33, 75.76) * mm, "end": v(29.14, 75.89) * mm});
            skArc(sketch, "E31.26.28.0", {"start": v(29.12, 75.9) * mm, "mid": v(28.9, 75.93) * mm, "end": v(28.67, 75.87) * mm});
            skArc(sketch, "E31.30.28.0", {"start": v(30.94, 69.47) * mm, "mid": v(30.98, 69.62) * mm, "end": v(30.98, 69.76) * mm});
            skArc(sketch, "E31.34.28.0", {"start": v(23.66, 72.57) * mm, "mid": v(23.56, 72.46) * mm, "end": v(23.5, 72.33) * mm});
            skLineSegment(sketch, "E31.38.28.0", {"start": v(29.14, 75.89) * mm, "end": v(29.13, 75.9) * mm});
            skLineSegment(sketch, "E31.41.28.0", {"start": v(29.12, 75.9) * mm, "end": v(29.13, 75.9) * mm});
            skArc(sketch, "E31.2.29.0", {"start": v(6.58, 70.82) * mm, "mid": v(7.03, 70.95) * mm, "end": v(7.26, 71.35) * mm});
            skLineSegment(sketch, "E31.4.29.0", {"start": v(7.94, 75.64) * mm, "end": v(7.26, 71.35) * mm});
            skLineSegment(sketch, "E31.7.29.0", {"start": v(15.82, 74.39) * mm, "end": v(15.14, 70.1) * mm});
            skPoint(sketch, "E31.10.29.0", {"position": v(12.96, 80.24) * mm});
            skPoint(sketch, "E31.11.29.0", {"position": v(7.97, 75.78) * mm});
            skPoint(sketch, "E31.12.29.0", {"position": v(12.46, 80.32) * mm});
            skArc(sketch, "E31.13.29.0", {"start": v(8.05, 75.9) * mm, "mid": v(9.99, 78.2) * mm, "end": v(12.26, 80.17) * mm});
            skPoint(sketch, "E31.17.29.0", {"position": v(15.84, 74.53) * mm});
            skArc(sketch, "E31.18.29.0", {"start": v(15.8, 74.68) * mm, "mid": v(14.67, 77.47) * mm, "end": v(13.11, 80.04) * mm});
            skArc(sketch, "E31.22.29.0", {"start": v(13.11, 80.04) * mm, "mid": v(12.94, 80.2) * mm, "end": v(12.73, 80.29) * mm});
            skArc(sketch, "E31.26.29.0", {"start": v(12.7, 80.3) * mm, "mid": v(12.47, 80.27) * mm, "end": v(12.26, 80.17) * mm});
            skArc(sketch, "E31.30.29.0", {"start": v(15.82, 74.39) * mm, "mid": v(15.83, 74.53) * mm, "end": v(15.8, 74.68) * mm});
            skArc(sketch, "E31.34.29.0", {"start": v(8.05, 75.9) * mm, "mid": v(7.98, 75.78) * mm, "end": v(7.94, 75.64) * mm});
            skLineSegment(sketch, "E31.38.29.0", {"start": v(12.73, 80.29) * mm, "end": v(12.72, 80.3) * mm});
            skLineSegment(sketch, "E31.41.29.0", {"start": v(12.7, 80.3) * mm, "end": v(12.72, 80.3) * mm});
            skArc(sketch, "E32.1.0", {"start": v(-14.68, 70.2) * mm, "mid": v(-14.4, 69.82) * mm, "end": v(-13.94, 69.74) * mm});
            skArc(sketch, "E32.2.0", {"start": v(-28.96, 65.61) * mm, "mid": v(-28.6, 65.3) * mm, "end": v(-28.14, 65.32) * mm});
            skArc(sketch, "E32.3.0", {"start": v(-41.96, 58.16) * mm, "mid": v(-41.56, 57.93) * mm, "end": v(-41.1, 58.04) * mm});
            skArc(sketch, "E32.4.0", {"start": v(-53.14, 48.16) * mm, "mid": v(-52.7, 48.02) * mm, "end": v(-52.27, 48.23) * mm});
            skArc(sketch, "E32.5.0", {"start": v(-62, 36.06) * mm, "mid": v(-61.53, 36.02) * mm, "end": v(-61.16, 36.3) * mm});
            skArc(sketch, "E32.6.0", {"start": v(-68.13, 22.39) * mm, "mid": v(-67.67, 22.44) * mm, "end": v(-67.37, 22.8) * mm});
            skArc(sketch, "E32.7.0", {"start": v(-71.3, 7.73) * mm, "mid": v(-70.86, 7.88) * mm, "end": v(-70.64, 8.3) * mm});
            skArc(sketch, "E32.8.0", {"start": v(-71.35, -7.26) * mm, "mid": v(-70.95, -7.03) * mm, "end": v(-70.82, -6.58) * mm});
            skArc(sketch, "E32.9.0", {"start": v(-68.28, -21.94) * mm, "mid": v(-67.94, -21.62) * mm, "end": v(-67.9, -21.16) * mm});
            skArc(sketch, "E32.10.0", {"start": v(-62.23, -35.65) * mm, "mid": v(-61.96, -35.27) * mm, "end": v(-62.02, -34.81) * mm});
            skArc(sketch, "E32.11.0", {"start": v(-53.45, -47.81) * mm, "mid": v(-53.27, -47.38) * mm, "end": v(-53.42, -46.94) * mm});
            skArc(sketch, "E32.12.0", {"start": v(-42.34, -57.88) * mm, "mid": v(-42.25, -57.42) * mm, "end": v(-42.5, -57.03) * mm});
            skArc(sketch, "E32.13.0", {"start": v(-29.38, -65.42) * mm, "mid": v(-29.39, -64.95) * mm, "end": v(-29.71, -64.62) * mm});
            skArc(sketch, "E32.14.0", {"start": v(-15.14, -70.1) * mm, "mid": v(-15.24, -69.64) * mm, "end": v(-15.63, -69.38) * mm});
            skArc(sketch, "E32.15.0", {"start": v(-0.23, -71.72) * mm, "mid": v(-0.43, -71.3) * mm, "end": v(-0.86, -71.11) * mm});
            skArc(sketch, "E32.16.0", {"start": v(14.68, -70.2) * mm, "mid": v(14.4, -69.82) * mm, "end": v(13.94, -69.74) * mm});
            skArc(sketch, "E32.17.0", {"start": v(28.96, -65.61) * mm, "mid": v(28.6, -65.3) * mm, "end": v(28.14, -65.32) * mm});
            skArc(sketch, "E32.18.0", {"start": v(41.96, -58.16) * mm, "mid": v(41.56, -57.93) * mm, "end": v(41.1, -58.04) * mm});
            skArc(sketch, "E32.19.0", {"start": v(53.14, -48.16) * mm, "mid": v(52.7, -48.02) * mm, "end": v(52.27, -48.23) * mm});
            skArc(sketch, "E32.20.0", {"start": v(62, -36.06) * mm, "mid": v(61.53, -36.02) * mm, "end": v(61.16, -36.3) * mm});
            skArc(sketch, "E32.21.0", {"start": v(68.13, -22.39) * mm, "mid": v(67.67, -22.44) * mm, "end": v(67.37, -22.8) * mm});
            skArc(sketch, "E32.22.0", {"start": v(71.3, -7.73) * mm, "mid": v(70.86, -7.88) * mm, "end": v(70.64, -8.3) * mm});
            skArc(sketch, "E32.23.0", {"start": v(71.35, 7.26) * mm, "mid": v(70.95, 7.03) * mm, "end": v(70.82, 6.58) * mm});
            skArc(sketch, "E32.24.0", {"start": v(68.28, 21.94) * mm, "mid": v(67.94, 21.62) * mm, "end": v(67.9, 21.16) * mm});
            skArc(sketch, "E32.25.0", {"start": v(62.23, 35.65) * mm, "mid": v(61.96, 35.27) * mm, "end": v(62.02, 34.81) * mm});
            skArc(sketch, "E32.26.0", {"start": v(53.45, 47.81) * mm, "mid": v(53.27, 47.38) * mm, "end": v(53.42, 46.94) * mm});
            skArc(sketch, "E32.27.0", {"start": v(42.34, 57.88) * mm, "mid": v(42.25, 57.42) * mm, "end": v(42.5, 57.03) * mm});
            skArc(sketch, "E32.28.0", {"start": v(29.38, 65.42) * mm, "mid": v(29.39, 64.95) * mm, "end": v(29.71, 64.62) * mm});
            skArc(sketch, "E32.29.0", {"start": v(15.14, 70.1) * mm, "mid": v(15.24, 69.64) * mm, "end": v(15.63, 69.38) * mm});
            skSolve(sketch);
        }
        {
            var Q0;
            Q0=makeQuery(id+"F0.imprint","IMPRINT",FACE,{"disambiguationData":[TD([[makeQuery(id+"F0.imprint","IMPRINT",EDGE,{"derivedFrom":sQuery(id+"F0.wireOp",EDGE,"E17")}),1.0]])]});
            var Q1;
            {var subQ0=sQuery(id+"F0.wireOp",EDGE,"E14.18.0");Q1=makeQuery(id+"F0.imprint","IMPRINT",FACE,{"disambiguationData":[TD([[makeQuery(id+"F0.imprint","IMPRINT",EDGE,{"derivedFrom":subQ0}),-1.0]])]});}
            var Q2;
            {var subQ0=sQuery(id+"F0.wireOp",EDGE,"E14.21.0");Q2=makeQuery(id+"F0.imprint","IMPRINT",FACE,{"disambiguationData":[TD([[makeQuery(id+"F0.imprint","IMPRINT",EDGE,{"derivedFrom":subQ0}),-1.0]])]});}
            var Q3;
            {var subQ0=sQuery(id+"F0.wireOp",EDGE,"E14.23.0");Q3=makeQuery(id+"F0.imprint","IMPRINT",FACE,{"disambiguationData":[TD([[makeQuery(id+"F0.imprint","IMPRINT",EDGE,{"derivedFrom":subQ0}),-1.0]])]});}
            var Q4;
            {var subQ1=sQuery(id+"F0.wireOp",EDGE,"E14.24.0");Q4=makeQuery(id+"F0.imprint","IMPRINT",FACE,{"disambiguationData":[TD([[makeQuery(id+"F0.imprint","IMPRINT",EDGE,{"derivedFrom":subQ1}),-1.0]])]});}
            var Q5;
            {var subQ0=sQuery(id+"F0.wireOp",EDGE,"E14.25.0");Q5=makeQuery(id+"F0.imprint","IMPRINT",FACE,{"disambiguationData":[TD([[makeQuery(id+"F0.imprint","IMPRINT",EDGE,{"derivedFrom":subQ0}),-1.0]])]});}
            var Q6;
            {var subQ0=sQuery(id+"F0.wireOp",EDGE,"E14.27.0");Q6=makeQuery(id+"F0.imprint","IMPRINT",FACE,{"disambiguationData":[TD([[makeQuery(id+"F0.imprint","IMPRINT",EDGE,{"derivedFrom":subQ0}),-1.0]])]});}
            var Q7;
            {var subQ0=sQuery(id+"F0.wireOp",EDGE,"E14.28.0");Q7=makeQuery(id+"F0.imprint","IMPRINT",FACE,{"disambiguationData":[TD([[makeQuery(id+"F0.imprint","IMPRINT",EDGE,{"derivedFrom":subQ0}),-1.0]])]});}
            var Q8;
            {var subQ1=sQuery(id+"F0.wireOp",EDGE,"E14.1.0");Q8=makeQuery(id+"F0.imprint","IMPRINT",FACE,{"disambiguationData":[TD([[makeQuery(id+"F0.imprint","IMPRINT",EDGE,{"derivedFrom":subQ1}),-1.0]])]});}
            var Q9;
            {var subQ0=sQuery(id+"F0.wireOp",EDGE,"E14.2.0");Q9=makeQuery(id+"F0.imprint","IMPRINT",FACE,{"disambiguationData":[TD([[makeQuery(id+"F0.imprint","IMPRINT",EDGE,{"derivedFrom":subQ0}),-1.0]])]});}
            var Q10;
            {var subQ0=sQuery(id+"F0.wireOp",EDGE,"E14.3.0");Q10=makeQuery(id+"F0.imprint","IMPRINT",FACE,{"disambiguationData":[TD([[makeQuery(id+"F0.imprint","IMPRINT",EDGE,{"derivedFrom":subQ0}),-1.0]])]});}
            var Q11;
            {var subQ0=sQuery(id+"F0.wireOp",EDGE,"E14.4.0");Q11=makeQuery(id+"F0.imprint","IMPRINT",FACE,{"disambiguationData":[TD([[makeQuery(id+"F0.imprint","IMPRINT",EDGE,{"derivedFrom":subQ0}),-1.0]])]});}
            var Q12;
            {var subQ0=sQuery(id+"F0.wireOp",EDGE,"E14.5.0");Q12=makeQuery(id+"F0.imprint","IMPRINT",FACE,{"disambiguationData":[TD([[makeQuery(id+"F0.imprint","IMPRINT",EDGE,{"derivedFrom":subQ0}),-1.0]])]});}
            var Q13;
            {var subQ0=sQuery(id+"F0.wireOp",EDGE,"E14.20.0");Q13=makeQuery(id+"F0.imprint","IMPRINT",FACE,{"disambiguationData":[TD([[makeQuery(id+"F0.imprint","IMPRINT",EDGE,{"derivedFrom":subQ0}),-1.0]])]});}
            var Q14;
            {var subQ1=sQuery(id+"F0.wireOp",EDGE,"E14.22.0");Q14=makeQuery(id+"F0.imprint","IMPRINT",FACE,{"disambiguationData":[TD([[makeQuery(id+"F0.imprint","IMPRINT",EDGE,{"derivedFrom":subQ1}),-1.0]])]});}
            var Q15;
            {var subQ0=sQuery(id+"F0.wireOp",EDGE,"E14.26.0");Q15=makeQuery(id+"F0.imprint","IMPRINT",FACE,{"disambiguationData":[TD([[makeQuery(id+"F0.imprint","IMPRINT",EDGE,{"derivedFrom":subQ0}),-1.0]])]});}
            var Q16;
            Q16=makeQuery(id+"F0.imprint","IMPRINT",FACE,{"disambiguationData":[TD([[makeQuery(id+"F0.imprint","IMPRINT",EDGE,{"derivedFrom":sQuery(id+"F0.wireOp",EDGE,"E0.MirrorCS")}),1.0]])]});
            var Q17;
            {var subQ0=sQuery(id+"F0.wireOp",EDGE,"E14.29.0");Q17=makeQuery(id+"F0.imprint","IMPRINT",FACE,{"disambiguationData":[TD([[makeQuery(id+"F0.imprint","IMPRINT",EDGE,{"derivedFrom":subQ0}),-1.0]])]});}
            var Q18;
            {var subQ0=sQuery(id+"F0.wireOp",EDGE,"E14.19.0");Q18=makeQuery(id+"F0.imprint","IMPRINT",FACE,{"disambiguationData":[TD([[makeQuery(id+"F0.imprint","IMPRINT",EDGE,{"derivedFrom":subQ0}),-1.0]])]});}
            var Q19;
            {var subQ0=sQuery(id+"F0.wireOp",EDGE,"E14.6.0");Q19=makeQuery(id+"F0.imprint","IMPRINT",FACE,{"disambiguationData":[TD([[makeQuery(id+"F0.imprint","IMPRINT",EDGE,{"derivedFrom":subQ0}),-1.0]])]});}
            var Q20;
            {var subQ1=sQuery(id+"F0.wireOp",EDGE,"E14.15.0");Q20=makeQuery(id+"F0.imprint","IMPRINT",FACE,{"disambiguationData":[TD([[makeQuery(id+"F0.imprint","IMPRINT",EDGE,{"derivedFrom":subQ1}),-1.0]])]});}
            var Q21;
            {var subQ0=sQuery(id+"F0.wireOp",EDGE,"E14.13.0");Q21=makeQuery(id+"F0.imprint","IMPRINT",FACE,{"disambiguationData":[TD([[makeQuery(id+"F0.imprint","IMPRINT",EDGE,{"derivedFrom":subQ0}),-1.0]])]});}
            var Q22;
            {var subQ0=sQuery(id+"F0.wireOp",EDGE,"E14.14.0");Q22=makeQuery(id+"F0.imprint","IMPRINT",FACE,{"disambiguationData":[TD([[makeQuery(id+"F0.imprint","IMPRINT",EDGE,{"derivedFrom":subQ0}),-1.0]])]});}
            var Q23;
            {var subQ0=sQuery(id+"F0.wireOp",EDGE,"E14.11.0");Q23=makeQuery(id+"F0.imprint","IMPRINT",FACE,{"disambiguationData":[TD([[makeQuery(id+"F0.imprint","IMPRINT",EDGE,{"derivedFrom":subQ0}),-1.0]])]});}
            var Q24;
            {var subQ0=sQuery(id+"F0.wireOp",EDGE,"E14.12.0");Q24=makeQuery(id+"F0.imprint","IMPRINT",FACE,{"disambiguationData":[TD([[makeQuery(id+"F0.imprint","IMPRINT",EDGE,{"derivedFrom":subQ0}),-1.0]])]});}
            var Q25;
            {var subQ0=sQuery(id+"F0.wireOp",EDGE,"E14.16.0");Q25=makeQuery(id+"F0.imprint","IMPRINT",FACE,{"disambiguationData":[TD([[makeQuery(id+"F0.imprint","IMPRINT",EDGE,{"derivedFrom":subQ0}),-1.0]])]});}
            var Q26;
            {var subQ1=sQuery(id+"F0.wireOp",EDGE,"E14.17.0");Q26=makeQuery(id+"F0.imprint","IMPRINT",FACE,{"disambiguationData":[TD([[makeQuery(id+"F0.imprint","IMPRINT",EDGE,{"derivedFrom":subQ1}),-1.0]])]});}
            var Q27;
            {var subQ0=sQuery(id+"F0.wireOp",EDGE,"E14.7.0");Q27=makeQuery(id+"F0.imprint","IMPRINT",FACE,{"disambiguationData":[TD([[makeQuery(id+"F0.imprint","IMPRINT",EDGE,{"derivedFrom":subQ0}),-1.0]])]});}
            var Q28;
            {var subQ1=sQuery(id+"F0.wireOp",EDGE,"E14.8.0");Q28=makeQuery(id+"F0.imprint","IMPRINT",FACE,{"disambiguationData":[TD([[makeQuery(id+"F0.imprint","IMPRINT",EDGE,{"derivedFrom":subQ1}),-1.0]])]});}
            var Q29;
            {var subQ0=sQuery(id+"F0.wireOp",EDGE,"E14.9.0");Q29=makeQuery(id+"F0.imprint","IMPRINT",FACE,{"disambiguationData":[TD([[makeQuery(id+"F0.imprint","IMPRINT",EDGE,{"derivedFrom":subQ0}),-1.0]])]});}
            var Q30;
            {var subQ1=sQuery(id+"F0.wireOp",EDGE,"E14.10.0");Q30=makeQuery(id+"F0.imprint","IMPRINT",FACE,{"disambiguationData":[TD([[makeQuery(id+"F0.imprint","IMPRINT",EDGE,{"derivedFrom":subQ1}),-1.0]])]});}
            var Q31;
            {var subQ0=sQuery(id+"F0.wireOp",EDGE,"E30.1.38.0");Q31=makeQuery(id+"F0.imprint","IMPRINT",FACE,{"disambiguationData":[TD([[makeQuery(id+"F0.imprint","IMPRINT",EDGE,{"derivedFrom":subQ0}),-1.0]])]});}
            var Q32;
            {var subQ0=sQuery(id+"F0.wireOp",EDGE,"E30.1.36.0");Q32=makeQuery(id+"F0.imprint","IMPRINT",FACE,{"disambiguationData":[TD([[makeQuery(id+"F0.imprint","IMPRINT",EDGE,{"derivedFrom":subQ0}),-1.0]])]});}
            var Q33;
            {var subQ0=sQuery(id+"F0.wireOp",EDGE,"E30.1.40.0");Q33=makeQuery(id+"F0.imprint","IMPRINT",FACE,{"disambiguationData":[TD([[makeQuery(id+"F0.imprint","IMPRINT",EDGE,{"derivedFrom":subQ0}),-1.0]])]});}
            var Q34;
            {var subQ0=sQuery(id+"F0.wireOp",EDGE,"E30.1.47.0");Q34=makeQuery(id+"F0.imprint","IMPRINT",FACE,{"disambiguationData":[TD([[makeQuery(id+"F0.imprint","IMPRINT",EDGE,{"derivedFrom":subQ0}),-1.0]])]});}
            var Q35;
            {var subQ0=sQuery(id+"F0.wireOp",EDGE,"E30.1.32.0");Q35=makeQuery(id+"F0.imprint","IMPRINT",FACE,{"disambiguationData":[TD([[makeQuery(id+"F0.imprint","IMPRINT",EDGE,{"derivedFrom":subQ0}),-1.0]])]});}
            var Q36;
            {var subQ0=sQuery(id+"F0.wireOp",EDGE,"E30.1.39.0");Q36=makeQuery(id+"F0.imprint","IMPRINT",FACE,{"disambiguationData":[TD([[makeQuery(id+"F0.imprint","IMPRINT",EDGE,{"derivedFrom":subQ0}),-1.0]])]});}
            var Q37;
            {var subQ0=sQuery(id+"F0.wireOp",EDGE,"E30.1.37.0");Q37=makeQuery(id+"F0.imprint","IMPRINT",FACE,{"disambiguationData":[TD([[makeQuery(id+"F0.imprint","IMPRINT",EDGE,{"derivedFrom":subQ0}),-1.0]])]});}
            var Q38;
            {var subQ0=sQuery(id+"F0.wireOp",EDGE,"E30.1.41.0");Q38=makeQuery(id+"F0.imprint","IMPRINT",FACE,{"disambiguationData":[TD([[makeQuery(id+"F0.imprint","IMPRINT",EDGE,{"derivedFrom":subQ0}),-1.0]])]});}
            var Q39;
            {var subQ0=sQuery(id+"F0.wireOp",EDGE,"E30.1.42.0");Q39=makeQuery(id+"F0.imprint","IMPRINT",FACE,{"disambiguationData":[TD([[makeQuery(id+"F0.imprint","IMPRINT",EDGE,{"derivedFrom":subQ0}),-1.0]])]});}
            var Q40;
            {var subQ0=sQuery(id+"F0.wireOp",EDGE,"E30.1.44.0");Q40=makeQuery(id+"F0.imprint","IMPRINT",FACE,{"disambiguationData":[TD([[makeQuery(id+"F0.imprint","IMPRINT",EDGE,{"derivedFrom":subQ0}),-1.0]])]});}
            var Q41;
            {var subQ0=sQuery(id+"F0.wireOp",EDGE,"E30.1.46.0");Q41=makeQuery(id+"F0.imprint","IMPRINT",FACE,{"disambiguationData":[TD([[makeQuery(id+"F0.imprint","IMPRINT",EDGE,{"derivedFrom":subQ0}),-1.0]])]});}
            var Q42;
            {var subQ0=sQuery(id+"F0.wireOp",EDGE,"E30.1.48.0");Q42=makeQuery(id+"F0.imprint","IMPRINT",FACE,{"disambiguationData":[TD([[makeQuery(id+"F0.imprint","IMPRINT",EDGE,{"derivedFrom":subQ0}),-1.0]])]});}
            var Q43;
            {var subQ0=sQuery(id+"F0.wireOp",EDGE,"E30.1.45.0");Q43=makeQuery(id+"F0.imprint","IMPRINT",FACE,{"disambiguationData":[TD([[makeQuery(id+"F0.imprint","IMPRINT",EDGE,{"derivedFrom":subQ0}),-1.0]])]});}
            var Q44;
            {var subQ0=sQuery(id+"F0.wireOp",EDGE,"E30.1.30.0");Q44=makeQuery(id+"F0.imprint","IMPRINT",FACE,{"disambiguationData":[TD([[makeQuery(id+"F0.imprint","IMPRINT",EDGE,{"derivedFrom":subQ0}),-1.0]])]});}
            var Q45;
            {var subQ0=sQuery(id+"F0.wireOp",EDGE,"E30.1.35.0");Q45=makeQuery(id+"F0.imprint","IMPRINT",FACE,{"disambiguationData":[TD([[makeQuery(id+"F0.imprint","IMPRINT",EDGE,{"derivedFrom":subQ0}),-1.0]])]});}
            var Q46;
            {var subQ0=sQuery(id+"F0.wireOp",EDGE,"E30.1.49.0");Q46=makeQuery(id+"F0.imprint","IMPRINT",FACE,{"disambiguationData":[TD([[makeQuery(id+"F0.imprint","IMPRINT",EDGE,{"derivedFrom":subQ0}),-1.0]])]});}
            var Q47;
            {var subQ0=sQuery(id+"F0.wireOp",EDGE,"E30.1.34.0");Q47=makeQuery(id+"F0.imprint","IMPRINT",FACE,{"disambiguationData":[TD([[makeQuery(id+"F0.imprint","IMPRINT",EDGE,{"derivedFrom":subQ0}),-1.0]])]});}
            var Q48;
            {var subQ0=sQuery(id+"F0.wireOp",EDGE,"E30.1.33.0");Q48=makeQuery(id+"F0.imprint","IMPRINT",FACE,{"disambiguationData":[TD([[makeQuery(id+"F0.imprint","IMPRINT",EDGE,{"derivedFrom":subQ0}),-1.0]])]});}
            var Q49;
            {var subQ0=sQuery(id+"F0.wireOp",EDGE,"E30.1.43.0");Q49=makeQuery(id+"F0.imprint","IMPRINT",FACE,{"disambiguationData":[TD([[makeQuery(id+"F0.imprint","IMPRINT",EDGE,{"derivedFrom":subQ0}),-1.0]])]});}
            var Q50;
            {var subQ0=sQuery(id+"F0.wireOp",EDGE,"E30.1.31.0");Q50=makeQuery(id+"F0.imprint","IMPRINT",FACE,{"disambiguationData":[TD([[makeQuery(id+"F0.imprint","IMPRINT",EDGE,{"derivedFrom":subQ0}),-1.0]])]});}
            var Q51;
            {var subQ1=sQuery(id+"F0.wireOp",EDGE,"E31.2.7.0");Q51=makeQuery(id+"F0.imprint","IMPRINT",FACE,{"disambiguationData":[TD([[makeQuery(id+"F0.imprint","IMPRINT",EDGE,{"derivedFrom":subQ1}),-1.0]])]});}
            var Q52;
            {var subQ0=sQuery(id+"F0.wireOp",EDGE,"E31.2.9.0");Q52=makeQuery(id+"F0.imprint","IMPRINT",FACE,{"disambiguationData":[TD([[makeQuery(id+"F0.imprint","IMPRINT",EDGE,{"derivedFrom":subQ0}),-1.0]])]});}
            var Q53;
            {var subQ0=sQuery(id+"F0.wireOp",EDGE,"E31.2.13.0");Q53=makeQuery(id+"F0.imprint","IMPRINT",FACE,{"disambiguationData":[TD([[makeQuery(id+"F0.imprint","IMPRINT",EDGE,{"derivedFrom":subQ0}),-1.0]])]});}
            var Q54;
            {var subQ0=sQuery(id+"F0.wireOp",EDGE,"E31.2.8.0");Q54=makeQuery(id+"F0.imprint","IMPRINT",FACE,{"disambiguationData":[TD([[makeQuery(id+"F0.imprint","IMPRINT",EDGE,{"derivedFrom":subQ0}),-1.0]])]});}
            var Q55;
            {var subQ0=sQuery(id+"F0.wireOp",EDGE,"E31.2.12.0");Q55=makeQuery(id+"F0.imprint","IMPRINT",FACE,{"disambiguationData":[TD([[makeQuery(id+"F0.imprint","IMPRINT",EDGE,{"derivedFrom":subQ0}),-1.0]])]});}
            var Q56;
            {var subQ0=sQuery(id+"F0.wireOp",EDGE,"E31.2.3.0");Q56=makeQuery(id+"F0.imprint","IMPRINT",FACE,{"disambiguationData":[TD([[makeQuery(id+"F0.imprint","IMPRINT",EDGE,{"derivedFrom":subQ0}),-1.0]])]});}
            var Q57;
            {var subQ0=sQuery(id+"F0.wireOp",EDGE,"E31.2.4.0");Q57=makeQuery(id+"F0.imprint","IMPRINT",FACE,{"disambiguationData":[TD([[makeQuery(id+"F0.imprint","IMPRINT",EDGE,{"derivedFrom":subQ0}),-1.0]])]});}
            var Q58;
            {var subQ1=sQuery(id+"F0.wireOp",EDGE,"E31.2.5.0");Q58=makeQuery(id+"F0.imprint","IMPRINT",FACE,{"disambiguationData":[TD([[makeQuery(id+"F0.imprint","IMPRINT",EDGE,{"derivedFrom":subQ1}),-1.0]])]});}
            var Q59;
            {var subQ1=sQuery(id+"F0.wireOp",EDGE,"E31.2.14.0");Q59=makeQuery(id+"F0.imprint","IMPRINT",FACE,{"disambiguationData":[TD([[makeQuery(id+"F0.imprint","IMPRINT",EDGE,{"derivedFrom":subQ1}),-1.0]])]});}
            var Q60;
            {var subQ0=sQuery(id+"F0.wireOp",EDGE,"E31.2.15.0");Q60=makeQuery(id+"F0.imprint","IMPRINT",FACE,{"disambiguationData":[TD([[makeQuery(id+"F0.imprint","IMPRINT",EDGE,{"derivedFrom":subQ0}),-1.0]])]});}
            var Q61;
            {var subQ1=sQuery(id+"F0.wireOp",EDGE,"E31.2.16.0");Q61=makeQuery(id+"F0.imprint","IMPRINT",FACE,{"disambiguationData":[TD([[makeQuery(id+"F0.imprint","IMPRINT",EDGE,{"derivedFrom":subQ1}),-1.0]])]});}
            var Q62;
            {var subQ1=sQuery(id+"F0.wireOp",EDGE,"E29.1.0");Q62=makeQuery(id+"F0.imprint","IMPRINT",FACE,{"disambiguationData":[TD([[makeQuery(id+"F0.imprint","IMPRINT",EDGE,{"derivedFrom":subQ1}),-1.0]])]});}
            var Q63;
            {var subQ0=sQuery(id+"F0.wireOp",EDGE,"E29.2.0");Q63=makeQuery(id+"F0.imprint","IMPRINT",FACE,{"disambiguationData":[TD([[makeQuery(id+"F0.imprint","IMPRINT",EDGE,{"derivedFrom":subQ0}),-1.0]])]});}
            var Q64;
            {var subQ0=sQuery(id+"F0.wireOp",EDGE,"E31.2.18.0");Q64=makeQuery(id+"F0.imprint","IMPRINT",FACE,{"disambiguationData":[TD([[makeQuery(id+"F0.imprint","IMPRINT",EDGE,{"derivedFrom":subQ0}),-1.0]])]});}
            var Q65;
            {var subQ0=sQuery(id+"F0.wireOp",EDGE,"E31.2.17.0");Q65=makeQuery(id+"F0.imprint","IMPRINT",FACE,{"disambiguationData":[TD([[makeQuery(id+"F0.imprint","IMPRINT",EDGE,{"derivedFrom":subQ0}),-1.0]])]});}
            var Q66;
            {var subQ0=sQuery(id+"F0.wireOp",EDGE,"E31.2.19.0");Q66=makeQuery(id+"F0.imprint","IMPRINT",FACE,{"disambiguationData":[TD([[makeQuery(id+"F0.imprint","IMPRINT",EDGE,{"derivedFrom":subQ0}),-1.0]])]});}
            var Q67;
            {var subQ0=sQuery(id+"F0.wireOp",EDGE,"E31.2.20.0");Q67=makeQuery(id+"F0.imprint","IMPRINT",FACE,{"disambiguationData":[TD([[makeQuery(id+"F0.imprint","IMPRINT",EDGE,{"derivedFrom":subQ0}),-1.0]])]});}
            var Q68;
            {var subQ0=sQuery(id+"F0.wireOp",EDGE,"E31.2.25.0");Q68=makeQuery(id+"F0.imprint","IMPRINT",FACE,{"disambiguationData":[TD([[makeQuery(id+"F0.imprint","IMPRINT",EDGE,{"derivedFrom":subQ0}),-1.0]])]});}
            var Q69;
            {var subQ0=sQuery(id+"F0.wireOp",EDGE,"E31.2.6.0");Q69=makeQuery(id+"F0.imprint","IMPRINT",FACE,{"disambiguationData":[TD([[makeQuery(id+"F0.imprint","IMPRINT",EDGE,{"derivedFrom":subQ0}),-1.0]])]});}
            var Q70;
            {var subQ0=sQuery(id+"F0.wireOp",EDGE,"E31.2.11.0");Q70=makeQuery(id+"F0.imprint","IMPRINT",FACE,{"disambiguationData":[TD([[makeQuery(id+"F0.imprint","IMPRINT",EDGE,{"derivedFrom":subQ0}),-1.0]])]});}
            var Q71;
            {var subQ1=sQuery(id+"F0.wireOp",EDGE,"E31.2.21.0");Q71=makeQuery(id+"F0.imprint","IMPRINT",FACE,{"disambiguationData":[TD([[makeQuery(id+"F0.imprint","IMPRINT",EDGE,{"derivedFrom":subQ1}),-1.0]])]});}
            var Q72;
            {var subQ0=sQuery(id+"F0.wireOp",EDGE,"E31.2.22.0");Q72=makeQuery(id+"F0.imprint","IMPRINT",FACE,{"disambiguationData":[TD([[makeQuery(id+"F0.imprint","IMPRINT",EDGE,{"derivedFrom":subQ0}),-1.0]])]});}
            var Q73;
            {var subQ0=sQuery(id+"F0.wireOp",EDGE,"E31.2.27.0");Q73=makeQuery(id+"F0.imprint","IMPRINT",FACE,{"disambiguationData":[TD([[makeQuery(id+"F0.imprint","IMPRINT",EDGE,{"derivedFrom":subQ0}),-1.0]])]});}
            var Q74;
            {var subQ0=sQuery(id+"F0.wireOp",EDGE,"E31.2.26.0");Q74=makeQuery(id+"F0.imprint","IMPRINT",FACE,{"disambiguationData":[TD([[makeQuery(id+"F0.imprint","IMPRINT",EDGE,{"derivedFrom":subQ0}),-1.0]])]});}
            var Q75;
            {var subQ0=sQuery(id+"F0.wireOp",EDGE,"E31.2.24.0");Q75=makeQuery(id+"F0.imprint","IMPRINT",FACE,{"disambiguationData":[TD([[makeQuery(id+"F0.imprint","IMPRINT",EDGE,{"derivedFrom":subQ0}),-1.0]])]});}
            var Q76;
            {var subQ0=sQuery(id+"F0.wireOp",EDGE,"E31.2.29.0");Q76=makeQuery(id+"F0.imprint","IMPRINT",FACE,{"disambiguationData":[TD([[makeQuery(id+"F0.imprint","IMPRINT",EDGE,{"derivedFrom":subQ0}),-1.0]])]});}
            var Q77;
            {var subQ1=sQuery(id+"F0.wireOp",EDGE,"E31.2.23.0");Q77=makeQuery(id+"F0.imprint","IMPRINT",FACE,{"disambiguationData":[TD([[makeQuery(id+"F0.imprint","IMPRINT",EDGE,{"derivedFrom":subQ1}),-1.0]])]});}
            var Q78;
            {var subQ0=sQuery(id+"F0.wireOp",EDGE,"E31.2.10.0");Q78=makeQuery(id+"F0.imprint","IMPRINT",FACE,{"disambiguationData":[TD([[makeQuery(id+"F0.imprint","IMPRINT",EDGE,{"derivedFrom":subQ0}),-1.0]])]});}
            var Q79;
            {var subQ1=sQuery(id+"F0.wireOp",EDGE,"E31.2.28.0");Q79=makeQuery(id+"F0.imprint","IMPRINT",FACE,{"disambiguationData":[TD([[makeQuery(id+"F0.imprint","IMPRINT",EDGE,{"derivedFrom":subQ1}),-1.0]])]});}
            extrude(context, id + "F1", {"entities" : qUnion([Q0, Q1, Q2, Q3, Q4, Q5, Q6, Q7, Q8, Q9, Q10, Q11, Q12, Q13, Q14, Q15, Q16, Q17, Q18, Q19, Q20, Q21, Q22, Q23, Q24, Q25, Q26, Q27, Q28, Q29, Q30, Q31, Q32, Q33, Q34, Q35, Q36, Q37, Q38, Q39, Q40, Q41, Q42, Q43, Q44, Q45, Q46, Q47, Q48, Q49, Q50, Q51, Q52, Q53, Q54, Q55, Q56, Q57, Q58, Q59, Q60, Q61, Q62, Q63, Q64, Q65, Q66, Q67, Q68, Q69, Q70, Q71, Q72, Q73, Q74, Q75, Q76, Q77, Q78, Q79]), "depth" : 127 * mm});
        }
    });
